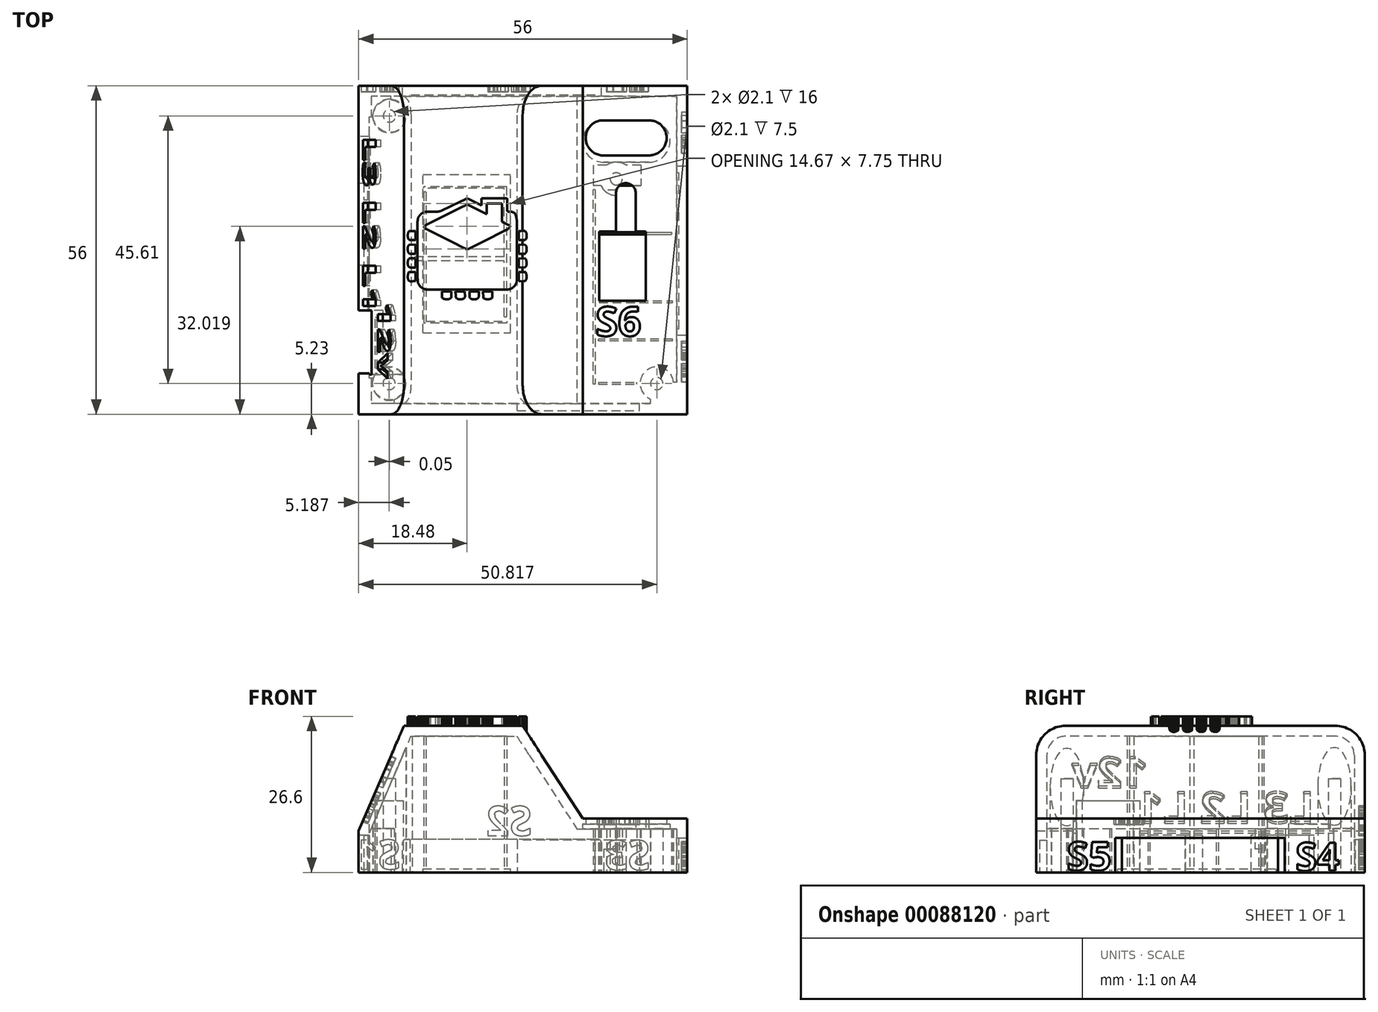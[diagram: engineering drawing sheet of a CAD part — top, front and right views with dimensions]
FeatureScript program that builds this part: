
annotation { "Feature Type Name" : "Feature", "Feature Type Description" : "" }
export const myFeature = defineFeature(function(context is Context, id is Id, definition is map)
    precondition{}
    {
        {
            var Q0;
            Q0=qCreatedBy(makeId("Top.planeOp"),FACE);
            var sketch = newSketch(context, id + "F0", { "sketchPlane" : qUnion([Q0])});
            skLineSegment(sketch, "E0.rect.bottom", {"start": v(22.84, -21.13) * mm, "end": v(-26.83, -21.13) * mm});
            skLineSegment(sketch, "E0.rect.top", {"start": v(22.84, 28.7) * mm, "end": v(-26.83, 28.7) * mm});
            skLineSegment(sketch, "E0.rect.left", {"start": v(22.84, -21.13) * mm, "end": v(22.84, 28.7) * mm});
            skPoint(sketch, "E0.rect.middle", {"position": v(-2, 3.78) * mm});
            skCircle(sketch, "E1", {"center": v(-24.81, -18.99) * mm, "radius": 1.05 * mm});
            skCircle(sketch, "E2", {"center": v(-24.76, 26.62) * mm, "radius": 1.05 * mm});
            skCircle(sketch, "E3", {"center": v(13.92, 15.91) * mm, "radius": 1.05 * mm});
            skLineSegment(sketch, "E4", {"start": v(-2, -21.13) * mm, "end": v(-2, -18.21) * mm});
            skCircle(sketch, "E5.MirrorC", {"center": v(20.82, -18.99) * mm, "radius": 1.05 * mm});
            skLineSegment(sketch, "E6.rect.bottom", {"start": v(24.75, -22.97) * mm, "end": v(-28.75, -22.97) * mm});
            skLineSegment(sketch, "E6.rect.top", {"start": v(24.75, 30.53) * mm, "end": v(-28.75, 30.53) * mm});
            skLineSegment(sketch, "E6.rect.left", {"start": v(24.75, -22.97) * mm, "end": v(24.75, 30.53) * mm});
            skLineSegment(sketch, "E6.rect.right", {"start": v(-28.75, -22.97) * mm, "end": v(-28.75, 30.53) * mm});
            skLineSegment(sketch, "E7.rect.bottom", {"start": v(26, -24.22) * mm, "end": v(-30, -24.22) * mm});
            skLineSegment(sketch, "E7.rect.top", {"start": v(26, 31.78) * mm, "end": v(-30, 31.78) * mm});
            skLineSegment(sketch, "E7.rect.left", {"start": v(26, -24.22) * mm, "end": v(26, 31.78) * mm});
            skLineSegment(sketch, "E7.rect.right", {"start": v(-30, -24.22) * mm, "end": v(-30, 31.78) * mm});
            skPoint(sketch, "E8", {"position": v(8.65, 14) * mm});
            skSolve(sketch);
        }
        {
            var Q0;
            Q0=qSketchRegion(id+"F0",true);
            var Q1;
            Q1=makeQuery(id+"F0.imprint","IMPRINT",FACE,{"disambiguationData":[TD([[makeQuery(id+"F0.imprint","IMPRINT",EDGE,{"derivedFrom":sQuery(id+"F0.wireOp",EDGE,"E1")}),-1.0]])]});
            extrude(context, id + "F1", {"entities" : qUnion([Q0, Q1]), "depth" : 25 * mm});
        }
        {
            var Q0;
            Q0=qCreatedBy(makeId("Front.planeOp"),FACE);
            var sketch = newSketch(context, id + "F2", { "sketchPlane" : qUnion([Q0])});
            skLineSegment(sketch, "E9", {"start": v(0, 0) * mm, "end": v(0, 7) * mm});
            skLineSegment(sketch, "E10", {"start": v(0, 7) * mm, "end": v(26.03, 7) * mm});
            skLineSegment(sketch, "E11", {"start": v(26.03, 9.19) * mm, "end": v(26.03, 25.51) * mm});
            skLineSegment(sketch, "E12", {"start": v(15.3, 7) * mm, "end": v(26.03, 7) * mm});
            skLineSegment(sketch, "E13", {"start": v(0, 7) * mm, "end": v(-30.02, 7) * mm});
            skLineSegment(sketch, "E14", {"start": v(-30.02, 7) * mm, "end": v(-22.06, 25.51) * mm});
            skLineSegment(sketch, "E15", {"start": v(-22.06, 25.51) * mm, "end": v(-2.39, 25.51) * mm});
            skLineSegment(sketch, "E16", {"start": v(26.03, 25.51) * mm, "end": v(-2.39, 25.51) * mm});
            skLineSegment(sketch, "E17", {"start": v(-22.06, 25.51) * mm, "end": v(-30.02, 25.51) * mm});
            skLineSegment(sketch, "E18", {"start": v(-30.02, 25.51) * mm, "end": v(-30.02, 7) * mm});
            skLineSegment(sketch, "E19", {"start": v(18.06, 10.7) * mm, "end": v(18.04, 10.7) * mm});
            skLineSegment(sketch, "E20", {"start": v(19.86, 9.19) * mm, "end": v(8.2, 9.19) * mm});
            skLineSegment(sketch, "E21", {"start": v(8.2, 9.19) * mm, "end": v(-2.39, 25.51) * mm});
            skLineSegment(sketch, "E22", {"start": v(19.86, 9.19) * mm, "end": v(26.03, 9.19) * mm});
            skSolve(sketch);
        }
        {
            var Q0;
            Q0=makeQuery(id+"F2.imprint","IMPRINT",FACE,{"disambiguationData":[TD([[makeQuery(id+"F2.imprint","IMPRINT",EDGE,{"derivedFrom":sQuery(id+"F2.wireOp",EDGE,"E14")}),1.0]])]});
            var Q1;
            {var subQ0=sQuery(id+"F2.wireOp",EDGE,"E11");Q1=makeQuery(id+"F2.imprint","IMPRINT",FACE,{"disambiguationData":[TD([[makeQuery(id+"F2.imprint","IMPRINT",EDGE,{"derivedFrom":subQ0}),1.0]])]});}
            extrude(context, id + "F3", {"entities" : qUnion([Q0, Q1]), "operationType" : NewBodyOperationType.REMOVE, "endBound" : BoundingType.UP_TO_NEXT, "oppositeDirection" : true, "depth" : 25 * mm, "hasSecondDirection" : true, "secondDirectionOppositeDirection" : false, "secondDirectionDepth" : 25 * mm});
        }
        {
            var Q0;
            Q0=makeQuery(id+"F1.opExtrude","CAP_EDGE",EDGE,{"disambiguationData":[OSD([sQuery(id+"F0.wireOp",EDGE,"E7.rect.right")])],"isStart":false});
            var Q1;
            Q1=makeQuery(id+"F3.boolean.opBoolean","COPY",EDGE,{"derivedFrom":makeQuery(id+"F3.opExtrude","TWEAK_EDGE",EDGE,{"derivedFrom":[makeQuery(id+"F1.opExtrude","CAP_FACE",FACE,{"disambiguationData":[OSD([sQuery(id+"F0.wireOp",EDGE,"E1"),sQuery(id+"F0.wireOp",EDGE,"E2"),sQuery(id+"F0.wireOp",EDGE,"E3"),sQuery(id+"F0.wireOp",EDGE,"E5.MirrorC"),sQuery(id+"F0.wireOp",EDGE,"E7.rect.bottom"),sQuery(id+"F0.wireOp",EDGE,"E7.rect.top"),sQuery(id+"F0.wireOp",EDGE,"E7.rect.left"),sQuery(id+"F0.wireOp",EDGE,"E7.rect.right")])],"isStart":false}),makeQuery(id+"F2.imprint","IMPRINT",EDGE,{"derivedFrom":sQuery(id+"F2.wireOp",EDGE,"ff17f17f-c23f-4b7b-92e3-773d52701edb")})]})});
            var Q2;
            Q2=makeQuery(id+"F3.boolean.opBoolean","COPY",EDGE,{"derivedFrom":makeQuery(id+"F3.opExtrude","TWEAK_EDGE",EDGE,{"derivedFrom":[makeQuery(id+"F1.opExtrude","CAP_FACE",FACE,{"disambiguationData":[OSD([sQuery(id+"F0.wireOp",EDGE,"E1"),sQuery(id+"F0.wireOp",EDGE,"E2"),sQuery(id+"F0.wireOp",EDGE,"E3"),sQuery(id+"F0.wireOp",EDGE,"E5.MirrorC"),sQuery(id+"F0.wireOp",EDGE,"E7.rect.bottom"),sQuery(id+"F0.wireOp",EDGE,"E7.rect.top"),sQuery(id+"F0.wireOp",EDGE,"E7.rect.left"),sQuery(id+"F0.wireOp",EDGE,"E7.rect.right")])],"isStart":false}),makeQuery(id+"F2.imprint","IMPRINT",EDGE,{"derivedFrom":sQuery(id+"F2.wireOp",EDGE,"7c30f75c-de24-4105-9ec6-0528e7197d9e")})]})});
            var Q3;
            {var subQ0=sQuery(id+"F2.wireOp",EDGE,"cpQ2IQLn-lepx-jHqE-Occg-QwCyzWVKbBFz");var subQ1=sQuery(id+"F2.wireOp",EDGE,"9136473a-ce9f-4df1-8e41-d79c079f6f02");var subQ2=makeQuery(id+"F2.imprint","INTERSECT",VERTEX,{"disambiguationData":[OD(0.0)],"derivedFrom":[subQ1,subQ0]});var subQ4=makeQuery(id+"F2.imprint","INTERSECT",VERTEX,{"disambiguationData":[OD(1.0)],"derivedFrom":[subQ1,subQ0]});Q3=makeQuery(id+"F3.boolean.opBoolean","COPY",EDGE,{"derivedFrom":makeQuery(id+"F3.opExtrude","TWEAK_EDGE",EDGE,{"derivedFrom":[makeQuery(id+"F1.opExtrude","CAP_FACE",FACE,{"disambiguationData":[OSD([sQuery(id+"F0.wireOp",EDGE,"E1"),sQuery(id+"F0.wireOp",EDGE,"E2"),sQuery(id+"F0.wireOp",EDGE,"E3"),sQuery(id+"F0.wireOp",EDGE,"E5.MirrorC"),sQuery(id+"F0.wireOp",EDGE,"E7.rect.bottom"),sQuery(id+"F0.wireOp",EDGE,"E7.rect.top"),sQuery(id+"F0.wireOp",EDGE,"E7.rect.left"),sQuery(id+"F0.wireOp",EDGE,"E7.rect.right")])],"isStart":false}),makeQuery(id+"F2.imprint","IMPRINT",EDGE,{"disambiguationData":[TD([[subQ4,1.0]])],"derivedFrom":subQ0}),makeQuery(id+"F2.imprint","IMPRINT",EDGE,{"disambiguationData":[TD([[subQ2,1.0]])],"derivedFrom":subQ0}),makeQuery(id+"F2.imprint","IMPRINT",EDGE,{"disambiguationData":[TD([[subQ2,-1.0]])],"derivedFrom":subQ0})]})});}
            var Q4;
            {var subQ0=sQuery(id+"F2.wireOp",EDGE,"cpQ2IQLn-lepx-jHqE-Occg-QwCyzWVKbBFz");var subQ1=sQuery(id+"F2.wireOp",EDGE,"9136473a-ce9f-4df1-8e41-d79c079f6f02");var subQ2=makeQuery(id+"F2.imprint","INTERSECT",VERTEX,{"disambiguationData":[OD(0.0)],"derivedFrom":[subQ1,subQ0]});var subQ3=sQuery(id+"F2.wireOp",EDGE,"7c30f75c-de24-4105-9ec6-0528e7197d9e");var subQ4=makeQuery(id+"F2.imprint","INTERSECT",VERTEX,{"derivedFrom":[subQ3,subQ0]});var subQ5=makeQuery(id+"F2.imprint","INTERSECT",VERTEX,{"disambiguationData":[OD(1.0)],"derivedFrom":[subQ1,subQ0]});Q4=makeQuery(id+"F3.boolean.opBoolean","COPY",EDGE,{"derivedFrom":makeQuery(id+"F3.opExtrude","TWEAK_EDGE",EDGE,{"disambiguationData":[OD(0.0)],"derivedFrom":[makeQuery(id+"F2.imprint","IMPRINT",EDGE,{"disambiguationData":[TD([[subQ4,1.0]])],"derivedFrom":subQ3}),makeQuery(id+"F2.imprint","IMPRINT",EDGE,{"disambiguationData":[TD([[subQ5,1.0]])],"derivedFrom":subQ0}),makeQuery(id+"F2.imprint","IMPRINT",EDGE,{"disambiguationData":[TD([[subQ2,1.0]])],"derivedFrom":subQ0}),makeQuery(id+"F2.imprint","IMPRINT",EDGE,{"disambiguationData":[TD([[subQ2,-1.0]])],"derivedFrom":subQ0})]})});}
            var Q5;
            {var subQ0=sQuery(id+"F2.wireOp",EDGE,"cpQ2IQLn-lepx-jHqE-Occg-QwCyzWVKbBFz");var subQ1=sQuery(id+"F2.wireOp",EDGE,"9136473a-ce9f-4df1-8e41-d79c079f6f02");var subQ2=makeQuery(id+"F2.imprint","INTERSECT",VERTEX,{"disambiguationData":[OD(0.0)],"derivedFrom":[subQ1,subQ0]});var subQ3=sQuery(id+"F2.wireOp",EDGE,"7c30f75c-de24-4105-9ec6-0528e7197d9e");var subQ4=makeQuery(id+"F2.imprint","INTERSECT",VERTEX,{"derivedFrom":[subQ3,subQ0]});var subQ5=makeQuery(id+"F2.imprint","INTERSECT",VERTEX,{"disambiguationData":[OD(1.0)],"derivedFrom":[subQ1,subQ0]});Q5=makeQuery(id+"F3.boolean.opBoolean","COPY",EDGE,{"derivedFrom":makeQuery(id+"F3.opExtrude","TWEAK_EDGE",EDGE,{"disambiguationData":[OD(1.0)],"derivedFrom":[makeQuery(id+"F2.imprint","IMPRINT",EDGE,{"disambiguationData":[TD([[subQ4,1.0]])],"derivedFrom":subQ3}),makeQuery(id+"F2.imprint","IMPRINT",EDGE,{"disambiguationData":[TD([[subQ5,1.0]])],"derivedFrom":subQ0}),makeQuery(id+"F2.imprint","IMPRINT",EDGE,{"disambiguationData":[TD([[subQ2,1.0]])],"derivedFrom":subQ0}),makeQuery(id+"F2.imprint","IMPRINT",EDGE,{"disambiguationData":[TD([[subQ2,-1.0]])],"derivedFrom":subQ0})]})});}
            var Q6;
            Q6=makeQuery(id+"F1.opExtrude","CAP_EDGE",EDGE,{"disambiguationData":[OSD([sQuery(id+"F0.wireOp",EDGE,"E7.rect.bottom")])],"isStart":false});
            var Q7;
            {var subQ0=sQuery(id+"F2.wireOp",EDGE,"cpQ2IQLn-lepx-jHqE-Occg-QwCyzWVKbBFz");var subQ1=sQuery(id+"F2.wireOp",EDGE,"9136473a-ce9f-4df1-8e41-d79c079f6f02");var subQ2=makeQuery(id+"F2.imprint","INTERSECT",VERTEX,{"disambiguationData":[OD(0.0)],"derivedFrom":[subQ1,subQ0]});var subQ4=makeQuery(id+"F2.imprint","INTERSECT",VERTEX,{"disambiguationData":[OD(1.0)],"derivedFrom":[subQ1,subQ0]});Q7=makeQuery(id+"F3.boolean.opBoolean","COPY",EDGE,{"derivedFrom":makeQuery(id+"F3.opExtrude","TWEAK_EDGE",EDGE,{"derivedFrom":[makeQuery(id+"F1.opExtrude","SWEPT_FACE",FACE,{"disambiguationData":[OSD([sQuery(id+"F0.wireOp",EDGE,"E7.rect.bottom")])]}),makeQuery(id+"F2.imprint","IMPRINT",EDGE,{"disambiguationData":[TD([[subQ4,1.0]])],"derivedFrom":subQ0}),makeQuery(id+"F2.imprint","IMPRINT",EDGE,{"disambiguationData":[TD([[subQ2,1.0]])],"derivedFrom":subQ0}),makeQuery(id+"F2.imprint","IMPRINT",EDGE,{"disambiguationData":[TD([[subQ2,-1.0]])],"derivedFrom":subQ0})]})});}
            var Q8;
            Q8=makeQuery(id+"F1.opExtrude","CAP_EDGE",EDGE,{"disambiguationData":[OSD([sQuery(id+"F0.wireOp",EDGE,"E7.rect.top")])],"isStart":false});
            var Q9;
            {var subQ0=sQuery(id+"F2.wireOp",EDGE,"cpQ2IQLn-lepx-jHqE-Occg-QwCyzWVKbBFz");var subQ1=sQuery(id+"F2.wireOp",EDGE,"9136473a-ce9f-4df1-8e41-d79c079f6f02");var subQ2=makeQuery(id+"F2.imprint","INTERSECT",VERTEX,{"disambiguationData":[OD(0.0)],"derivedFrom":[subQ1,subQ0]});var subQ4=makeQuery(id+"F2.imprint","INTERSECT",VERTEX,{"disambiguationData":[OD(1.0)],"derivedFrom":[subQ1,subQ0]});Q9=makeQuery(id+"F3.boolean.opBoolean","COPY",EDGE,{"derivedFrom":makeQuery(id+"F3.opExtrude","TWEAK_EDGE",EDGE,{"derivedFrom":[makeQuery(id+"F1.opExtrude","SWEPT_FACE",FACE,{"disambiguationData":[OSD([sQuery(id+"F0.wireOp",EDGE,"E7.rect.top")])]}),makeQuery(id+"F2.imprint","IMPRINT",EDGE,{"disambiguationData":[TD([[subQ4,1.0]])],"derivedFrom":subQ0}),makeQuery(id+"F2.imprint","IMPRINT",EDGE,{"disambiguationData":[TD([[subQ2,1.0]])],"derivedFrom":subQ0}),makeQuery(id+"F2.imprint","IMPRINT",EDGE,{"disambiguationData":[TD([[subQ2,-1.0]])],"derivedFrom":subQ0})]})});}
            var Q10;
            Q10=makeQuery(id+"F3.boolean.opBoolean","COPY",EDGE,{"derivedFrom":makeQuery(id+"F3.opExtrude","TWEAK_EDGE",EDGE,{"derivedFrom":[makeQuery(id+"F1.opExtrude","CAP_FACE",FACE,{"disambiguationData":[OSD([sQuery(id+"F0.wireOp",EDGE,"E1"),sQuery(id+"F0.wireOp",EDGE,"E2"),sQuery(id+"F0.wireOp",EDGE,"E3"),sQuery(id+"F0.wireOp",EDGE,"E5.MirrorC"),sQuery(id+"F0.wireOp",EDGE,"E7.rect.bottom"),sQuery(id+"F0.wireOp",EDGE,"E7.rect.top"),sQuery(id+"F0.wireOp",EDGE,"E7.rect.left"),sQuery(id+"F0.wireOp",EDGE,"E7.rect.right")])],"isStart":false}),makeQuery(id+"F2.imprint","IMPRINT",EDGE,{"derivedFrom":sQuery(id+"F2.wireOp",EDGE,"99fa5713-44e2-4710-8a3e-a5a5802f03ed")})]})});
            var Q11;
            Q11=makeQuery(id+"F3.boolean.opBoolean","COPY",EDGE,{"derivedFrom":makeQuery(id+"F3.opExtrude","TWEAK_EDGE",EDGE,{"derivedFrom":[makeQuery(id+"F1.opExtrude","CAP_FACE",FACE,{"disambiguationData":[OSD([sQuery(id+"F0.wireOp",EDGE,"E1"),sQuery(id+"F0.wireOp",EDGE,"E2"),sQuery(id+"F0.wireOp",EDGE,"E3"),sQuery(id+"F0.wireOp",EDGE,"E5.MirrorC"),sQuery(id+"F0.wireOp",EDGE,"E7.rect.bottom"),sQuery(id+"F0.wireOp",EDGE,"E7.rect.top"),sQuery(id+"F0.wireOp",EDGE,"E7.rect.left"),sQuery(id+"F0.wireOp",EDGE,"E7.rect.right")])],"isStart":false}),makeQuery(id+"F2.imprint","IMPRINT",EDGE,{"derivedFrom":sQuery(id+"F2.wireOp",EDGE,"E14")})]})});
            var Q12;
            Q12=makeQuery(id+"F3.boolean.opBoolean","COPY",EDGE,{"derivedFrom":makeQuery(id+"F3.opExtrude","TWEAK_EDGE",EDGE,{"derivedFrom":[makeQuery(id+"F1.opExtrude","CAP_FACE",FACE,{"disambiguationData":[OSD([sQuery(id+"F0.wireOp",EDGE,"E1"),sQuery(id+"F0.wireOp",EDGE,"E2"),sQuery(id+"F0.wireOp",EDGE,"E3"),sQuery(id+"F0.wireOp",EDGE,"E5.MirrorC"),sQuery(id+"F0.wireOp",EDGE,"E7.rect.bottom"),sQuery(id+"F0.wireOp",EDGE,"E7.rect.top"),sQuery(id+"F0.wireOp",EDGE,"E7.rect.left"),sQuery(id+"F0.wireOp",EDGE,"E7.rect.right")])],"isStart":false}),makeQuery(id+"F2.imprint","IMPRINT",EDGE,{"derivedFrom":sQuery(id+"F2.wireOp",EDGE,"E21")})]})});
            var Q13;
            Q13=makeQuery(id+"F3.boolean.opBoolean","COPY",EDGE,{"derivedFrom":makeQuery(id+"F3.opExtrude","TWEAK_EDGE",EDGE,{"derivedFrom":[makeQuery(id+"F2.imprint","IMPRINT",EDGE,{"derivedFrom":sQuery(id+"F2.wireOp",EDGE,"E20")}),makeQuery(id+"F2.imprint","IMPRINT",EDGE,{"derivedFrom":sQuery(id+"F2.wireOp",EDGE,"E21")})]})});
            var Q14;
            Q14=makeQuery(id+"F3.boolean.opBoolean","COPY",EDGE,{"derivedFrom":makeQuery(id+"F3.opExtrude","TWEAK_EDGE",EDGE,{"derivedFrom":[makeQuery(id+"F1.opExtrude","SWEPT_FACE",FACE,{"disambiguationData":[OSD([sQuery(id+"F0.wireOp",EDGE,"E7.rect.bottom")])]}),makeQuery(id+"F2.imprint","IMPRINT",EDGE,{"derivedFrom":sQuery(id+"F2.wireOp",EDGE,"E21")})]})});
            var Q15;
            Q15=makeQuery(id+"F3.boolean.opBoolean","COPY",EDGE,{"derivedFrom":makeQuery(id+"F3.opExtrude","TWEAK_EDGE",EDGE,{"derivedFrom":[makeQuery(id+"F1.opExtrude","SWEPT_FACE",FACE,{"disambiguationData":[OSD([sQuery(id+"F0.wireOp",EDGE,"E7.rect.top")])]}),makeQuery(id+"F2.imprint","IMPRINT",EDGE,{"derivedFrom":sQuery(id+"F2.wireOp",EDGE,"E21")})]})});
            var Q16;
            Q16=makeQuery(id+"F3.boolean.opBoolean","COPY",EDGE,{"derivedFrom":makeQuery(id+"F3.opExtrude","TWEAK_EDGE",EDGE,{"derivedFrom":[makeQuery(id+"F1.opExtrude","SWEPT_FACE",FACE,{"disambiguationData":[OSD([sQuery(id+"F0.wireOp",EDGE,"E7.rect.left")])]}),makeQuery(id+"F2.imprint","IMPRINT",EDGE,{"derivedFrom":sQuery(id+"F2.wireOp",EDGE,"E20")}),makeQuery(id+"F2.imprint","IMPRINT",EDGE,{"derivedFrom":sQuery(id+"F2.wireOp",EDGE,"E22")})]})});
            var Q17;
            Q17=makeQuery(id+"F3.boolean.opBoolean","COPY",EDGE,{"derivedFrom":makeQuery(id+"F3.opExtrude","TWEAK_EDGE",EDGE,{"derivedFrom":[makeQuery(id+"F2.imprint","IMPRINT",EDGE,{"derivedFrom":sQuery(id+"F2.wireOp",EDGE,"E20")}),makeQuery(id+"F2.imprint","IMPRINT",EDGE,{"derivedFrom":sQuery(id+"F2.wireOp",EDGE,"E21")}),makeQuery(id+"F2.imprint","IMPRINT",EDGE,{"derivedFrom":sQuery(id+"F2.wireOp",EDGE,"E22")})]})});
            fillet(context, id + "F4", {"entities" : qUnion([Q0, Q1, Q2, Q3, Q4, Q5, Q6, Q7, Q8, Q9, Q10, Q11, Q12, Q13, Q14, Q15, Q16, Q17]), "radius" : 5 * mm, "tangentPropagation" : true, "allowEdgeOverflow" : false});
        }
        {
            var Q0;
            Q0=makeQuery(id+"F1.opExtrude","SWEPT_BODY",BODY,{"disambiguationData":[OSD([sQuery(id+"F0.wireOp",EDGE,"E1"),sQuery(id+"F0.wireOp",EDGE,"E2"),sQuery(id+"F0.wireOp",EDGE,"E3"),sQuery(id+"F0.wireOp",EDGE,"E5.MirrorC"),sQuery(id+"F0.wireOp",EDGE,"E7.rect.bottom"),sQuery(id+"F0.wireOp",EDGE,"E7.rect.top"),sQuery(id+"F0.wireOp",EDGE,"E7.rect.left"),sQuery(id+"F0.wireOp",EDGE,"E7.rect.right")])]});
            transform(context, id + "F5", {"entities" : qUnion([Q0]), "transformType" : TransformType.TRANSLATION_3D, "dx" : -5 * mm, "dy" : -12 * mm, "dz" : 0 * mm, "makeCopy" : false});
        }
        {
            var Q0;
            Q0=makeQuery(id+"F1.opExtrude","CAP_FACE",FACE,{"disambiguationData":[OSD([sQuery(id+"F0.wireOp",EDGE,"E1"),sQuery(id+"F0.wireOp",EDGE,"E2"),sQuery(id+"F0.wireOp",EDGE,"E3"),sQuery(id+"F0.wireOp",EDGE,"E5.MirrorC"),sQuery(id+"F0.wireOp",EDGE,"E7.rect.bottom"),sQuery(id+"F0.wireOp",EDGE,"E7.rect.top"),sQuery(id+"F0.wireOp",EDGE,"E7.rect.left"),sQuery(id+"F0.wireOp",EDGE,"E7.rect.right")])],"isStart":true});
            shell(context, id + "F6", {"entities" : qUnion([Q0]), "thickness" : 1.8 * mm});
        }
        {
            var Q0;
            Q0=makeQuery(id+"F1.opExtrude","SWEPT_FACE",FACE,{"disambiguationData":[OSD([sQuery(id+"F0.wireOp",EDGE,"E7.rect.left")])]});
            cPlane(context, id + "F7", {"entities" : qUnion([Q0]), "cplaneType" : CPlaneType.OFFSET, "offset" : 0 * mm, "width" : 150 * mm, "height" : 150 * mm});
        }
        {
            var Q0;
            Q0=qCreatedBy(id+"F7.planeOp",FACE);
            var sketch = newSketch(context, id + "F8", { "sketchPlane" : qUnion([Q0])});
            skLineSegment(sketch, "E23.bottom", {"start": v(6.92, 0) * mm, "end": v(-20.2, 0) * mm});
            skLineSegment(sketch, "E23.top", {"start": v(6.12, 5.87) * mm, "end": v(-20.2, 5.87) * mm});
            skLineSegment(sketch, "E24", {"start": v(-20.2, 5.87) * mm, "end": v(-21.64, 5.87) * mm});
            skLineSegment(sketch, "E25", {"start": v(-21.64, 5.87) * mm, "end": v(-21.64, 0) * mm});
            skLineSegment(sketch, "E26", {"start": v(-21.64, 0) * mm, "end": v(-20.2, 0) * mm});
            skLineSegment(sketch, "E27", {"start": v(6.12, 5.87) * mm, "end": v(6.12, 0) * mm});
            skPoint(sketch, "E28.orphan", {"position": v(7.84, 0) * mm});
            skLineSegment(sketch, "E29", {"start": v(4.97, 0) * mm, "end": v(4.97, 5.87) * mm});
            skLineSegment(sketch, "E30", {"start": v(-21.64, 5.87) * mm, "end": v(-22.73, 5.87) * mm});
            skLineSegment(sketch, "E31", {"start": v(-22.73, 5.87) * mm, "end": v(-22.73, 0) * mm});
            skLineSegment(sketch, "E32", {"start": v(-22.73, 0) * mm, "end": v(-21.64, 0) * mm});
            skSolve(sketch);
        }
        {
            var Q0;
            {var subQ1=sQuery(id+"F8.wireOp",EDGE,"E24");Q0=makeQuery(id+"F8.imprint","IMPRINT",FACE,{"disambiguationData":[TD([[makeQuery(id+"F8.imprint","IMPRINT",EDGE,{"derivedFrom":subQ1}),1.0]])]});}
            extrude(context, id + "F9", {"entities" : qUnion([Q0]), "operationType" : NewBodyOperationType.REMOVE, "oppositeDirection" : true, "depth" : (1.7 - 0.3) * mm});
        }
        {
            var Q0;
            Q0=makeQuery(id+"F8.imprint","IMPRINT",FACE,{"disambiguationData":[TD([[makeQuery(id+"F8.imprint","IMPRINT",EDGE,{"derivedFrom":sQuery(id+"F8.wireOp",EDGE,"E25")}),-1.0]])]});
            var Q1;
            {var subQ0=sQuery(id+"F8.wireOp",EDGE,"E27");Q1=makeQuery(id+"F8.imprint","IMPRINT",FACE,{"disambiguationData":[TD([[makeQuery(id+"F8.imprint","IMPRINT",EDGE,{"derivedFrom":subQ0}),-1.0]])]});}
            extrude(context, id + "F10", {"entities" : qUnion([Q0, Q1]), "operationType" : NewBodyOperationType.REMOVE, "oppositeDirection" : true, "depth" : 2 * mm});
        }
        {
            var Q0;
            Q0=makeQuery(id+"F1.opExtrude","SWEPT_FACE",FACE,{"disambiguationData":[OSD([sQuery(id+"F0.wireOp",EDGE,"E7.rect.right")])]});
            cPlane(context, id + "F11", {"entities" : qUnion([Q0]), "cplaneType" : CPlaneType.OFFSET, "offset" : 0 * mm, "width" : 150 * mm, "height" : 150 * mm});
        }
        {
            var Q0;
            Q0=qCreatedBy(id+"F11.planeOp",FACE);
            var sketch = newSketch(context, id + "F12", { "sketchPlane" : qUnion([Q0])});
            skLineSegment(sketch, "E33.top", {"start": v(-11.15, 6.31) * mm, "end": v(-3.45, 6.31) * mm});
            skLineSegment(sketch, "E34", {"start": v(27.25, 11.15) * mm, "end": v(27.25, 11.15) * mm});
            skLineSegment(sketch, "E35", {"start": v(-11.15, 0) * mm, "end": v(-11.15, 6.31) * mm});
            skPoint(sketch, "E36.start.orphan", {"position": v(-15.15, 0) * mm});
            skLineSegment(sketch, "E37", {"start": v(29.28, 0) * mm, "end": v(-11.15, 0) * mm});
            skLineSegment(sketch, "E38", {"start": v(-10.29, 6.31) * mm, "end": v(-10.29, 0) * mm});
            skLineSegment(sketch, "E39", {"start": v(19.35, 12.2) * mm, "end": v(29.28, 12.2) * mm});
            skLineSegment(sketch, "E40", {"start": v(-11.15, 3.16) * mm, "end": v(-3.45, 3.16) * mm, "construction": true});
            skLineSegment(sketch, "E41", {"start": v(-3.45, 3.16) * mm, "end": v(-0.05, 3.16) * mm, "construction": true});
            skLineSegment(sketch, "E42", {"start": v(-0.05, 3.16) * mm, "end": v(7.65, 3.16) * mm, "construction": true});
            skLineSegment(sketch, "E43", {"start": v(7.65, 3.16) * mm, "end": v(11.05, 3.16) * mm, "construction": true});
            skLineSegment(sketch, "E44.trimOffspring", {"start": v(11.05, 6.31) * mm, "end": v(18.53, 6.31) * mm});
            skLineSegment(sketch, "E45", {"start": v(11.9, 6.31) * mm, "end": v(11.9, 0) * mm});
            skLineSegment(sketch, "E46", {"start": v(0, 6.31) * mm, "end": v(7.65, 6.31) * mm});
            skLineSegment(sketch, "E47", {"start": v(7.65, 0) * mm, "end": v(0, 0) * mm});
            skLineSegment(sketch, "E48", {"start": v(-3.45, 0) * mm, "end": v(-11.15, 0) * mm});
            skLineSegment(sketch, "E49", {"start": v(30.08, 0) * mm, "end": v(11.05, 0) * mm});
            skLineSegment(sketch, "E50.bottom", {"start": v(-0.32, 0) * mm, "end": v(-3.15, 0) * mm});
            skLineSegment(sketch, "E50.top", {"start": v(-0.32, 6.31) * mm, "end": v(-3.15, 6.31) * mm});
            skLineSegment(sketch, "E50.left", {"start": v(-0.32, 0) * mm, "end": v(-0.32, 6.31) * mm});
            skLineSegment(sketch, "E50.right", {"start": v(-3.15, 0) * mm, "end": v(-3.15, 6.31) * mm});
            skLineSegment(sketch, "E51.bottom", {"start": v(10.8, 0) * mm, "end": v(7.92, 0) * mm});
            skLineSegment(sketch, "E51.top", {"start": v(10.8, 6.31) * mm, "end": v(7.92, 6.31) * mm});
            skLineSegment(sketch, "E51.left", {"start": v(10.8, 0) * mm, "end": v(10.8, 6.31) * mm});
            skLineSegment(sketch, "E51.right", {"start": v(7.92, 0) * mm, "end": v(7.92, 6.31) * mm});
            skLineSegment(sketch, "E52", {"start": v(-3.45, 6.31) * mm, "end": v(11.05, 6.31) * mm});
            skLineSegment(sketch, "E53", {"start": v(29.28, 12.2) * mm, "end": v(29.28, 0) * mm});
            skPoint(sketch, "E54.end.orphan", {"position": v(30.08, 11.15) * mm});
            skPoint(sketch, "E54.start.orphan", {"position": v(30.08, 12.2) * mm});
            skLineSegment(sketch, "E55", {"start": v(18.53, 6.31) * mm, "end": v(18.53, 12.2) * mm});
            skLineSegment(sketch, "E56", {"start": v(18.53, 12.2) * mm, "end": v(19.35, 12.2) * mm});
            skPoint(sketch, "E57.start.orphan", {"position": v(19.35, 11.15) * mm});
            skPoint(sketch, "E58.end.orphan", {"position": v(19.35, 0) * mm});
            skPoint(sketch, "E58.start.orphan", {"position": v(19.35, 6.31) * mm});
            skLineSegment(sketch, "E59", {"start": v(28.38, 0) * mm, "end": v(28.38, 12.2) * mm});
            skLineSegment(sketch, "E60", {"start": v(19.35, 12.2) * mm, "end": v(19.35, 0) * mm});
            skLineSegment(sketch, "E61", {"start": v(18.53, 6.31) * mm, "end": v(18.53, 0) * mm});
            skSolve(sketch);
        }
        {
            var Q0;
            {var subQ0=sQuery(id+"F12.wireOp",EDGE,"E35");Q0=makeQuery(id+"F12.imprint","IMPRINT",FACE,{"disambiguationData":[TD([[makeQuery(id+"F12.imprint","IMPRINT",EDGE,{"derivedFrom":subQ0}),-1.0]])]});}
            var Q1;
            {var subQ1=sQuery(id+"F12.wireOp",EDGE,"E38");Q1=makeQuery(id+"F12.imprint","IMPRINT",FACE,{"disambiguationData":[TD([[makeQuery(id+"F12.imprint","IMPRINT",EDGE,{"derivedFrom":subQ1}),1.0]])]});}
            var Q2;
            {var subQ0=sQuery(id+"F12.wireOp",EDGE,"LVVauTd6-uSLQ-SWm0-nvuu-HrEgJgk2loCY");Q2=makeQuery(id+"F12.imprint","IMPRINT",FACE,{"disambiguationData":[TD([[makeQuery(id+"F12.imprint","IMPRINT",EDGE,{"derivedFrom":subQ0}),-1.0]])]});}
            var Q3;
            Q3=makeQuery(id+"F12.imprint","IMPRINT",FACE,{"disambiguationData":[TD([[makeQuery(id+"F12.imprint","IMPRINT",EDGE,{"derivedFrom":sQuery(id+"F12.wireOp",EDGE,"Bzj0w9RH-aYdH-ZF7y-Z4mK-Pif1xP8myCSu")}),1.0]])]});
            var Q4;
            Q4=makeQuery(id+"F12.imprint","IMPRINT",FACE,{"disambiguationData":[TD([[makeQuery(id+"F12.imprint","IMPRINT",EDGE,{"derivedFrom":sQuery(id+"F12.wireOp",EDGE,"E50.bottom")}),-1.0]])]});
            var Q5;
            {var subQ1=sQuery(id+"F12.wireOp",EDGE,"E47");Q5=makeQuery(id+"F12.imprint","IMPRINT",FACE,{"disambiguationData":[TD([[makeQuery(id+"F12.imprint","IMPRINT",EDGE,{"derivedFrom":subQ1}),-1.0]])]});}
            var Q6;
            Q6=makeQuery(id+"F12.imprint","IMPRINT",FACE,{"disambiguationData":[TD([[makeQuery(id+"F12.imprint","IMPRINT",EDGE,{"derivedFrom":sQuery(id+"F12.wireOp",EDGE,"E51.bottom")}),-1.0]])]});
            var Q7;
            {var subQ3=sQuery(id+"F12.wireOp",EDGE,"E45");Q7=makeQuery(id+"F12.imprint","IMPRINT",FACE,{"disambiguationData":[TD([[makeQuery(id+"F12.imprint","IMPRINT",EDGE,{"derivedFrom":subQ3}),-1.0]])]});}
            var Q8;
            {var subQ2=sQuery(id+"F12.wireOp",EDGE,"E59");Q8=makeQuery(id+"F12.imprint","IMPRINT",FACE,{"disambiguationData":[TD([[makeQuery(id+"F12.imprint","IMPRINT",EDGE,{"derivedFrom":subQ2}),1.0]])]});}
            var Q9;
            {var subQ2=sQuery(id+"F12.wireOp",EDGE,"E45");Q9=makeQuery(id+"F12.imprint","IMPRINT",FACE,{"disambiguationData":[TD([[makeQuery(id+"F12.imprint","IMPRINT",EDGE,{"derivedFrom":subQ2}),1.0]])]});}
            extrude(context, id + "F13", {"entities" : qUnion([Q0, Q1, Q2, Q3, Q4, Q5, Q6, Q7, Q8, Q9]), "operationType" : NewBodyOperationType.REMOVE, "oppositeDirection" : true, "depth" : 1.6 * mm});
        }
        {
            var Q0;
            {var subQ0=sQuery(id+"F12.wireOp",EDGE,"E35");Q0=makeQuery(id+"F12.imprint","IMPRINT",FACE,{"disambiguationData":[TD([[makeQuery(id+"F12.imprint","IMPRINT",EDGE,{"derivedFrom":subQ0}),-1.0]])]});}
            var Q1;
            Q1=makeQuery(id+"F12.imprint","IMPRINT",FACE,{"disambiguationData":[TD([[makeQuery(id+"F12.imprint","IMPRINT",EDGE,{"derivedFrom":sQuery(id+"F12.wireOp",EDGE,"E55")}),-1.0]])]});
            var Q2;
            {var subQ0=sQuery(id+"F12.wireOp",EDGE,"E53");Q2=makeQuery(id+"F12.imprint","IMPRINT",FACE,{"disambiguationData":[TD([[makeQuery(id+"F12.imprint","IMPRINT",EDGE,{"derivedFrom":subQ0}),-1.0]])]});}
            var Q3;
            {var subQ2=sQuery(id+"F12.wireOp",EDGE,"E59");Q3=makeQuery(id+"F12.imprint","IMPRINT",FACE,{"disambiguationData":[TD([[makeQuery(id+"F12.imprint","IMPRINT",EDGE,{"derivedFrom":subQ2}),1.0]])]});}
            extrude(context, id + "F14", {"entities" : qUnion([Q0, Q1, Q2, Q3]), "operationType" : NewBodyOperationType.REMOVE, "oppositeDirection" : true, "depth" : 8 * mm});
        }
        {
            var Q0;
            Q0=qCreatedBy(makeId("Top.planeOp"),FACE);
            var sketch = newSketch(context, id + "F15", { "sketchPlane" : qUnion([Q0])});
            skLineSegment(sketch, "E62.bottom", {"start": v(-27.19, -29.45) * mm, "end": v(-33.17, -29.45) * mm});
            skLineSegment(sketch, "E62.top", {"start": v(-27.19, -20) * mm, "end": v(-33.17, -20) * mm});
            skLineSegment(sketch, "E62.left", {"start": v(-27.19, -29.45) * mm, "end": v(-27.19, -21.32) * mm});
            skLineSegment(sketch, "E62.right", {"start": v(-33.17, -29.45) * mm, "end": v(-33.17, -21.32) * mm});
            skLineSegment(sketch, "E63", {"start": v(-33.17, -20.99) * mm, "end": v(-27.19, -20.99) * mm});
            skLineSegment(sketch, "E64", {"start": v(-33.17, -21.32) * mm, "end": v(-27.19, -21.32) * mm});
            skLineSegment(sketch, "E65.trimOffspring", {"start": v(-27.19, -20.99) * mm, "end": v(-27.19, -20) * mm});
            skLineSegment(sketch, "E66.trimOffspring", {"start": v(-33.17, -20.99) * mm, "end": v(-33.17, -20) * mm});
            skSolve(sketch);
        }
        {
            var Q0;
            Q0=qSketchRegion(id+"F15",true);
            var Q1;
            {var subQ0=sQuery(id+"F12.wireOp",EDGE,"E39");Q1=makeQuery(id+"F14.boolean.opBoolean","COPY",FACE,{"derivedFrom":makeQuery(id+"F14.opExtrude","SWEPT_FACE",FACE,{"disambiguationData":[OSD([subQ0]),TDD([makeQuery(id+"F12.imprint","IMPRINT",EDGE,{"disambiguationData":[TD([[makeQuery(id+"F12.imprint","INTERSECT",VERTEX,{"derivedFrom":[subQ0,sQuery(id+"F12.wireOp",EDGE,"E54")]}),1.0]])],"derivedFrom":subQ0})])]})});}
            extrude(context, id + "F16", {"entities" : qUnion([Q0]), "operationType" : NewBodyOperationType.REMOVE, "endBound" : BoundingType.UP_TO_SURFACE, "endBoundEntityFace" : qUnion([Q1]), "depth" : 11.3 * mm});
        }
        {
            var Q0;
            Q0=makeQuery(id+"F1.opExtrude","SWEPT_FACE",FACE,{"disambiguationData":[OSD([sQuery(id+"F0.wireOp",EDGE,"E7.rect.top")])]});
            cPlane(context, id + "F17", {"entities" : qUnion([Q0]), "cplaneType" : CPlaneType.OFFSET, "offset" : 0 * mm, "width" : 150 * mm, "height" : 150 * mm});
        }
        {
            var Q0;
            Q0=qCreatedBy(id+"F17.planeOp",FACE);
            var sketch = newSketch(context, id + "F18", { "sketchPlane" : qUnion([Q0])});
            skLineSegment(sketch, "E67.bottom", {"start": v(-6.36, 0) * mm, "end": v(27.5, 0) * mm});
            skLineSegment(sketch, "E67.left", {"start": v(-6.36, 0) * mm, "end": v(-6.36, 2.05) * mm});
            skLineSegment(sketch, "E68", {"start": v(-5.32, 3.26) * mm, "end": v(-5.32, 0) * mm});
            skLineSegment(sketch, "E69", {"start": v(27.5, 2.61) * mm, "end": v(27.5, 0) * mm});
            skLineSegment(sketch, "E70", {"start": v(26.27, 5.04) * mm, "end": v(26.27, 0) * mm});
            skPoint(sketch, "E71.visualSharp", {"position": v(-6.36, 7.05) * mm});
            skLineSegment(sketch, "E72", {"start": v(24.5, 5.61) * mm, "end": v(-1.9, 5.61) * mm});
            skPoint(sketch, "E73.visualSharp", {"position": v(-3.28, 5.61) * mm});
            skPoint(sketch, "E74.visualSharp", {"position": v(27.5, 5.61) * mm});
            skLineSegment(sketch, "E75", {"start": v(-6.36, 2.05) * mm, "end": v(-6.36, 5.08) * mm});
            skLineSegment(sketch, "E76", {"start": v(-5.83, 5.61) * mm, "end": v(-1.9, 5.61) * mm});
            skPoint(sketch, "E77.visualSharp", {"position": v(-6.36, 5.61) * mm});
            skArc(sketch, "E77.filletArc", {"start": v(-5.83, 5.61) * mm, "mid": v(-6.2, 5.45) * mm, "end": v(-6.36, 5.08) * mm});
            skLineSegment(sketch, "E78", {"start": v(-5.32, 3.26) * mm, "end": v(-5.32, 5.61) * mm});
            skLineSegment(sketch, "E79", {"start": v(24.5, 5.61) * mm, "end": v(26.98, 5.61) * mm});
            skLineSegment(sketch, "E80", {"start": v(27.5, 2.61) * mm, "end": v(27.5, 5.08) * mm});
            skLineSegment(sketch, "E81", {"start": v(26.27, 5.04) * mm, "end": v(26.27, 5.61) * mm});
            skArc(sketch, "E82.filletArc", {"start": v(27.5, 5.08) * mm, "mid": v(27.35, 5.45) * mm, "end": v(26.98, 5.61) * mm});
            skSolve(sketch);
        }
        {
            var Q0;
            Q0=qSketchRegion(id+"F18",true);
            extrude(context, id + "F19", {"entities" : qUnion([Q0]), "operationType" : NewBodyOperationType.REMOVE, "oppositeDirection" : true, "depth" : 1.6 * mm});
        }
        {
            var Q0;
            Q0=qCreatedBy(makeId("Top.planeOp"),FACE);
            var sketch = newSketch(context, id + "F20", { "sketchPlane" : qUnion([Q0])});
            skArc(sketch, "E83", {"start": v(6.16, 2.02) * mm, "mid": v(8.9, 0.56) * mm, "end": v(11.63, 2.02) * mm});
            skLineSegment(sketch, "E84", {"start": v(11.63, 2.02) * mm, "end": v(6.16, 2.02) * mm});
            skSolve(sketch);
        }
        {
            var Q0;
            Q0=qSketchRegion(id+"F20",true);
            extrude(context, id + "F21", {"entities" : qUnion([Q0]), "operationType" : NewBodyOperationType.REMOVE, "depth" : 4 * mm});
        }
        {
            var Q0;
            {var subQ0=sQuery(id+"F18.wireOp",EDGE,"E67.left");Q0=makeQuery(id+"F18.imprint","IMPRINT",FACE,{"disambiguationData":[TD([[makeQuery(id+"F18.imprint","IMPRINT",EDGE,{"derivedFrom":subQ0}),-1.0]])]});}
            var Q1;
            {var subQ0=sQuery(id+"F18.wireOp",EDGE,"E67.right");Q1=makeQuery(id+"F18.imprint","IMPRINT",FACE,{"disambiguationData":[TD([[makeQuery(id+"F18.imprint","IMPRINT",EDGE,{"derivedFrom":subQ0}),1.0]])]});}
            extrude(context, id + "F22", {"entities" : qUnion([Q0, Q1]), "operationType" : NewBodyOperationType.REMOVE, "oppositeDirection" : true, "depth" : 2 * mm});
        }
        {
            var Q0;
            Q0=qCreatedBy(makeId("Top.planeOp"),FACE);
            var sketch = newSketch(context, id + "F23", { "sketchPlane" : qUnion([Q0])});
            skLineSegment(sketch, "E85", {"start": v(21, 19.9) * mm, "end": v(21, 10.4) * mm, "construction": true});
            skLineSegment(sketch, "E86", {"start": v(12.22, 0) * mm, "end": v(12.22, -5.06) * mm});
            skLineSegment(sketch, "E87", {"start": v(12.22, 0) * mm, "end": v(12.22, 1.5) * mm});
            skArc(sketch, "E88", {"start": v(14.47, 7.9) * mm, "mid": v(17.49, 10.88) * mm, "end": v(14.5, 13.88) * mm});
            skArc(sketch, "E89", {"start": v(6.7, 13.9) * mm, "mid": v(3.7, 10.9) * mm, "end": v(6.7, 7.9) * mm});
            skLineSegment(sketch, "E90", {"start": v(14.5, 13.88) * mm, "end": v(6.7, 13.9) * mm});
            skLineSegment(sketch, "E91", {"start": v(6.7, 7.9) * mm, "end": v(14.54, 7.9) * mm});
            skLineSegment(sketch, "E92", {"start": v(6, -5.57) * mm, "end": v(6, -16.85) * mm});
            skLineSegment(sketch, "E93", {"start": v(12.6, -16.85) * mm, "end": v(6, -16.85) * mm});
            skPoint(sketch, "E94.center.orphan", {"position": v(10.72, -16.85) * mm});
            skLineSegment(sketch, "E95", {"start": v(8.87, -5.06) * mm, "end": v(8.87, 1.5) * mm});
            skArc(sketch, "E96", {"start": v(12.22, 1.5) * mm, "mid": v(10.54, 3.17) * mm, "end": v(8.87, 1.5) * mm});
            skPoint(sketch, "E97.orphan", {"position": v(12.22, -16.85) * mm});
            skLineSegment(sketch, "E98", {"start": v(0, 0) * mm, "end": v(0, 19.9) * mm, "construction": true});
            skLineSegment(sketch, "E99", {"start": v(0, 19.9) * mm, "end": v(21, 19.9) * mm, "construction": true});
            skLineSegment(sketch, "E100", {"start": v(14.5, 10.9) * mm, "end": v(21, 10.9) * mm, "construction": true});
            skLineSegment(sketch, "E101", {"start": v(8.87, -5.06) * mm, "end": v(6, -5.06) * mm});
            skLineSegment(sketch, "E102", {"start": v(6, -5.06) * mm, "end": v(6, -5.57) * mm});
            skLineSegment(sketch, "E103", {"start": v(12.22, -5.06) * mm, "end": v(12.6, -5.06) * mm});
            skLineSegment(sketch, "E104", {"start": v(12.6, -16.85) * mm, "end": v(13.95, -16.85) * mm});
            skLineSegment(sketch, "E105", {"start": v(13.95, -16.85) * mm, "end": v(13.95, -5.06) * mm});
            skLineSegment(sketch, "E106", {"start": v(13.95, -5.06) * mm, "end": v(12.6, -5.06) * mm});
            skPoint(sketch, "E107.end.orphan", {"position": v(12.6, -5.57) * mm});
            skSolve(sketch);
        }
        {
            var Q0;
            Q0=qSketchRegion(id+"F23",true);
            extrude(context, id + "F24", {"entities" : qUnion([Q0]), "operationType" : NewBodyOperationType.REMOVE, "depth" : 25 * mm});
        }
        {
            var Q0;
            Q0=qCreatedBy(makeId("Top.planeOp"),FACE);
            var sketch = newSketch(context, id + "F25", { "sketchPlane" : qUnion([Q0])});
            skLineSegment(sketch, "E108", {"start": v(18.49, -17.16) * mm, "end": v(5.97, -17.16) * mm});
            skLineSegment(sketch, "E109", {"start": v(18.49, -16.86) * mm, "end": v(5.97, -16.86) * mm});
            skLineSegment(sketch, "E110", {"start": v(12.44, -31.08) * mm, "end": v(5.87, -31.08) * mm});
            skLineSegment(sketch, "E111", {"start": v(12.44, -30.78) * mm, "end": v(5.87, -30.78) * mm});
            skLineSegment(sketch, "E112.bottom", {"start": v(-33.84, 14.47) * mm, "end": v(-32.16, 14.47) * mm});
            skLineSegment(sketch, "E112.top", {"start": v(-33.84, 18.7) * mm, "end": v(-29.5, 18.7) * mm});
            skLineSegment(sketch, "E112.left", {"start": v(-33.84, 14.47) * mm, "end": v(-33.84, 18.7) * mm});
            skLineSegment(sketch, "E112.right", {"start": v(-29.5, 16.74) * mm, "end": v(-29.5, 18.7) * mm});
            skArc(sketch, "E113", {"start": v(-29.5, 16.74) * mm, "mid": v(-31.35, 16.22) * mm, "end": v(-32.16, 14.47) * mm});
            skLineSegment(sketch, "E114.bottom", {"start": v(-33.6, -31.08) * mm, "end": v(-33.6, -31.08) * mm});
            skLineSegment(sketch, "E114.top", {"start": v(-33.6, -34.81) * mm, "end": v(-31.03, -34.81) * mm});
            skLineSegment(sketch, "E114.left", {"start": v(-33.6, -31.08) * mm, "end": v(-33.6, -34.81) * mm});
            skLineSegment(sketch, "E114.right", {"start": v(-31.03, -31.08) * mm, "end": v(-31.03, -33.21) * mm});
            skLineSegment(sketch, "E115.bottom", {"start": v(-31.03, -34.81) * mm, "end": v(-28.95, -34.81) * mm});
            skLineSegment(sketch, "E115.top", {"start": v(-31.03, -33.21) * mm, "end": v(-28.95, -33.21) * mm});
            skLineSegment(sketch, "E115.right", {"start": v(-28.95, -34.81) * mm, "end": v(-28.95, -33.21) * mm});
            skPoint(sketch, "E116.end.orphan", {"position": v(-34.98, -31.08) * mm});
            skPoint(sketch, "E116.start.orphan", {"position": v(-34.98, -30.78) * mm});
            skLineSegment(sketch, "E117.bottom", {"start": v(16.87, -34.88) * mm, "end": v(19.69, -34.88) * mm});
            skLineSegment(sketch, "E117.top", {"start": v(16.87, -30.79) * mm, "end": v(19.69, -30.79) * mm});
            skLineSegment(sketch, "E117.left", {"start": v(16.87, -33.4) * mm, "end": v(16.87, -30.79) * mm});
            skLineSegment(sketch, "E117.right", {"start": v(19.69, -34.88) * mm, "end": v(19.69, -30.79) * mm});
            skLineSegment(sketch, "E118.bottom", {"start": v(16.87, -34.88) * mm, "end": v(14.73, -34.88) * mm});
            skLineSegment(sketch, "E118.top", {"start": v(16.87, -33.4) * mm, "end": v(14.73, -33.4) * mm});
            skLineSegment(sketch, "E118.right", {"start": v(14.73, -34.88) * mm, "end": v(14.73, -33.4) * mm});
            skLineSegment(sketch, "E119.top", {"start": v(-31.03, -30.09) * mm, "end": v(-33.6, -30.09) * mm});
            skLineSegment(sketch, "E119.left", {"start": v(-31.03, -31.08) * mm, "end": v(-31.03, -30.09) * mm});
            skLineSegment(sketch, "E119.right", {"start": v(-33.6, -31.08) * mm, "end": v(-33.6, -30.09) * mm});
            skLineSegment(sketch, "E120", {"start": v(5.87, -31.08) * mm, "end": v(5.87, -30.78) * mm});
            skPoint(sketch, "E121.end.orphan", {"position": v(-34.98, -17.16) * mm});
            skPoint(sketch, "E121.start.orphan", {"position": v(-34.98, -16.86) * mm});
            skLineSegment(sketch, "E122.trimOffspring", {"start": v(5.97, -17.16) * mm, "end": v(5.97, -16.86) * mm});
            skLineSegment(sketch, "E123.bottom", {"start": v(5.85, -23.4) * mm, "end": v(18.49, -23.4) * mm});
            skLineSegment(sketch, "E123.top", {"start": v(5.85, -23.7) * mm, "end": v(18.49, -23.7) * mm});
            skLineSegment(sketch, "E123.left", {"start": v(5.85, -23.4) * mm, "end": v(5.85, -23.7) * mm});
            skLineSegment(sketch, "E124", {"start": v(5.29, -31.08) * mm, "end": v(5.29, 2.03) * mm});
            skLineSegment(sketch, "E125", {"start": v(4.99, -31.08) * mm, "end": v(5.29, -31.08) * mm});
            skLineSegment(sketch, "E126", {"start": v(12.44, -30.78) * mm, "end": v(12.44, -31.08) * mm});
            skLineSegment(sketch, "E127", {"start": v(18.49, -16.86) * mm, "end": v(18.49, -17.16) * mm});
            skPoint(sketch, "E128.orphan", {"position": v(19.24, -17.16) * mm});
            skLineSegment(sketch, "E129.trimOffspring", {"start": v(18.49, -23.4) * mm, "end": v(18.49, -23.7) * mm});
            skPoint(sketch, "E130.orphan", {"position": v(19.24, -23.7) * mm});
            skLineSegment(sketch, "E131.trimOffspring", {"start": v(4.99, 2.03) * mm, "end": v(4.99, -31.08) * mm});
            skLineSegment(sketch, "E132", {"start": v(4.99, 2.03) * mm, "end": v(5.29, 2.03) * mm});
            skLineSegment(sketch, "E133.bottom", {"start": v(4.99, 2.73) * mm, "end": v(13.12, 2.73) * mm});
            skLineSegment(sketch, "E133.top", {"start": v(4.99, 6.24) * mm, "end": v(13.12, 6.24) * mm});
            skLineSegment(sketch, "E133.left", {"start": v(4.99, 2.73) * mm, "end": v(4.99, 6.24) * mm});
            skLineSegment(sketch, "E133.right", {"start": v(13.12, 2.73) * mm, "end": v(13.12, 6.24) * mm});
            skCircle(sketch, "E134", {"center": v(8.91, 3.9) * mm, "radius": 1.04 * mm});
            skPoint(sketch, "E134.first.point", {"position": v(8.9, 2.86) * mm});
            skPoint(sketch, "E134.second.point", {"position": v(8.95, 4.94) * mm});
            skPoint(sketch, "E134.third.point", {"position": v(9.95, 3.84) * mm});
            skSolve(sketch);
        }
        {
            var Q0;
            Q0=qSketchRegion(id+"F25",true);
            var Q1;
            Q1=makeQuery(id+"F6.opShell","OFFSET_FACE",FACE,{"disambiguationData":[OSD([sQuery(id+"F2.wireOp",EDGE,"E20"),sQuery(id+"F2.wireOp",EDGE,"E22")])]});
            extrude(context, id + "F26", {"entities" : qUnion([Q0]), "operationType" : NewBodyOperationType.ADD, "endBoundEntityFace" : qUnion([Q1]), "depth" : 7.5 * mm});
        }
        {
            var Q0;
            {var subQ0=sQuery(id+"F0.wireOp",EDGE,"E7.rect.bottom");var subQ3=sQuery(id+"F0.wireOp",EDGE,"E7.rect.right");var subQ4=sQuery(id+"F0.wireOp",EDGE,"E7.rect.left");var subQ5=sQuery(id+"F0.wireOp",EDGE,"E7.rect.top");var subQ6=sQuery(id+"F0.wireOp",EDGE,"E5.MirrorC");var subQ7=sQuery(id+"F0.wireOp",EDGE,"E3");var subQ8=sQuery(id+"F0.wireOp",EDGE,"E2");var subQ9=sQuery(id+"F0.wireOp",EDGE,"E1");var subQ10=makeQuery(id+"F1.opExtrude","CAP_FACE",FACE,{"disambiguationData":[OSD([subQ9,subQ8,subQ7,subQ6,subQ0,subQ5,subQ4,subQ3])],"isStart":false});Q0=makeQuery(id+"F29.boolean.opBoolean","SPLIT",FACE,{"disambiguationData":[TD([makeQuery(id+"F4.opFillet","BLEND_FACE",FACE,{"disambiguationData":[OSD([subQ0])]})])],"derivedFrom":subQ10});}
            cPlane(context, id + "F27", {"entities" : qUnion([Q0]), "cplaneType" : CPlaneType.OFFSET, "offset" : 1.6 * mm, "width" : 150 * mm, "height" : 150 * mm});
        }
        {
            var Q0;
            Q0=qCreatedBy(id+"F27.planeOp",FACE);
            var sketch = newSketch(context, id + "F28", { "sketchPlane" : qUnion([Q0])});
            skLineSegment(sketch, "E135", {"start": v(-14.06, 0.58) * mm, "end": v(-9.7, 0.57) * mm});
            skLineSegment(sketch, "E136", {"start": v(-8.04, -3.57) * mm, "end": v(-8.03, -3.84) * mm});
            skLineSegment(sketch, "E137", {"start": v(-8.03, -3.84) * mm, "end": v(-8.04, -13.15) * mm});
            skLineSegment(sketch, "E138", {"start": v(-8.04, -13.15) * mm, "end": v(-8.03, -13.22) * mm});
            skLineSegment(sketch, "E139", {"start": v(-8.03, -13.22) * mm, "end": v(-8.03, -13.28) * mm});
            skLineSegment(sketch, "E140", {"start": v(-8.03, -13.28) * mm, "end": v(-8.04, -13.35) * mm});
            skLineSegment(sketch, "E141", {"start": v(-8.04, -13.35) * mm, "end": v(-8.04, -13.42) * mm});
            skLineSegment(sketch, "E142", {"start": v(-8.04, -13.42) * mm, "end": v(-8.05, -13.48) * mm});
            skLineSegment(sketch, "E143", {"start": v(-8.05, -13.48) * mm, "end": v(-8.06, -13.55) * mm});
            skLineSegment(sketch, "E144", {"start": v(-8.06, -13.55) * mm, "end": v(-8.07, -13.61) * mm});
            skLineSegment(sketch, "E145", {"start": v(-8.07, -13.61) * mm, "end": v(-8.1, -13.68) * mm});
            skLineSegment(sketch, "E146", {"start": v(-8.1, -13.68) * mm, "end": v(-8.1, -13.74) * mm});
            skLineSegment(sketch, "E147", {"start": v(-8.1, -13.74) * mm, "end": v(-8.13, -13.8) * mm});
            skLineSegment(sketch, "E148", {"start": v(-8.13, -13.8) * mm, "end": v(-8.15, -13.86) * mm});
            skLineSegment(sketch, "E149", {"start": v(-8.15, -13.86) * mm, "end": v(-8.18, -13.93) * mm});
            skLineSegment(sketch, "E150", {"start": v(-8.18, -13.93) * mm, "end": v(-8.2, -13.99) * mm});
            skLineSegment(sketch, "E151", {"start": v(-8.2, -13.99) * mm, "end": v(-8.23, -14.05) * mm});
            skLineSegment(sketch, "E152", {"start": v(-8.23, -14.05) * mm, "end": v(-8.26, -14.1) * mm});
            skLineSegment(sketch, "E153", {"start": v(-8.26, -14.1) * mm, "end": v(-8.3, -14.16) * mm});
            skLineSegment(sketch, "E154", {"start": v(-8.3, -14.16) * mm, "end": v(-8.33, -14.22) * mm});
            skLineSegment(sketch, "E155", {"start": v(-8.33, -14.22) * mm, "end": v(-8.37, -14.27) * mm});
            skLineSegment(sketch, "E156", {"start": v(-8.37, -14.27) * mm, "end": v(-8.4, -14.32) * mm});
            skLineSegment(sketch, "E157", {"start": v(-8.4, -14.32) * mm, "end": v(-8.45, -14.37) * mm});
            skLineSegment(sketch, "E158", {"start": v(-8.45, -14.37) * mm, "end": v(-8.5, -14.42) * mm});
            skLineSegment(sketch, "E159", {"start": v(-8.5, -14.42) * mm, "end": v(-8.54, -14.47) * mm});
            skLineSegment(sketch, "E160", {"start": v(-8.54, -14.47) * mm, "end": v(-8.59, -14.52) * mm});
            skLineSegment(sketch, "E161", {"start": v(-8.59, -14.52) * mm, "end": v(-8.63, -14.56) * mm});
            skLineSegment(sketch, "E162", {"start": v(-8.63, -14.56) * mm, "end": v(-8.69, -14.6) * mm});
            skLineSegment(sketch, "E163", {"start": v(-8.69, -14.6) * mm, "end": v(-8.74, -14.64) * mm});
            skLineSegment(sketch, "E164", {"start": v(-8.74, -14.64) * mm, "end": v(-8.8, -14.68) * mm});
            skLineSegment(sketch, "E165", {"start": v(-8.8, -14.68) * mm, "end": v(-8.85, -14.72) * mm});
            skLineSegment(sketch, "E166", {"start": v(-8.85, -14.72) * mm, "end": v(-8.9, -14.75) * mm});
            skLineSegment(sketch, "E167", {"start": v(-8.9, -14.75) * mm, "end": v(-8.95, -14.77) * mm});
            skLineSegment(sketch, "E168", {"start": v(-8.95, -14.77) * mm, "end": v(-8.99, -14.8) * mm});
            skLineSegment(sketch, "E169", {"start": v(-8.99, -14.8) * mm, "end": v(-9.03, -14.81) * mm});
            skLineSegment(sketch, "E170", {"start": v(-9.03, -14.81) * mm, "end": v(-9.07, -14.83) * mm});
            skLineSegment(sketch, "E171", {"start": v(-9.07, -14.83) * mm, "end": v(-9.11, -14.85) * mm});
            skLineSegment(sketch, "E172", {"start": v(-9.11, -14.85) * mm, "end": v(-9.16, -14.86) * mm});
            skLineSegment(sketch, "E173", {"start": v(-9.16, -14.86) * mm, "end": v(-9.2, -14.88) * mm});
            skLineSegment(sketch, "E174", {"start": v(-9.2, -14.88) * mm, "end": v(-9.24, -14.9) * mm});
            skLineSegment(sketch, "E175", {"start": v(-9.24, -14.9) * mm, "end": v(-9.29, -14.9) * mm});
            skLineSegment(sketch, "E176", {"start": v(-9.29, -14.9) * mm, "end": v(-9.33, -14.91) * mm});
            skLineSegment(sketch, "E177", {"start": v(-9.33, -14.91) * mm, "end": v(-9.38, -14.92) * mm});
            skLineSegment(sketch, "E178", {"start": v(-9.38, -14.92) * mm, "end": v(-9.42, -14.93) * mm});
            skLineSegment(sketch, "E179", {"start": v(-9.42, -14.93) * mm, "end": v(-9.51, -14.94) * mm});
            skLineSegment(sketch, "E180", {"start": v(-9.51, -14.94) * mm, "end": v(-9.6, -14.96) * mm});
            skLineSegment(sketch, "E181", {"start": v(-9.6, -14.96) * mm, "end": v(-9.74, -14.97) * mm});
            skLineSegment(sketch, "E182", {"start": v(-9.74, -14.97) * mm, "end": v(-10.2, -14.98) * mm});
            skLineSegment(sketch, "E183", {"start": v(-10.2, -14.98) * mm, "end": v(-23.2, -14.97) * mm});
            skLineSegment(sketch, "E184", {"start": v(-23.2, -14.97) * mm, "end": v(-23.28, -14.97) * mm});
            skLineSegment(sketch, "E185", {"start": v(-23.28, -14.97) * mm, "end": v(-23.35, -14.97) * mm});
            skLineSegment(sketch, "E186", {"start": v(-23.35, -14.97) * mm, "end": v(-23.43, -14.97) * mm});
            skLineSegment(sketch, "E187", {"start": v(-23.43, -14.97) * mm, "end": v(-23.5, -14.96) * mm});
            skLineSegment(sketch, "E188", {"start": v(-23.5, -14.96) * mm, "end": v(-23.58, -14.94) * mm});
            skLineSegment(sketch, "E189", {"start": v(-23.58, -14.94) * mm, "end": v(-23.65, -14.93) * mm});
            skLineSegment(sketch, "E190", {"start": v(-23.65, -14.93) * mm, "end": v(-23.72, -14.9) * mm});
            skLineSegment(sketch, "E191", {"start": v(-23.72, -14.9) * mm, "end": v(-23.8, -14.89) * mm});
            skLineSegment(sketch, "E192", {"start": v(-23.8, -14.89) * mm, "end": v(-23.86, -14.86) * mm});
            skLineSegment(sketch, "E193", {"start": v(-23.86, -14.86) * mm, "end": v(-23.93, -14.83) * mm});
            skLineSegment(sketch, "E194", {"start": v(-23.93, -14.83) * mm, "end": v(-24, -14.8) * mm});
            skLineSegment(sketch, "E195", {"start": v(-24, -14.8) * mm, "end": v(-24.07, -14.77) * mm});
            skLineSegment(sketch, "E196", {"start": v(-24.07, -14.77) * mm, "end": v(-24.13, -14.73) * mm});
            skLineSegment(sketch, "E197", {"start": v(-24.13, -14.73) * mm, "end": v(-24.2, -14.7) * mm});
            skLineSegment(sketch, "E198", {"start": v(-24.2, -14.7) * mm, "end": v(-24.26, -14.65) * mm});
            skLineSegment(sketch, "E199", {"start": v(-24.26, -14.65) * mm, "end": v(-24.32, -14.6) * mm});
            skLineSegment(sketch, "E200", {"start": v(-24.32, -14.6) * mm, "end": v(-24.38, -14.56) * mm});
            skLineSegment(sketch, "E201", {"start": v(-24.38, -14.56) * mm, "end": v(-24.43, -14.51) * mm});
            skLineSegment(sketch, "E202", {"start": v(-24.43, -14.51) * mm, "end": v(-24.48, -14.46) * mm});
            skLineSegment(sketch, "E203", {"start": v(-24.48, -14.46) * mm, "end": v(-24.54, -14.4) * mm});
            skLineSegment(sketch, "E204", {"start": v(-24.54, -14.4) * mm, "end": v(-24.59, -14.35) * mm});
            skLineSegment(sketch, "E205", {"start": v(-24.59, -14.35) * mm, "end": v(-24.63, -14.3) * mm});
            skLineSegment(sketch, "E206", {"start": v(-24.63, -14.3) * mm, "end": v(-24.68, -14.23) * mm});
            skLineSegment(sketch, "E207", {"start": v(-24.68, -14.23) * mm, "end": v(-24.72, -14.17) * mm});
            skLineSegment(sketch, "E208", {"start": v(-24.72, -14.17) * mm, "end": v(-24.76, -14.1) * mm});
            skLineSegment(sketch, "E209", {"start": v(-24.76, -14.1) * mm, "end": v(-24.8, -14.04) * mm});
            skLineSegment(sketch, "E210", {"start": v(-24.8, -14.04) * mm, "end": v(-24.82, -13.97) * mm});
            skLineSegment(sketch, "E211", {"start": v(-24.82, -13.97) * mm, "end": v(-24.85, -13.9) * mm});
            skLineSegment(sketch, "E212", {"start": v(-24.85, -13.9) * mm, "end": v(-24.88, -13.83) * mm});
            skLineSegment(sketch, "E213", {"start": v(-24.88, -13.83) * mm, "end": v(-24.9, -13.76) * mm});
            skLineSegment(sketch, "E214", {"start": v(-24.9, -13.76) * mm, "end": v(-24.92, -13.66) * mm});
            skLineSegment(sketch, "E215", {"start": v(-24.92, -13.66) * mm, "end": v(-24.94, -13.55) * mm});
            skLineSegment(sketch, "E216", {"start": v(-24.94, -13.55) * mm, "end": v(-24.96, -13.38) * mm});
            skLineSegment(sketch, "E217", {"start": v(-24.96, -13.38) * mm, "end": v(-24.98, -12.8) * mm});
            skLineSegment(sketch, "E218", {"start": v(-24.98, -12.8) * mm, "end": v(-24.98, -3.92) * mm});
            skLineSegment(sketch, "E219", {"start": v(-24.98, -3.92) * mm, "end": v(-24.97, -3.38) * mm});
            skLineSegment(sketch, "E220", {"start": v(-24.97, -3.38) * mm, "end": v(-24.96, -3.24) * mm});
            skLineSegment(sketch, "E221", {"start": v(-24.96, -3.24) * mm, "end": v(-24.95, -3.15) * mm});
            skLineSegment(sketch, "E222", {"start": v(-24.95, -3.15) * mm, "end": v(-24.94, -3.1) * mm});
            skLineSegment(sketch, "E223", {"start": v(-24.94, -3.1) * mm, "end": v(-24.93, -3.06) * mm});
            skLineSegment(sketch, "E224", {"start": v(-24.93, -3.06) * mm, "end": v(-24.93, -3.02) * mm});
            skLineSegment(sketch, "E225", {"start": v(-24.93, -3.02) * mm, "end": v(-24.92, -2.97) * mm});
            skLineSegment(sketch, "E226", {"start": v(-24.92, -2.97) * mm, "end": v(-24.9, -2.93) * mm});
            skLineSegment(sketch, "E227", {"start": v(-24.9, -2.93) * mm, "end": v(-24.9, -2.88) * mm});
            skLineSegment(sketch, "E228", {"start": v(-24.9, -2.88) * mm, "end": v(-24.88, -2.84) * mm});
            skLineSegment(sketch, "E229", {"start": v(-24.88, -2.84) * mm, "end": v(-24.87, -2.8) * mm});
            skLineSegment(sketch, "E230", {"start": v(-24.87, -2.8) * mm, "end": v(-24.85, -2.76) * mm});
            skLineSegment(sketch, "E231", {"start": v(-24.85, -2.76) * mm, "end": v(-24.83, -2.71) * mm});
            skLineSegment(sketch, "E232", {"start": v(-24.83, -2.71) * mm, "end": v(-24.81, -2.67) * mm});
            skLineSegment(sketch, "E233", {"start": v(-24.81, -2.67) * mm, "end": v(-24.8, -2.63) * mm});
            skLineSegment(sketch, "E234", {"start": v(-24.8, -2.63) * mm, "end": v(-24.77, -2.58) * mm});
            skLineSegment(sketch, "E235", {"start": v(-24.77, -2.58) * mm, "end": v(-24.74, -2.53) * mm});
            skLineSegment(sketch, "E236", {"start": v(-24.74, -2.53) * mm, "end": v(-24.7, -2.48) * mm});
            skLineSegment(sketch, "E237", {"start": v(-24.7, -2.48) * mm, "end": v(-24.68, -2.43) * mm});
            skLineSegment(sketch, "E238", {"start": v(-24.68, -2.43) * mm, "end": v(-24.64, -2.38) * mm});
            skLineSegment(sketch, "E239", {"start": v(-24.64, -2.38) * mm, "end": v(-24.6, -2.34) * mm});
            skLineSegment(sketch, "E240", {"start": v(-24.6, -2.34) * mm, "end": v(-24.57, -2.3) * mm});
            skLineSegment(sketch, "E241", {"start": v(-24.57, -2.3) * mm, "end": v(-24.53, -2.25) * mm});
            skLineSegment(sketch, "E242", {"start": v(-24.53, -2.25) * mm, "end": v(-24.5, -2.2) * mm});
            skLineSegment(sketch, "E243", {"start": v(-24.5, -2.2) * mm, "end": v(-24.45, -2.16) * mm});
            skLineSegment(sketch, "E244", {"start": v(-24.45, -2.16) * mm, "end": v(-24.41, -2.12) * mm});
            skLineSegment(sketch, "E245", {"start": v(-24.41, -2.12) * mm, "end": v(-24.37, -2.08) * mm});
            skLineSegment(sketch, "E246", {"start": v(-24.37, -2.08) * mm, "end": v(-24.32, -2.05) * mm});
            skLineSegment(sketch, "E247", {"start": v(-24.32, -2.05) * mm, "end": v(-24.28, -2.01) * mm});
            skLineSegment(sketch, "E248", {"start": v(-24.28, -2.01) * mm, "end": v(-24.23, -1.98) * mm});
            skLineSegment(sketch, "E249", {"start": v(-24.23, -1.98) * mm, "end": v(-24.18, -1.94) * mm});
            skLineSegment(sketch, "E250", {"start": v(-24.18, -1.94) * mm, "end": v(-24.13, -1.91) * mm});
            skLineSegment(sketch, "E251", {"start": v(-24.13, -1.91) * mm, "end": v(-24.08, -1.88) * mm});
            skLineSegment(sketch, "E252", {"start": v(-24.08, -1.88) * mm, "end": v(-24.03, -1.86) * mm});
            skLineSegment(sketch, "E253", {"start": v(-24.03, -1.86) * mm, "end": v(-23.98, -1.83) * mm});
            skLineSegment(sketch, "E254", {"start": v(-23.98, -1.83) * mm, "end": v(-23.93, -1.8) * mm});
            skLineSegment(sketch, "E255", {"start": v(-23.93, -1.8) * mm, "end": v(-23.87, -1.79) * mm});
            skLineSegment(sketch, "E256", {"start": v(-23.87, -1.79) * mm, "end": v(-23.82, -1.77) * mm});
            skLineSegment(sketch, "E257", {"start": v(-23.82, -1.77) * mm, "end": v(-23.76, -1.75) * mm});
            skLineSegment(sketch, "E258", {"start": v(-23.76, -1.75) * mm, "end": v(-23.7, -1.73) * mm});
            skLineSegment(sketch, "E259", {"start": v(-23.7, -1.73) * mm, "end": v(-23.65, -1.72) * mm});
            skLineSegment(sketch, "E260", {"start": v(-23.65, -1.72) * mm, "end": v(-23.6, -1.71) * mm});
            skLineSegment(sketch, "E261", {"start": v(-23.6, -1.71) * mm, "end": v(-23.53, -1.7) * mm});
            skLineSegment(sketch, "E262", {"start": v(-23.53, -1.7) * mm, "end": v(-23.48, -1.7) * mm});
            skLineSegment(sketch, "E263", {"start": v(-23.48, -1.7) * mm, "end": v(-23.32, -1.69) * mm});
            skLineSegment(sketch, "E264", {"start": v(-23.32, -1.69) * mm, "end": v(-23.17, -1.68) * mm});
            skLineSegment(sketch, "E265", {"start": v(-23.17, -1.68) * mm, "end": v(-22.95, -1.67) * mm});
            skLineSegment(sketch, "E266", {"start": v(-22.95, -1.67) * mm, "end": v(-21.9, -1.67) * mm});
            skLineSegment(sketch, "E267", {"start": v(-21.9, -1.67) * mm, "end": v(-21.52, -1.67) * mm});
            skLineSegment(sketch, "E268", {"start": v(-21.52, -1.67) * mm, "end": v(-21.3, -1.66) * mm});
            skLineSegment(sketch, "E269", {"start": v(-21.3, -1.66) * mm, "end": v(-21.2, -1.64) * mm});
            skLineSegment(sketch, "E270", {"start": v(-21.2, -1.64) * mm, "end": v(-20.86, -1.5) * mm});
            skLineSegment(sketch, "E271", {"start": v(-20.86, -1.5) * mm, "end": v(-17.7, 0.02) * mm});
            skLineSegment(sketch, "E272", {"start": v(-17.7, 0.02) * mm, "end": v(-17.01, 0.36) * mm});
            skLineSegment(sketch, "E273", {"start": v(-15.75, 0.24) * mm, "end": v(-14.06, -0.59) * mm});
            skLineSegment(sketch, "E274", {"start": v(-14.06, -0.59) * mm, "end": v(-14.06, 0.58) * mm});
            skLineSegment(sketch, "E275", {"start": v(-13.15, -0.33) * mm, "end": v(-13.15, -2.1) * mm});
            skLineSegment(sketch, "E276", {"start": v(-13.15, -2.1) * mm, "end": v(-13.26, -2.06) * mm});
            skLineSegment(sketch, "E277", {"start": v(-13.26, -2.06) * mm, "end": v(-13.9, -1.75) * mm});
            skLineSegment(sketch, "E278", {"start": v(-16.83, -0.6) * mm, "end": v(-17.05, -0.71) * mm});
            skLineSegment(sketch, "E279", {"start": v(-17.05, -0.71) * mm, "end": v(-17.27, -0.83) * mm});
            skLineSegment(sketch, "E280", {"start": v(-17.27, -0.83) * mm, "end": v(-18.4, -1.4) * mm});
            skLineSegment(sketch, "E281", {"start": v(-18.4, -1.4) * mm, "end": v(-22.7, -3.51) * mm});
            skLineSegment(sketch, "E282", {"start": v(-22.7, -3.51) * mm, "end": v(-23.6, -3.97) * mm});
            skLineSegment(sketch, "E283", {"start": v(-23.6, -3.97) * mm, "end": v(-23.64, -4) * mm});
            skLineSegment(sketch, "E284", {"start": v(-23.64, -4) * mm, "end": v(-23.69, -4.02) * mm});
            skLineSegment(sketch, "E285", {"start": v(-23.69, -4.02) * mm, "end": v(-23.73, -4.05) * mm});
            skLineSegment(sketch, "E286", {"start": v(-23.73, -4.05) * mm, "end": v(-23.76, -4.08) * mm});
            skLineSegment(sketch, "E287", {"start": v(-23.76, -4.08) * mm, "end": v(-23.79, -4.1) * mm});
            skLineSegment(sketch, "E288", {"start": v(-23.79, -4.1) * mm, "end": v(-23.8, -4.13) * mm});
            skLineSegment(sketch, "E289", {"start": v(-23.8, -4.13) * mm, "end": v(-23.82, -4.15) * mm});
            skLineSegment(sketch, "E290", {"start": v(-23.82, -4.15) * mm, "end": v(-23.83, -4.16) * mm});
            skLineSegment(sketch, "E291", {"start": v(-23.83, -4.16) * mm, "end": v(-23.83, -4.18) * mm});
            skLineSegment(sketch, "E292", {"start": v(-23.83, -4.18) * mm, "end": v(-23.84, -4.2) * mm});
            skLineSegment(sketch, "E293", {"start": v(-23.84, -4.2) * mm, "end": v(-23.85, -4.21) * mm});
            skLineSegment(sketch, "E294", {"start": v(-23.85, -4.21) * mm, "end": v(-23.85, -4.23) * mm});
            skLineSegment(sketch, "E295", {"start": v(-23.85, -4.23) * mm, "end": v(-23.85, -4.25) * mm});
            skLineSegment(sketch, "E296", {"start": v(-23.85, -4.25) * mm, "end": v(-23.86, -4.27) * mm});
            skLineSegment(sketch, "E297", {"start": v(-23.86, -4.27) * mm, "end": v(-23.86, -4.29) * mm});
            skLineSegment(sketch, "E298", {"start": v(-23.86, -4.29) * mm, "end": v(-23.86, -4.3) * mm});
            skLineSegment(sketch, "E299", {"start": v(-23.86, -4.3) * mm, "end": v(-23.85, -4.32) * mm});
            skLineSegment(sketch, "E300", {"start": v(-23.85, -4.32) * mm, "end": v(-23.85, -4.34) * mm});
            skLineSegment(sketch, "E301", {"start": v(-23.85, -4.34) * mm, "end": v(-23.84, -4.36) * mm});
            skLineSegment(sketch, "E302", {"start": v(-23.84, -4.36) * mm, "end": v(-23.84, -4.38) * mm});
            skLineSegment(sketch, "E303", {"start": v(-23.84, -4.38) * mm, "end": v(-23.83, -4.4) * mm});
            skLineSegment(sketch, "E304", {"start": v(-23.83, -4.4) * mm, "end": v(-23.82, -4.42) * mm});
            skLineSegment(sketch, "E305", {"start": v(-23.82, -4.42) * mm, "end": v(-23.81, -4.44) * mm});
            skLineSegment(sketch, "E306", {"start": v(-23.81, -4.44) * mm, "end": v(-23.8, -4.45) * mm});
            skLineSegment(sketch, "E307", {"start": v(-23.8, -4.45) * mm, "end": v(-23.8, -4.47) * mm});
            skLineSegment(sketch, "E308", {"start": v(-23.8, -4.47) * mm, "end": v(-23.78, -4.48) * mm});
            skLineSegment(sketch, "E309", {"start": v(-23.78, -4.48) * mm, "end": v(-23.76, -4.5) * mm});
            skLineSegment(sketch, "E310", {"start": v(-23.76, -4.5) * mm, "end": v(-23.73, -4.53) * mm});
            skLineSegment(sketch, "E311", {"start": v(-23.73, -4.53) * mm, "end": v(-23.7, -4.55) * mm});
            skLineSegment(sketch, "E312", {"start": v(-23.7, -4.55) * mm, "end": v(-23.58, -4.62) * mm});
            skLineSegment(sketch, "E313", {"start": v(-23.58, -4.62) * mm, "end": v(-23.42, -4.7) * mm});
            skLineSegment(sketch, "E314", {"start": v(-23.42, -4.7) * mm, "end": v(-19.6, -6.6) * mm});
            skLineSegment(sketch, "E315", {"start": v(-19.6, -6.6) * mm, "end": v(-18.6, -7.09) * mm});
            skLineSegment(sketch, "E316", {"start": v(-18.6, -7.09) * mm, "end": v(-17.5, -7.65) * mm});
            skLineSegment(sketch, "E317", {"start": v(-17.5, -7.65) * mm, "end": v(-16.7, -8.03) * mm});
            skLineSegment(sketch, "E318", {"start": v(-16.7, -8.03) * mm, "end": v(-16.68, -8.04) * mm});
            skLineSegment(sketch, "E319", {"start": v(-16.68, -8.04) * mm, "end": v(-16.66, -8.05) * mm});
            skLineSegment(sketch, "E320", {"start": v(-16.66, -8.05) * mm, "end": v(-16.64, -8.06) * mm});
            skLineSegment(sketch, "E321", {"start": v(-16.64, -8.06) * mm, "end": v(-16.62, -8.06) * mm});
            skLineSegment(sketch, "E322", {"start": v(-16.62, -8.06) * mm, "end": v(-16.6, -8.07) * mm});
            skLineSegment(sketch, "E323", {"start": v(-16.6, -8.07) * mm, "end": v(-16.58, -8.07) * mm});
            skLineSegment(sketch, "E324", {"start": v(-16.58, -8.07) * mm, "end": v(-16.56, -8.07) * mm});
            skLineSegment(sketch, "E325", {"start": v(-16.56, -8.07) * mm, "end": v(-16.54, -8.07) * mm});
            skLineSegment(sketch, "E326", {"start": v(-16.54, -8.07) * mm, "end": v(-16.52, -8.08) * mm});
            skLineSegment(sketch, "E327", {"start": v(-16.52, -8.08) * mm, "end": v(-16.48, -8.07) * mm});
            skLineSegment(sketch, "E328", {"start": v(-16.48, -8.07) * mm, "end": v(-16.44, -8.07) * mm});
            skLineSegment(sketch, "E329", {"start": v(-16.44, -8.07) * mm, "end": v(-16.4, -8.06) * mm});
            skLineSegment(sketch, "E330", {"start": v(-16.4, -8.06) * mm, "end": v(-16.32, -8.04) * mm});
            skLineSegment(sketch, "E331", {"start": v(-16.32, -8.04) * mm, "end": v(-16.14, -7.96) * mm});
            skLineSegment(sketch, "E332", {"start": v(-16.14, -7.96) * mm, "end": v(-13.76, -6.78) * mm});
            skLineSegment(sketch, "E333", {"start": v(-13.76, -6.78) * mm, "end": v(-9.85, -4.84) * mm});
            skLineSegment(sketch, "E334", {"start": v(-9.4, -3.99) * mm, "end": v(-9.57, -3.89) * mm});
            skLineSegment(sketch, "E335", {"start": v(-9.57, -3.89) * mm, "end": v(-10.59, -3.4) * mm});
            skLineSegment(sketch, "E336", {"start": v(-10.59, -3.4) * mm, "end": v(-10.6, -0.33) * mm});
            skLineSegment(sketch, "E337", {"start": v(-10.6, -0.33) * mm, "end": v(-13.15, -0.33) * mm});
            skLineSegment(sketch, "E338", {"start": v(-26.34, -4.98) * mm, "end": v(-25.3, -4.97) * mm});
            skLineSegment(sketch, "E339", {"start": v(-25.3, -4.97) * mm, "end": v(-25.28, -6.53) * mm});
            skLineSegment(sketch, "E340", {"start": v(-25.28, -6.53) * mm, "end": v(-26.11, -6.52) * mm});
            skLineSegment(sketch, "E341", {"start": v(-26.11, -6.52) * mm, "end": v(-26.27, -6.5) * mm});
            skLineSegment(sketch, "E342", {"start": v(-26.27, -6.5) * mm, "end": v(-26.38, -6.49) * mm});
            skLineSegment(sketch, "E343", {"start": v(-26.38, -6.49) * mm, "end": v(-26.4, -6.47) * mm});
            skLineSegment(sketch, "E344", {"start": v(-26.4, -6.47) * mm, "end": v(-26.43, -6.45) * mm});
            skLineSegment(sketch, "E345", {"start": v(-26.43, -6.45) * mm, "end": v(-26.45, -6.43) * mm});
            skLineSegment(sketch, "E346", {"start": v(-26.45, -6.43) * mm, "end": v(-26.47, -6.41) * mm});
            skLineSegment(sketch, "E347", {"start": v(-26.47, -6.41) * mm, "end": v(-26.49, -6.39) * mm});
            skLineSegment(sketch, "E348", {"start": v(-26.49, -6.39) * mm, "end": v(-26.5, -6.37) * mm});
            skLineSegment(sketch, "E349", {"start": v(-26.5, -6.37) * mm, "end": v(-26.52, -6.34) * mm});
            skLineSegment(sketch, "E350", {"start": v(-26.52, -6.34) * mm, "end": v(-26.54, -6.32) * mm});
            skLineSegment(sketch, "E351", {"start": v(-26.54, -6.32) * mm, "end": v(-26.55, -6.29) * mm});
            skLineSegment(sketch, "E352", {"start": v(-26.55, -6.29) * mm, "end": v(-26.56, -6.26) * mm});
            skLineSegment(sketch, "E353", {"start": v(-26.56, -6.26) * mm, "end": v(-26.57, -6.23) * mm});
            skLineSegment(sketch, "E354", {"start": v(-26.57, -6.23) * mm, "end": v(-26.58, -6.2) * mm});
            skLineSegment(sketch, "E355", {"start": v(-26.58, -6.2) * mm, "end": v(-26.59, -6.18) * mm});
            skLineSegment(sketch, "E356", {"start": v(-26.59, -6.18) * mm, "end": v(-26.6, -6.15) * mm});
            skLineSegment(sketch, "E357", {"start": v(-26.6, -6.15) * mm, "end": v(-26.6, -6.09) * mm});
            skLineSegment(sketch, "E358", {"start": v(-26.6, -6.09) * mm, "end": v(-26.62, -6.03) * mm});
            skLineSegment(sketch, "E359", {"start": v(-26.62, -6.03) * mm, "end": v(-26.62, -5.9) * mm});
            skLineSegment(sketch, "E360", {"start": v(-26.62, -5.9) * mm, "end": v(-26.63, -5.75) * mm});
            skLineSegment(sketch, "E361", {"start": v(-26.63, -5.75) * mm, "end": v(-26.63, -5.7) * mm});
            skLineSegment(sketch, "E362", {"start": v(-26.63, -5.7) * mm, "end": v(-26.63, -5.62) * mm});
            skLineSegment(sketch, "E363", {"start": v(-26.63, -5.62) * mm, "end": v(-26.62, -5.5) * mm});
            skLineSegment(sketch, "E364", {"start": v(-26.62, -5.5) * mm, "end": v(-26.6, -5.42) * mm});
            skLineSegment(sketch, "E365", {"start": v(-26.6, -5.42) * mm, "end": v(-26.6, -5.36) * mm});
            skLineSegment(sketch, "E366", {"start": v(-26.6, -5.36) * mm, "end": v(-26.58, -5.3) * mm});
            skLineSegment(sketch, "E367", {"start": v(-26.58, -5.3) * mm, "end": v(-26.58, -5.28) * mm});
            skLineSegment(sketch, "E368", {"start": v(-26.58, -5.28) * mm, "end": v(-26.57, -5.25) * mm});
            skLineSegment(sketch, "E369", {"start": v(-26.57, -5.25) * mm, "end": v(-26.56, -5.23) * mm});
            skLineSegment(sketch, "E370", {"start": v(-26.56, -5.23) * mm, "end": v(-26.55, -5.2) * mm});
            skLineSegment(sketch, "E371", {"start": v(-26.55, -5.2) * mm, "end": v(-26.53, -5.18) * mm});
            skLineSegment(sketch, "E372", {"start": v(-26.53, -5.18) * mm, "end": v(-26.52, -5.15) * mm});
            skLineSegment(sketch, "E373", {"start": v(-26.52, -5.15) * mm, "end": v(-26.5, -5.13) * mm});
            skLineSegment(sketch, "E374", {"start": v(-26.5, -5.13) * mm, "end": v(-26.5, -5.1) * mm});
            skLineSegment(sketch, "E375", {"start": v(-26.5, -5.1) * mm, "end": v(-26.47, -5.09) * mm});
            skLineSegment(sketch, "E376", {"start": v(-26.47, -5.09) * mm, "end": v(-26.46, -5.07) * mm});
            skLineSegment(sketch, "E377", {"start": v(-26.46, -5.07) * mm, "end": v(-26.44, -5.05) * mm});
            skLineSegment(sketch, "E378", {"start": v(-26.44, -5.05) * mm, "end": v(-26.42, -5.03) * mm});
            skLineSegment(sketch, "E379", {"start": v(-26.42, -5.03) * mm, "end": v(-26.4, -5.01) * mm});
            skLineSegment(sketch, "E380", {"start": v(-26.4, -5.01) * mm, "end": v(-26.37, -5) * mm});
            skLineSegment(sketch, "E381", {"start": v(-26.37, -5) * mm, "end": v(-26.34, -4.98) * mm});
            skLineSegment(sketch, "E382", {"start": v(-7.72, -4.97) * mm, "end": v(-7.68, -4.98) * mm});
            skLineSegment(sketch, "E383", {"start": v(-7.68, -4.98) * mm, "end": v(-7.64, -4.98) * mm});
            skLineSegment(sketch, "E384", {"start": v(-7.64, -4.98) * mm, "end": v(-7.6, -4.98) * mm});
            skLineSegment(sketch, "E385", {"start": v(-7.6, -4.98) * mm, "end": v(-7.55, -4.98) * mm});
            skLineSegment(sketch, "E386", {"start": v(-7.55, -4.98) * mm, "end": v(-7.5, -4.98) * mm});
            skLineSegment(sketch, "E387", {"start": v(-7.5, -4.98) * mm, "end": v(-7.41, -4.97) * mm});
            skLineSegment(sketch, "E388", {"start": v(-7.41, -4.97) * mm, "end": v(-7.13, -4.95) * mm});
            skLineSegment(sketch, "E389", {"start": v(-7.13, -4.95) * mm, "end": v(-7.09, -4.94) * mm});
            skLineSegment(sketch, "E390", {"start": v(-7.09, -4.94) * mm, "end": v(-7.04, -4.94) * mm});
            skLineSegment(sketch, "E391", {"start": v(-7.04, -4.94) * mm, "end": v(-7, -4.94) * mm});
            skLineSegment(sketch, "E392", {"start": v(-7, -4.94) * mm, "end": v(-6.95, -4.94) * mm});
            skLineSegment(sketch, "E393", {"start": v(-6.95, -4.94) * mm, "end": v(-6.9, -4.94) * mm});
            skLineSegment(sketch, "E394", {"start": v(-6.9, -4.94) * mm, "end": v(-6.86, -4.95) * mm});
            skLineSegment(sketch, "E395", {"start": v(-6.86, -4.95) * mm, "end": v(-6.82, -4.95) * mm});
            skLineSegment(sketch, "E396", {"start": v(-6.82, -4.95) * mm, "end": v(-6.78, -4.96) * mm});
            skLineSegment(sketch, "E397", {"start": v(-6.78, -4.96) * mm, "end": v(-6.74, -4.97) * mm});
            skLineSegment(sketch, "E398", {"start": v(-6.74, -4.97) * mm, "end": v(-6.7, -4.99) * mm});
            skLineSegment(sketch, "E399", {"start": v(-6.7, -4.99) * mm, "end": v(-6.66, -5) * mm});
            skLineSegment(sketch, "E400", {"start": v(-6.66, -5) * mm, "end": v(-6.62, -5.03) * mm});
            skLineSegment(sketch, "E401", {"start": v(-6.62, -5.03) * mm, "end": v(-6.58, -5.05) * mm});
            skLineSegment(sketch, "E402", {"start": v(-6.58, -5.05) * mm, "end": v(-6.55, -5.08) * mm});
            skLineSegment(sketch, "E403", {"start": v(-6.55, -5.08) * mm, "end": v(-6.52, -5.1) * mm});
            skLineSegment(sketch, "E404", {"start": v(-6.52, -5.1) * mm, "end": v(-6.48, -5.14) * mm});
            skLineSegment(sketch, "E405", {"start": v(-6.48, -5.14) * mm, "end": v(-6.47, -5.18) * mm});
            skLineSegment(sketch, "E406", {"start": v(-6.47, -5.18) * mm, "end": v(-6.46, -5.21) * mm});
            skLineSegment(sketch, "E407", {"start": v(-6.46, -5.21) * mm, "end": v(-6.45, -5.24) * mm});
            skLineSegment(sketch, "E408", {"start": v(-6.45, -5.24) * mm, "end": v(-6.43, -5.31) * mm});
            skLineSegment(sketch, "E409", {"start": v(-6.43, -5.31) * mm, "end": v(-6.41, -5.38) * mm});
            skLineSegment(sketch, "E410", {"start": v(-6.41, -5.38) * mm, "end": v(-6.4, -5.45) * mm});
            skLineSegment(sketch, "E411", {"start": v(-6.4, -5.45) * mm, "end": v(-6.4, -5.52) * mm});
            skLineSegment(sketch, "E412", {"start": v(-6.4, -5.52) * mm, "end": v(-6.39, -5.59) * mm});
            skLineSegment(sketch, "E413", {"start": v(-6.39, -5.59) * mm, "end": v(-6.38, -5.7) * mm});
            skLineSegment(sketch, "E414", {"start": v(-6.38, -5.7) * mm, "end": v(-6.39, -5.83) * mm});
            skLineSegment(sketch, "E415", {"start": v(-6.39, -5.83) * mm, "end": v(-6.4, -6.08) * mm});
            skLineSegment(sketch, "E416", {"start": v(-6.4, -6.08) * mm, "end": v(-6.42, -6.15) * mm});
            skLineSegment(sketch, "E417", {"start": v(-6.42, -6.15) * mm, "end": v(-6.47, -6.3) * mm});
            skLineSegment(sketch, "E418", {"start": v(-6.47, -6.3) * mm, "end": v(-6.5, -6.36) * mm});
            skLineSegment(sketch, "E419", {"start": v(-6.5, -6.36) * mm, "end": v(-6.53, -6.4) * mm});
            skLineSegment(sketch, "E420", {"start": v(-6.53, -6.4) * mm, "end": v(-6.56, -6.43) * mm});
            skLineSegment(sketch, "E421", {"start": v(-6.56, -6.43) * mm, "end": v(-6.59, -6.46) * mm});
            skLineSegment(sketch, "E422", {"start": v(-6.59, -6.46) * mm, "end": v(-6.61, -6.47) * mm});
            skLineSegment(sketch, "E423", {"start": v(-6.61, -6.47) * mm, "end": v(-6.64, -6.49) * mm});
            skLineSegment(sketch, "E424", {"start": v(-6.64, -6.49) * mm, "end": v(-6.67, -6.5) * mm});
            skLineSegment(sketch, "E425", {"start": v(-6.67, -6.5) * mm, "end": v(-7.74, -6.53) * mm});
            skLineSegment(sketch, "E426", {"start": v(-7.74, -6.53) * mm, "end": v(-7.72, -4.97) * mm});
            skLineSegment(sketch, "E427", {"start": v(-26.35, -7.32) * mm, "end": v(-25.28, -7.3) * mm});
            skLineSegment(sketch, "E428", {"start": v(-25.28, -7.3) * mm, "end": v(-25.28, -8.87) * mm});
            skLineSegment(sketch, "E429", {"start": v(-25.28, -8.87) * mm, "end": v(-26.35, -8.85) * mm});
            skLineSegment(sketch, "E430", {"start": v(-26.35, -8.85) * mm, "end": v(-26.5, -8.7) * mm});
            skLineSegment(sketch, "E431", {"start": v(-26.5, -8.7) * mm, "end": v(-26.55, -8.62) * mm});
            skLineSegment(sketch, "E432", {"start": v(-26.55, -8.62) * mm, "end": v(-26.57, -8.57) * mm});
            skLineSegment(sketch, "E433", {"start": v(-26.57, -8.57) * mm, "end": v(-26.6, -8.52) * mm});
            skLineSegment(sketch, "E434", {"start": v(-26.6, -8.52) * mm, "end": v(-26.6, -8.47) * mm});
            skLineSegment(sketch, "E435", {"start": v(-26.6, -8.47) * mm, "end": v(-26.6, -8.45) * mm});
            skLineSegment(sketch, "E436", {"start": v(-26.6, -8.45) * mm, "end": v(-26.61, -8.37) * mm});
            skLineSegment(sketch, "E437", {"start": v(-26.61, -8.37) * mm, "end": v(-26.63, -8.2) * mm});
            skLineSegment(sketch, "E438", {"start": v(-26.63, -8.2) * mm, "end": v(-26.63, -8.08) * mm});
            skLineSegment(sketch, "E439", {"start": v(-26.63, -8.08) * mm, "end": v(-26.64, -8) * mm});
            skLineSegment(sketch, "E440", {"start": v(-26.64, -8) * mm, "end": v(-26.64, -7.95) * mm});
            skLineSegment(sketch, "E441", {"start": v(-26.64, -7.95) * mm, "end": v(-26.63, -7.9) * mm});
            skLineSegment(sketch, "E442", {"start": v(-26.63, -7.9) * mm, "end": v(-26.63, -7.86) * mm});
            skLineSegment(sketch, "E443", {"start": v(-26.63, -7.86) * mm, "end": v(-26.63, -7.82) * mm});
            skLineSegment(sketch, "E444", {"start": v(-26.63, -7.82) * mm, "end": v(-26.62, -7.78) * mm});
            skLineSegment(sketch, "E445", {"start": v(-26.62, -7.78) * mm, "end": v(-26.61, -7.74) * mm});
            skLineSegment(sketch, "E446", {"start": v(-26.61, -7.74) * mm, "end": v(-26.6, -7.7) * mm});
            skLineSegment(sketch, "E447", {"start": v(-26.6, -7.7) * mm, "end": v(-26.6, -7.66) * mm});
            skLineSegment(sketch, "E448", {"start": v(-26.6, -7.66) * mm, "end": v(-26.58, -7.62) * mm});
            skLineSegment(sketch, "E449", {"start": v(-26.58, -7.62) * mm, "end": v(-26.56, -7.58) * mm});
            skLineSegment(sketch, "E450", {"start": v(-26.56, -7.58) * mm, "end": v(-26.55, -7.54) * mm});
            skLineSegment(sketch, "E451", {"start": v(-26.55, -7.54) * mm, "end": v(-26.53, -7.5) * mm});
            skLineSegment(sketch, "E452", {"start": v(-26.53, -7.5) * mm, "end": v(-26.5, -7.47) * mm});
            skLineSegment(sketch, "E453", {"start": v(-26.5, -7.47) * mm, "end": v(-26.48, -7.44) * mm});
            skLineSegment(sketch, "E454", {"start": v(-26.48, -7.44) * mm, "end": v(-26.45, -7.4) * mm});
            skLineSegment(sketch, "E455", {"start": v(-26.45, -7.4) * mm, "end": v(-26.42, -7.38) * mm});
            skLineSegment(sketch, "E456", {"start": v(-26.42, -7.38) * mm, "end": v(-26.39, -7.35) * mm});
            skLineSegment(sketch, "E457", {"start": v(-26.39, -7.35) * mm, "end": v(-26.35, -7.32) * mm});
            skLineSegment(sketch, "E458", {"start": v(-7.73, -7.3) * mm, "end": v(-6.66, -7.32) * mm});
            skLineSegment(sketch, "E459", {"start": v(-6.66, -7.32) * mm, "end": v(-6.53, -7.44) * mm});
            skLineSegment(sketch, "E460", {"start": v(-6.53, -7.44) * mm, "end": v(-6.47, -7.53) * mm});
            skLineSegment(sketch, "E461", {"start": v(-6.47, -7.53) * mm, "end": v(-6.44, -7.58) * mm});
            skLineSegment(sketch, "E462", {"start": v(-6.44, -7.58) * mm, "end": v(-6.43, -7.63) * mm});
            skLineSegment(sketch, "E463", {"start": v(-6.43, -7.63) * mm, "end": v(-6.41, -7.68) * mm});
            skLineSegment(sketch, "E464", {"start": v(-6.41, -7.68) * mm, "end": v(-6.4, -7.7) * mm});
            skLineSegment(sketch, "E465", {"start": v(-6.4, -7.7) * mm, "end": v(-6.4, -7.79) * mm});
            skLineSegment(sketch, "E466", {"start": v(-6.4, -7.79) * mm, "end": v(-6.39, -7.96) * mm});
            skLineSegment(sketch, "E467", {"start": v(-6.39, -7.96) * mm, "end": v(-6.38, -8.09) * mm});
            skLineSegment(sketch, "E468", {"start": v(-6.38, -8.09) * mm, "end": v(-6.38, -8.17) * mm});
            skLineSegment(sketch, "E469", {"start": v(-6.38, -8.17) * mm, "end": v(-6.38, -8.22) * mm});
            skLineSegment(sketch, "E470", {"start": v(-6.38, -8.22) * mm, "end": v(-6.38, -8.26) * mm});
            skLineSegment(sketch, "E471", {"start": v(-6.38, -8.26) * mm, "end": v(-6.38, -8.3) * mm});
            skLineSegment(sketch, "E472", {"start": v(-6.38, -8.3) * mm, "end": v(-6.39, -8.34) * mm});
            skLineSegment(sketch, "E473", {"start": v(-6.39, -8.34) * mm, "end": v(-6.4, -8.39) * mm});
            skLineSegment(sketch, "E474", {"start": v(-6.4, -8.39) * mm, "end": v(-6.4, -8.43) * mm});
            skLineSegment(sketch, "E475", {"start": v(-6.4, -8.43) * mm, "end": v(-6.4, -8.47) * mm});
            skLineSegment(sketch, "E476", {"start": v(-6.4, -8.47) * mm, "end": v(-6.42, -8.5) * mm});
            skLineSegment(sketch, "E477", {"start": v(-6.42, -8.5) * mm, "end": v(-6.43, -8.55) * mm});
            skLineSegment(sketch, "E478", {"start": v(-6.43, -8.55) * mm, "end": v(-6.45, -8.58) * mm});
            skLineSegment(sketch, "E479", {"start": v(-6.45, -8.58) * mm, "end": v(-6.47, -8.62) * mm});
            skLineSegment(sketch, "E480", {"start": v(-6.47, -8.62) * mm, "end": v(-6.49, -8.66) * mm});
            skLineSegment(sketch, "E481", {"start": v(-6.49, -8.66) * mm, "end": v(-6.5, -8.7) * mm});
            skLineSegment(sketch, "E482", {"start": v(-6.5, -8.7) * mm, "end": v(-6.53, -8.73) * mm});
            skLineSegment(sketch, "E483", {"start": v(-6.53, -8.73) * mm, "end": v(-6.56, -8.76) * mm});
            skLineSegment(sketch, "E484", {"start": v(-6.56, -8.76) * mm, "end": v(-6.6, -8.79) * mm});
            skLineSegment(sketch, "E485", {"start": v(-6.6, -8.79) * mm, "end": v(-6.62, -8.82) * mm});
            skLineSegment(sketch, "E486", {"start": v(-6.62, -8.82) * mm, "end": v(-6.66, -8.85) * mm});
            skLineSegment(sketch, "E487", {"start": v(-6.66, -8.85) * mm, "end": v(-7.73, -8.87) * mm});
            skLineSegment(sketch, "E488", {"start": v(-7.73, -8.87) * mm, "end": v(-7.73, -7.3) * mm});
            skLineSegment(sketch, "E489", {"start": v(-26.38, -9.67) * mm, "end": v(-26.27, -9.66) * mm});
            skLineSegment(sketch, "E490", {"start": v(-26.27, -9.66) * mm, "end": v(-26.08, -9.64) * mm});
            skLineSegment(sketch, "E491", {"start": v(-26.08, -9.64) * mm, "end": v(-25.28, -9.63) * mm});
            skLineSegment(sketch, "E492", {"start": v(-25.28, -9.63) * mm, "end": v(-25.3, -11.2) * mm});
            skLineSegment(sketch, "E493", {"start": v(-25.3, -11.2) * mm, "end": v(-26.03, -11.2) * mm});
            skLineSegment(sketch, "E494", {"start": v(-26.03, -11.2) * mm, "end": v(-26.17, -11.2) * mm});
            skLineSegment(sketch, "E495", {"start": v(-26.17, -11.2) * mm, "end": v(-26.27, -11.19) * mm});
            skLineSegment(sketch, "E496", {"start": v(-26.27, -11.19) * mm, "end": v(-26.3, -11.18) * mm});
            skLineSegment(sketch, "E497", {"start": v(-26.3, -11.18) * mm, "end": v(-26.34, -11.17) * mm});
            skLineSegment(sketch, "E498", {"start": v(-26.34, -11.17) * mm, "end": v(-26.36, -11.16) * mm});
            skLineSegment(sketch, "E499", {"start": v(-26.36, -11.16) * mm, "end": v(-26.39, -11.15) * mm});
            skLineSegment(sketch, "E500", {"start": v(-26.39, -11.15) * mm, "end": v(-26.41, -11.13) * mm});
            skLineSegment(sketch, "E501", {"start": v(-26.41, -11.13) * mm, "end": v(-26.43, -11.11) * mm});
            skLineSegment(sketch, "E502", {"start": v(-26.43, -11.11) * mm, "end": v(-26.46, -11.1) * mm});
            skLineSegment(sketch, "E503", {"start": v(-26.46, -11.1) * mm, "end": v(-26.47, -11.08) * mm});
            skLineSegment(sketch, "E504", {"start": v(-26.47, -11.08) * mm, "end": v(-26.5, -11.05) * mm});
            skLineSegment(sketch, "E505", {"start": v(-26.5, -11.05) * mm, "end": v(-26.5, -11.03) * mm});
            skLineSegment(sketch, "E506", {"start": v(-26.5, -11.03) * mm, "end": v(-26.52, -11) * mm});
            skLineSegment(sketch, "E507", {"start": v(-26.52, -11) * mm, "end": v(-26.54, -10.98) * mm});
            skLineSegment(sketch, "E508", {"start": v(-26.54, -10.98) * mm, "end": v(-26.55, -10.95) * mm});
            skLineSegment(sketch, "E509", {"start": v(-26.55, -10.95) * mm, "end": v(-26.56, -10.93) * mm});
            skLineSegment(sketch, "E510", {"start": v(-26.56, -10.93) * mm, "end": v(-26.57, -10.9) * mm});
            skLineSegment(sketch, "E511", {"start": v(-26.57, -10.9) * mm, "end": v(-26.58, -10.87) * mm});
            skLineSegment(sketch, "E512", {"start": v(-26.58, -10.87) * mm, "end": v(-26.59, -10.84) * mm});
            skLineSegment(sketch, "E513", {"start": v(-26.59, -10.84) * mm, "end": v(-26.6, -10.78) * mm});
            skLineSegment(sketch, "E514", {"start": v(-26.6, -10.78) * mm, "end": v(-26.61, -10.72) * mm});
            skLineSegment(sketch, "E515", {"start": v(-26.61, -10.72) * mm, "end": v(-26.62, -10.63) * mm});
            skLineSegment(sketch, "E516", {"start": v(-26.62, -10.63) * mm, "end": v(-26.63, -10.55) * mm});
            skLineSegment(sketch, "E517", {"start": v(-26.63, -10.55) * mm, "end": v(-26.63, -10.5) * mm});
            skLineSegment(sketch, "E518", {"start": v(-26.63, -10.5) * mm, "end": v(-26.63, -10.47) * mm});
            skLineSegment(sketch, "E519", {"start": v(-26.63, -10.47) * mm, "end": v(-26.63, -10.38) * mm});
            skLineSegment(sketch, "E520", {"start": v(-26.63, -10.38) * mm, "end": v(-26.62, -10.23) * mm});
            skLineSegment(sketch, "E521", {"start": v(-26.62, -10.23) * mm, "end": v(-26.62, -10.14) * mm});
            skLineSegment(sketch, "E522", {"start": v(-26.62, -10.14) * mm, "end": v(-26.6, -10.08) * mm});
            skLineSegment(sketch, "E523", {"start": v(-26.6, -10.08) * mm, "end": v(-26.6, -10.02) * mm});
            skLineSegment(sketch, "E524", {"start": v(-26.6, -10.02) * mm, "end": v(-26.59, -9.99) * mm});
            skLineSegment(sketch, "E525", {"start": v(-26.59, -9.99) * mm, "end": v(-26.58, -9.96) * mm});
            skLineSegment(sketch, "E526", {"start": v(-26.58, -9.96) * mm, "end": v(-26.57, -9.93) * mm});
            skLineSegment(sketch, "E527", {"start": v(-26.57, -9.93) * mm, "end": v(-26.56, -9.9) * mm});
            skLineSegment(sketch, "E528", {"start": v(-26.56, -9.9) * mm, "end": v(-26.55, -9.87) * mm});
            skLineSegment(sketch, "E529", {"start": v(-26.55, -9.87) * mm, "end": v(-26.54, -9.85) * mm});
            skLineSegment(sketch, "E530", {"start": v(-26.54, -9.85) * mm, "end": v(-26.52, -9.82) * mm});
            skLineSegment(sketch, "E531", {"start": v(-26.52, -9.82) * mm, "end": v(-26.5, -9.8) * mm});
            skLineSegment(sketch, "E532", {"start": v(-26.5, -9.8) * mm, "end": v(-26.49, -9.77) * mm});
            skLineSegment(sketch, "E533", {"start": v(-26.49, -9.77) * mm, "end": v(-26.47, -9.75) * mm});
            skLineSegment(sketch, "E534", {"start": v(-26.47, -9.75) * mm, "end": v(-26.45, -9.73) * mm});
            skLineSegment(sketch, "E535", {"start": v(-26.45, -9.73) * mm, "end": v(-26.43, -9.71) * mm});
            skLineSegment(sketch, "E536", {"start": v(-26.43, -9.71) * mm, "end": v(-26.4, -9.7) * mm});
            skLineSegment(sketch, "E537", {"start": v(-26.4, -9.7) * mm, "end": v(-26.38, -9.67) * mm});
            skLineSegment(sketch, "E538", {"start": v(-7.73, -9.64) * mm, "end": v(-6.54, -9.67) * mm});
            skLineSegment(sketch, "E539", {"start": v(-6.54, -9.67) * mm, "end": v(-6.51, -9.75) * mm});
            skLineSegment(sketch, "E540", {"start": v(-6.51, -9.75) * mm, "end": v(-6.48, -9.83) * mm});
            skLineSegment(sketch, "E541", {"start": v(-6.48, -9.83) * mm, "end": v(-6.46, -9.9) * mm});
            skLineSegment(sketch, "E542", {"start": v(-6.46, -9.9) * mm, "end": v(-6.44, -9.99) * mm});
            skLineSegment(sketch, "E543", {"start": v(-6.44, -9.99) * mm, "end": v(-6.42, -10.07) * mm});
            skLineSegment(sketch, "E544", {"start": v(-6.42, -10.07) * mm, "end": v(-6.4, -10.15) * mm});
            skLineSegment(sketch, "E545", {"start": v(-6.4, -10.15) * mm, "end": v(-6.4, -10.23) * mm});
            skLineSegment(sketch, "E546", {"start": v(-6.4, -10.23) * mm, "end": v(-6.39, -10.32) * mm});
            skLineSegment(sketch, "E547", {"start": v(-6.39, -10.32) * mm, "end": v(-6.38, -10.4) * mm});
            skLineSegment(sketch, "E548", {"start": v(-6.38, -10.4) * mm, "end": v(-6.38, -10.44) * mm});
            skLineSegment(sketch, "E549", {"start": v(-6.38, -10.44) * mm, "end": v(-6.38, -10.48) * mm});
            skLineSegment(sketch, "E550", {"start": v(-6.38, -10.48) * mm, "end": v(-6.38, -10.53) * mm});
            skLineSegment(sketch, "E551", {"start": v(-6.38, -10.53) * mm, "end": v(-6.39, -10.57) * mm});
            skLineSegment(sketch, "E552", {"start": v(-6.39, -10.57) * mm, "end": v(-6.39, -10.6) * mm});
            skLineSegment(sketch, "E553", {"start": v(-6.39, -10.6) * mm, "end": v(-6.4, -10.65) * mm});
            skLineSegment(sketch, "E554", {"start": v(-6.4, -10.65) * mm, "end": v(-6.4, -10.7) * mm});
            skLineSegment(sketch, "E555", {"start": v(-6.4, -10.7) * mm, "end": v(-6.4, -10.73) * mm});
            skLineSegment(sketch, "E556", {"start": v(-6.4, -10.73) * mm, "end": v(-6.41, -10.77) * mm});
            skLineSegment(sketch, "E557", {"start": v(-6.41, -10.77) * mm, "end": v(-6.42, -10.82) * mm});
            skLineSegment(sketch, "E558", {"start": v(-6.42, -10.82) * mm, "end": v(-6.43, -10.86) * mm});
            skLineSegment(sketch, "E559", {"start": v(-6.43, -10.86) * mm, "end": v(-6.45, -10.92) * mm});
            skLineSegment(sketch, "E560", {"start": v(-6.45, -10.92) * mm, "end": v(-6.47, -10.97) * mm});
            skLineSegment(sketch, "E561", {"start": v(-6.47, -10.97) * mm, "end": v(-6.5, -11.03) * mm});
            skLineSegment(sketch, "E562", {"start": v(-6.5, -11.03) * mm, "end": v(-6.53, -11.07) * mm});
            skLineSegment(sketch, "E563", {"start": v(-6.53, -11.07) * mm, "end": v(-6.56, -11.1) * mm});
            skLineSegment(sketch, "E564", {"start": v(-6.56, -11.1) * mm, "end": v(-6.58, -11.12) * mm});
            skLineSegment(sketch, "E565", {"start": v(-6.58, -11.12) * mm, "end": v(-6.6, -11.14) * mm});
            skLineSegment(sketch, "E566", {"start": v(-6.6, -11.14) * mm, "end": v(-6.64, -11.15) * mm});
            skLineSegment(sketch, "E567", {"start": v(-6.64, -11.15) * mm, "end": v(-6.66, -11.17) * mm});
            skLineSegment(sketch, "E568", {"start": v(-6.66, -11.17) * mm, "end": v(-6.7, -11.18) * mm});
            skLineSegment(sketch, "E569", {"start": v(-6.7, -11.18) * mm, "end": v(-6.7, -11.18) * mm});
            skLineSegment(sketch, "E570", {"start": v(-6.7, -11.18) * mm, "end": v(-7.72, -11.2) * mm});
            skLineSegment(sketch, "E571", {"start": v(-7.72, -11.2) * mm, "end": v(-7.73, -9.64) * mm});
            skLineSegment(sketch, "E572", {"start": v(-26.47, -12.01) * mm, "end": v(-25.28, -11.98) * mm});
            skLineSegment(sketch, "E573", {"start": v(-25.28, -11.98) * mm, "end": v(-25.3, -13.53) * mm});
            skLineSegment(sketch, "E574", {"start": v(-25.3, -13.53) * mm, "end": v(-25.33, -13.53) * mm});
            skLineSegment(sketch, "E575", {"start": v(-25.33, -13.53) * mm, "end": v(-25.38, -13.52) * mm});
            skLineSegment(sketch, "E576", {"start": v(-25.38, -13.52) * mm, "end": v(-25.42, -13.52) * mm});
            skLineSegment(sketch, "E577", {"start": v(-25.42, -13.52) * mm, "end": v(-25.47, -13.52) * mm});
            skLineSegment(sketch, "E578", {"start": v(-25.47, -13.52) * mm, "end": v(-25.5, -13.52) * mm});
            skLineSegment(sketch, "E579", {"start": v(-25.5, -13.52) * mm, "end": v(-25.6, -13.53) * mm});
            skLineSegment(sketch, "E580", {"start": v(-25.6, -13.53) * mm, "end": v(-25.88, -13.56) * mm});
            skLineSegment(sketch, "E581", {"start": v(-25.88, -13.56) * mm, "end": v(-25.93, -13.56) * mm});
            skLineSegment(sketch, "E582", {"start": v(-25.93, -13.56) * mm, "end": v(-25.97, -13.56) * mm});
            skLineSegment(sketch, "E583", {"start": v(-25.97, -13.56) * mm, "end": v(-26.02, -13.56) * mm});
            skLineSegment(sketch, "E584", {"start": v(-26.02, -13.56) * mm, "end": v(-26.06, -13.56) * mm});
            skLineSegment(sketch, "E585", {"start": v(-26.06, -13.56) * mm, "end": v(-26.1, -13.56) * mm});
            skLineSegment(sketch, "E586", {"start": v(-26.1, -13.56) * mm, "end": v(-26.15, -13.56) * mm});
            skLineSegment(sketch, "E587", {"start": v(-26.15, -13.56) * mm, "end": v(-26.2, -13.55) * mm});
            skLineSegment(sketch, "E588", {"start": v(-26.2, -13.55) * mm, "end": v(-26.24, -13.54) * mm});
            skLineSegment(sketch, "E589", {"start": v(-26.24, -13.54) * mm, "end": v(-26.28, -13.53) * mm});
            skLineSegment(sketch, "E590", {"start": v(-26.28, -13.53) * mm, "end": v(-26.32, -13.52) * mm});
            skLineSegment(sketch, "E591", {"start": v(-26.32, -13.52) * mm, "end": v(-26.36, -13.5) * mm});
            skLineSegment(sketch, "E592", {"start": v(-26.36, -13.5) * mm, "end": v(-26.4, -13.48) * mm});
            skLineSegment(sketch, "E593", {"start": v(-26.4, -13.48) * mm, "end": v(-26.43, -13.45) * mm});
            skLineSegment(sketch, "E594", {"start": v(-26.43, -13.45) * mm, "end": v(-26.46, -13.43) * mm});
            skLineSegment(sketch, "E595", {"start": v(-26.46, -13.43) * mm, "end": v(-26.5, -13.4) * mm});
            skLineSegment(sketch, "E596", {"start": v(-26.5, -13.4) * mm, "end": v(-26.53, -13.36) * mm});
            skLineSegment(sketch, "E597", {"start": v(-26.53, -13.36) * mm, "end": v(-26.55, -13.31) * mm});
            skLineSegment(sketch, "E598", {"start": v(-26.55, -13.31) * mm, "end": v(-26.56, -13.27) * mm});
            skLineSegment(sketch, "E599", {"start": v(-26.56, -13.27) * mm, "end": v(-26.57, -13.22) * mm});
            skLineSegment(sketch, "E600", {"start": v(-26.57, -13.22) * mm, "end": v(-26.59, -13.18) * mm});
            skLineSegment(sketch, "E601", {"start": v(-26.59, -13.18) * mm, "end": v(-26.6, -13.13) * mm});
            skLineSegment(sketch, "E602", {"start": v(-26.6, -13.13) * mm, "end": v(-26.6, -13.08) * mm});
            skLineSegment(sketch, "E603", {"start": v(-26.6, -13.08) * mm, "end": v(-26.61, -13.04) * mm});
            skLineSegment(sketch, "E604", {"start": v(-26.61, -13.04) * mm, "end": v(-26.62, -12.99) * mm});
            skLineSegment(sketch, "E605", {"start": v(-26.62, -12.99) * mm, "end": v(-26.63, -12.94) * mm});
            skLineSegment(sketch, "E606", {"start": v(-26.63, -12.94) * mm, "end": v(-26.63, -12.9) * mm});
            skLineSegment(sketch, "E607", {"start": v(-26.63, -12.9) * mm, "end": v(-26.63, -12.85) * mm});
            skLineSegment(sketch, "E608", {"start": v(-26.63, -12.85) * mm, "end": v(-26.63, -12.8) * mm});
            skLineSegment(sketch, "E609", {"start": v(-26.63, -12.8) * mm, "end": v(-26.63, -12.75) * mm});
            skLineSegment(sketch, "E610", {"start": v(-26.63, -12.75) * mm, "end": v(-26.63, -12.7) * mm});
            skLineSegment(sketch, "E611", {"start": v(-26.63, -12.7) * mm, "end": v(-26.63, -12.66) * mm});
            skLineSegment(sketch, "E612", {"start": v(-26.63, -12.66) * mm, "end": v(-26.62, -12.6) * mm});
            skLineSegment(sketch, "E613", {"start": v(-26.62, -12.6) * mm, "end": v(-26.62, -12.56) * mm});
            skLineSegment(sketch, "E614", {"start": v(-26.62, -12.56) * mm, "end": v(-26.61, -12.51) * mm});
            skLineSegment(sketch, "E615", {"start": v(-26.61, -12.51) * mm, "end": v(-26.6, -12.47) * mm});
            skLineSegment(sketch, "E616", {"start": v(-26.6, -12.47) * mm, "end": v(-26.6, -12.42) * mm});
            skLineSegment(sketch, "E617", {"start": v(-26.6, -12.42) * mm, "end": v(-26.59, -12.37) * mm});
            skLineSegment(sketch, "E618", {"start": v(-26.59, -12.37) * mm, "end": v(-26.58, -12.33) * mm});
            skLineSegment(sketch, "E619", {"start": v(-26.58, -12.33) * mm, "end": v(-26.56, -12.28) * mm});
            skLineSegment(sketch, "E620", {"start": v(-26.56, -12.28) * mm, "end": v(-26.55, -12.23) * mm});
            skLineSegment(sketch, "E621", {"start": v(-26.55, -12.23) * mm, "end": v(-26.54, -12.19) * mm});
            skLineSegment(sketch, "E622", {"start": v(-26.54, -12.19) * mm, "end": v(-26.52, -12.14) * mm});
            skLineSegment(sketch, "E623", {"start": v(-26.52, -12.14) * mm, "end": v(-26.5, -12.1) * mm});
            skLineSegment(sketch, "E624", {"start": v(-26.5, -12.1) * mm, "end": v(-26.49, -12.05) * mm});
            skLineSegment(sketch, "E625", {"start": v(-26.49, -12.05) * mm, "end": v(-26.47, -12.01) * mm});
            skLineSegment(sketch, "E626", {"start": v(-7.73, -11.98) * mm, "end": v(-6.54, -12.01) * mm});
            skLineSegment(sketch, "E627", {"start": v(-6.54, -12.01) * mm, "end": v(-6.52, -12.06) * mm});
            skLineSegment(sketch, "E628", {"start": v(-6.52, -12.06) * mm, "end": v(-6.5, -12.1) * mm});
            skLineSegment(sketch, "E629", {"start": v(-6.5, -12.1) * mm, "end": v(-6.49, -12.16) * mm});
            skLineSegment(sketch, "E630", {"start": v(-6.49, -12.16) * mm, "end": v(-6.47, -12.2) * mm});
            skLineSegment(sketch, "E631", {"start": v(-6.47, -12.2) * mm, "end": v(-6.46, -12.26) * mm});
            skLineSegment(sketch, "E632", {"start": v(-6.46, -12.26) * mm, "end": v(-6.44, -12.31) * mm});
            skLineSegment(sketch, "E633", {"start": v(-6.44, -12.31) * mm, "end": v(-6.43, -12.37) * mm});
            skLineSegment(sketch, "E634", {"start": v(-6.43, -12.37) * mm, "end": v(-6.42, -12.42) * mm});
            skLineSegment(sketch, "E635", {"start": v(-6.42, -12.42) * mm, "end": v(-6.4, -12.48) * mm});
            skLineSegment(sketch, "E636", {"start": v(-6.4, -12.48) * mm, "end": v(-6.4, -12.53) * mm});
            skLineSegment(sketch, "E637", {"start": v(-6.4, -12.53) * mm, "end": v(-6.39, -12.59) * mm});
            skLineSegment(sketch, "E638", {"start": v(-6.39, -12.59) * mm, "end": v(-6.38, -12.64) * mm});
            skLineSegment(sketch, "E639", {"start": v(-6.38, -12.64) * mm, "end": v(-6.38, -12.7) * mm});
            skLineSegment(sketch, "E640", {"start": v(-6.38, -12.7) * mm, "end": v(-6.37, -12.75) * mm});
            skLineSegment(sketch, "E641", {"start": v(-6.37, -12.75) * mm, "end": v(-6.37, -12.8) * mm});
            skLineSegment(sketch, "E642", {"start": v(-6.37, -12.8) * mm, "end": v(-6.37, -12.86) * mm});
            skLineSegment(sketch, "E643", {"start": v(-6.37, -12.86) * mm, "end": v(-6.38, -12.91) * mm});
            skLineSegment(sketch, "E644", {"start": v(-6.38, -12.91) * mm, "end": v(-6.38, -12.97) * mm});
            skLineSegment(sketch, "E645", {"start": v(-6.38, -12.97) * mm, "end": v(-6.39, -13.02) * mm});
            skLineSegment(sketch, "E646", {"start": v(-6.39, -13.02) * mm, "end": v(-6.4, -13.07) * mm});
            skLineSegment(sketch, "E647", {"start": v(-6.4, -13.07) * mm, "end": v(-6.4, -13.12) * mm});
            skLineSegment(sketch, "E648", {"start": v(-6.4, -13.12) * mm, "end": v(-6.42, -13.17) * mm});
            skLineSegment(sketch, "E649", {"start": v(-6.42, -13.17) * mm, "end": v(-6.44, -13.22) * mm});
            skLineSegment(sketch, "E650", {"start": v(-6.44, -13.22) * mm, "end": v(-6.46, -13.27) * mm});
            skLineSegment(sketch, "E651", {"start": v(-6.46, -13.27) * mm, "end": v(-6.49, -13.32) * mm});
            skLineSegment(sketch, "E652", {"start": v(-6.49, -13.32) * mm, "end": v(-6.51, -13.36) * mm});
            skLineSegment(sketch, "E653", {"start": v(-6.51, -13.36) * mm, "end": v(-6.54, -13.4) * mm});
            skLineSegment(sketch, "E654", {"start": v(-6.54, -13.4) * mm, "end": v(-6.58, -13.45) * mm});
            skLineSegment(sketch, "E655", {"start": v(-6.58, -13.45) * mm, "end": v(-6.61, -13.49) * mm});
            skLineSegment(sketch, "E656", {"start": v(-6.61, -13.49) * mm, "end": v(-6.65, -13.5) * mm});
            skLineSegment(sketch, "E657", {"start": v(-6.65, -13.5) * mm, "end": v(-6.69, -13.5) * mm});
            skLineSegment(sketch, "E658", {"start": v(-6.69, -13.5) * mm, "end": v(-6.72, -13.52) * mm});
            skLineSegment(sketch, "E659", {"start": v(-6.72, -13.52) * mm, "end": v(-6.76, -13.52) * mm});
            skLineSegment(sketch, "E660", {"start": v(-6.76, -13.52) * mm, "end": v(-6.8, -13.53) * mm});
            skLineSegment(sketch, "E661", {"start": v(-6.8, -13.53) * mm, "end": v(-6.87, -13.54) * mm});
            skLineSegment(sketch, "E662", {"start": v(-6.87, -13.54) * mm, "end": v(-6.95, -13.55) * mm});
            skLineSegment(sketch, "E663", {"start": v(-6.95, -13.55) * mm, "end": v(-7.06, -13.55) * mm});
            skLineSegment(sketch, "E664", {"start": v(-7.06, -13.55) * mm, "end": v(-7.6, -13.53) * mm});
            skLineSegment(sketch, "E665", {"start": v(-7.6, -13.53) * mm, "end": v(-7.72, -13.53) * mm});
            skLineSegment(sketch, "E666", {"start": v(-7.72, -13.53) * mm, "end": v(-7.73, -11.98) * mm});
            skLineSegment(sketch, "E667", {"start": v(-20.77, -15.27) * mm, "end": v(-19.21, -15.27) * mm});
            skLineSegment(sketch, "E668", {"start": v(-19.21, -15.27) * mm, "end": v(-19.21, -16.13) * mm});
            skLineSegment(sketch, "E669", {"start": v(-19.21, -16.13) * mm, "end": v(-19.22, -16.27) * mm});
            skLineSegment(sketch, "E670", {"start": v(-19.22, -16.27) * mm, "end": v(-19.23, -16.29) * mm});
            skLineSegment(sketch, "E671", {"start": v(-19.23, -16.29) * mm, "end": v(-19.23, -16.3) * mm});
            skLineSegment(sketch, "E672", {"start": v(-19.23, -16.3) * mm, "end": v(-19.24, -16.32) * mm});
            skLineSegment(sketch, "E673", {"start": v(-19.24, -16.32) * mm, "end": v(-19.24, -16.34) * mm});
            skLineSegment(sketch, "E674", {"start": v(-19.24, -16.34) * mm, "end": v(-19.25, -16.35) * mm});
            skLineSegment(sketch, "E675", {"start": v(-19.25, -16.35) * mm, "end": v(-19.26, -16.37) * mm});
            skLineSegment(sketch, "E676", {"start": v(-19.26, -16.37) * mm, "end": v(-19.27, -16.38) * mm});
            skLineSegment(sketch, "E677", {"start": v(-19.27, -16.38) * mm, "end": v(-19.28, -16.4) * mm});
            skLineSegment(sketch, "E678", {"start": v(-19.28, -16.4) * mm, "end": v(-19.3, -16.41) * mm});
            skLineSegment(sketch, "E679", {"start": v(-19.3, -16.41) * mm, "end": v(-19.32, -16.43) * mm});
            skLineSegment(sketch, "E680", {"start": v(-19.32, -16.43) * mm, "end": v(-19.34, -16.46) * mm});
            skLineSegment(sketch, "E681", {"start": v(-19.34, -16.46) * mm, "end": v(-19.39, -16.49) * mm});
            skLineSegment(sketch, "E682", {"start": v(-19.39, -16.49) * mm, "end": v(-19.47, -16.53) * mm});
            skLineSegment(sketch, "E683", {"start": v(-19.47, -16.53) * mm, "end": v(-19.6, -16.58) * mm});
            skLineSegment(sketch, "E684", {"start": v(-19.6, -16.58) * mm, "end": v(-19.69, -16.6) * mm});
            skLineSegment(sketch, "E685", {"start": v(-19.69, -16.6) * mm, "end": v(-19.73, -16.6) * mm});
            skLineSegment(sketch, "E686", {"start": v(-19.73, -16.6) * mm, "end": v(-19.77, -16.6) * mm});
            skLineSegment(sketch, "E687", {"start": v(-19.77, -16.6) * mm, "end": v(-19.81, -16.61) * mm});
            skLineSegment(sketch, "E688", {"start": v(-19.81, -16.61) * mm, "end": v(-19.86, -16.62) * mm});
            skLineSegment(sketch, "E689", {"start": v(-19.86, -16.62) * mm, "end": v(-19.9, -16.62) * mm});
            skLineSegment(sketch, "E690", {"start": v(-19.9, -16.62) * mm, "end": v(-19.94, -16.62) * mm});
            skLineSegment(sketch, "E691", {"start": v(-19.94, -16.62) * mm, "end": v(-19.98, -16.62) * mm});
            skLineSegment(sketch, "E692", {"start": v(-19.98, -16.62) * mm, "end": v(-20.03, -16.62) * mm});
            skLineSegment(sketch, "E693", {"start": v(-20.03, -16.62) * mm, "end": v(-20.07, -16.62) * mm});
            skLineSegment(sketch, "E694", {"start": v(-20.07, -16.62) * mm, "end": v(-20.11, -16.62) * mm});
            skLineSegment(sketch, "E695", {"start": v(-20.11, -16.62) * mm, "end": v(-20.15, -16.62) * mm});
            skLineSegment(sketch, "E696", {"start": v(-20.15, -16.62) * mm, "end": v(-20.2, -16.61) * mm});
            skLineSegment(sketch, "E697", {"start": v(-20.2, -16.61) * mm, "end": v(-20.24, -16.6) * mm});
            skLineSegment(sketch, "E698", {"start": v(-20.24, -16.6) * mm, "end": v(-20.28, -16.6) * mm});
            skLineSegment(sketch, "E699", {"start": v(-20.28, -16.6) * mm, "end": v(-20.32, -16.6) * mm});
            skLineSegment(sketch, "E700", {"start": v(-20.32, -16.6) * mm, "end": v(-20.36, -16.58) * mm});
            skLineSegment(sketch, "E701", {"start": v(-20.36, -16.58) * mm, "end": v(-20.4, -16.57) * mm});
            skLineSegment(sketch, "E702", {"start": v(-20.4, -16.57) * mm, "end": v(-20.44, -16.56) * mm});
            skLineSegment(sketch, "E703", {"start": v(-20.44, -16.56) * mm, "end": v(-20.48, -16.54) * mm});
            skLineSegment(sketch, "E704", {"start": v(-20.48, -16.54) * mm, "end": v(-20.52, -16.53) * mm});
            skLineSegment(sketch, "E705", {"start": v(-20.52, -16.53) * mm, "end": v(-20.56, -16.51) * mm});
            skLineSegment(sketch, "E706", {"start": v(-20.56, -16.51) * mm, "end": v(-20.6, -16.5) * mm});
            skLineSegment(sketch, "E707", {"start": v(-20.6, -16.5) * mm, "end": v(-20.64, -16.47) * mm});
            skLineSegment(sketch, "E708", {"start": v(-20.64, -16.47) * mm, "end": v(-20.68, -16.45) * mm});
            skLineSegment(sketch, "E709", {"start": v(-20.68, -16.45) * mm, "end": v(-20.71, -16.43) * mm});
            skLineSegment(sketch, "E710", {"start": v(-20.71, -16.43) * mm, "end": v(-20.75, -16.4) * mm});
            skLineSegment(sketch, "E711", {"start": v(-20.75, -16.4) * mm, "end": v(-20.78, -16.38) * mm});
            skLineSegment(sketch, "E712", {"start": v(-20.78, -16.38) * mm, "end": v(-20.77, -15.27) * mm});
            skLineSegment(sketch, "E713", {"start": v(-18.48, -15.27) * mm, "end": v(-16.91, -15.27) * mm});
            skLineSegment(sketch, "E714", {"start": v(-16.91, -15.27) * mm, "end": v(-16.89, -16.15) * mm});
            skLineSegment(sketch, "E715", {"start": v(-16.89, -16.15) * mm, "end": v(-16.9, -16.21) * mm});
            skLineSegment(sketch, "E716", {"start": v(-16.9, -16.21) * mm, "end": v(-16.9, -16.27) * mm});
            skLineSegment(sketch, "E717", {"start": v(-16.9, -16.27) * mm, "end": v(-16.93, -16.32) * mm});
            skLineSegment(sketch, "E718", {"start": v(-16.93, -16.32) * mm, "end": v(-16.96, -16.37) * mm});
            skLineSegment(sketch, "E719", {"start": v(-16.96, -16.37) * mm, "end": v(-17, -16.42) * mm});
            skLineSegment(sketch, "E720", {"start": v(-17, -16.42) * mm, "end": v(-17.02, -16.45) * mm});
            skLineSegment(sketch, "E721", {"start": v(-17.02, -16.45) * mm, "end": v(-17.04, -16.47) * mm});
            skLineSegment(sketch, "E722", {"start": v(-17.04, -16.47) * mm, "end": v(-17.07, -16.5) * mm});
            skLineSegment(sketch, "E723", {"start": v(-17.07, -16.5) * mm, "end": v(-17.1, -16.52) * mm});
            skLineSegment(sketch, "E724", {"start": v(-17.1, -16.52) * mm, "end": v(-17.13, -16.54) * mm});
            skLineSegment(sketch, "E725", {"start": v(-17.13, -16.54) * mm, "end": v(-17.15, -16.55) * mm});
            skLineSegment(sketch, "E726", {"start": v(-17.15, -16.55) * mm, "end": v(-17.17, -16.56) * mm});
            skLineSegment(sketch, "E727", {"start": v(-17.17, -16.56) * mm, "end": v(-17.19, -16.56) * mm});
            skLineSegment(sketch, "E728", {"start": v(-17.19, -16.56) * mm, "end": v(-17.2, -16.57) * mm});
            skLineSegment(sketch, "E729", {"start": v(-17.2, -16.57) * mm, "end": v(-17.22, -16.57) * mm});
            skLineSegment(sketch, "E730", {"start": v(-17.22, -16.57) * mm, "end": v(-17.24, -16.57) * mm});
            skLineSegment(sketch, "E731", {"start": v(-17.24, -16.57) * mm, "end": v(-17.26, -16.58) * mm});
            skLineSegment(sketch, "E732", {"start": v(-17.26, -16.58) * mm, "end": v(-17.3, -16.58) * mm});
            skLineSegment(sketch, "E733", {"start": v(-17.3, -16.58) * mm, "end": v(-17.39, -16.6) * mm});
            skLineSegment(sketch, "E734", {"start": v(-17.39, -16.6) * mm, "end": v(-17.47, -16.61) * mm});
            skLineSegment(sketch, "E735", {"start": v(-17.47, -16.61) * mm, "end": v(-17.56, -16.62) * mm});
            skLineSegment(sketch, "E736", {"start": v(-17.56, -16.62) * mm, "end": v(-17.6, -16.62) * mm});
            skLineSegment(sketch, "E737", {"start": v(-17.6, -16.62) * mm, "end": v(-17.65, -16.63) * mm});
            skLineSegment(sketch, "E738", {"start": v(-17.65, -16.63) * mm, "end": v(-17.7, -16.63) * mm});
            skLineSegment(sketch, "E739", {"start": v(-17.7, -16.63) * mm, "end": v(-17.74, -16.63) * mm});
            skLineSegment(sketch, "E740", {"start": v(-17.74, -16.63) * mm, "end": v(-17.79, -16.63) * mm});
            skLineSegment(sketch, "E741", {"start": v(-17.79, -16.63) * mm, "end": v(-17.83, -16.62) * mm});
            skLineSegment(sketch, "E742", {"start": v(-17.83, -16.62) * mm, "end": v(-17.88, -16.62) * mm});
            skLineSegment(sketch, "E743", {"start": v(-17.88, -16.62) * mm, "end": v(-17.92, -16.61) * mm});
            skLineSegment(sketch, "E744", {"start": v(-17.92, -16.61) * mm, "end": v(-17.96, -16.6) * mm});
            skLineSegment(sketch, "E745", {"start": v(-17.96, -16.6) * mm, "end": v(-18, -16.6) * mm});
            skLineSegment(sketch, "E746", {"start": v(-18, -16.6) * mm, "end": v(-18.05, -16.59) * mm});
            skLineSegment(sketch, "E747", {"start": v(-18.05, -16.59) * mm, "end": v(-18.1, -16.57) * mm});
            skLineSegment(sketch, "E748", {"start": v(-18.1, -16.57) * mm, "end": v(-18.13, -16.56) * mm});
            skLineSegment(sketch, "E749", {"start": v(-18.13, -16.56) * mm, "end": v(-18.17, -16.54) * mm});
            skLineSegment(sketch, "E750", {"start": v(-18.17, -16.54) * mm, "end": v(-18.2, -16.52) * mm});
            skLineSegment(sketch, "E751", {"start": v(-18.2, -16.52) * mm, "end": v(-18.25, -16.5) * mm});
            skLineSegment(sketch, "E752", {"start": v(-18.25, -16.5) * mm, "end": v(-18.28, -16.48) * mm});
            skLineSegment(sketch, "E753", {"start": v(-18.28, -16.48) * mm, "end": v(-18.32, -16.45) * mm});
            skLineSegment(sketch, "E754", {"start": v(-18.32, -16.45) * mm, "end": v(-18.35, -16.42) * mm});
            skLineSegment(sketch, "E755", {"start": v(-18.35, -16.42) * mm, "end": v(-18.38, -16.39) * mm});
            skLineSegment(sketch, "E756", {"start": v(-18.38, -16.39) * mm, "end": v(-18.4, -16.35) * mm});
            skLineSegment(sketch, "E757", {"start": v(-18.4, -16.35) * mm, "end": v(-18.44, -16.32) * mm});
            skLineSegment(sketch, "E758", {"start": v(-18.44, -16.32) * mm, "end": v(-18.45, -16.25) * mm});
            skLineSegment(sketch, "E759", {"start": v(-18.45, -16.25) * mm, "end": v(-18.46, -16.14) * mm});
            skLineSegment(sketch, "E760", {"start": v(-18.46, -16.14) * mm, "end": v(-18.48, -15.96) * mm});
            skLineSegment(sketch, "E761", {"start": v(-18.48, -15.96) * mm, "end": v(-18.48, -15.27) * mm});
            skLineSegment(sketch, "E762", {"start": v(-16.1, -15.27) * mm, "end": v(-14.53, -15.27) * mm});
            skLineSegment(sketch, "E763", {"start": v(-14.53, -15.27) * mm, "end": v(-14.53, -15.99) * mm});
            skLineSegment(sketch, "E764", {"start": v(-14.53, -15.99) * mm, "end": v(-14.54, -16.16) * mm});
            skLineSegment(sketch, "E765", {"start": v(-14.54, -16.16) * mm, "end": v(-14.55, -16.26) * mm});
            skLineSegment(sketch, "E766", {"start": v(-14.55, -16.26) * mm, "end": v(-14.57, -16.3) * mm});
            skLineSegment(sketch, "E767", {"start": v(-14.57, -16.3) * mm, "end": v(-14.59, -16.33) * mm});
            skLineSegment(sketch, "E768", {"start": v(-14.59, -16.33) * mm, "end": v(-14.6, -16.36) * mm});
            skLineSegment(sketch, "E769", {"start": v(-14.6, -16.36) * mm, "end": v(-14.63, -16.38) * mm});
            skLineSegment(sketch, "E770", {"start": v(-14.63, -16.38) * mm, "end": v(-14.65, -16.41) * mm});
            skLineSegment(sketch, "E771", {"start": v(-14.65, -16.41) * mm, "end": v(-14.67, -16.44) * mm});
            skLineSegment(sketch, "E772", {"start": v(-14.67, -16.44) * mm, "end": v(-14.7, -16.46) * mm});
            skLineSegment(sketch, "E773", {"start": v(-14.7, -16.46) * mm, "end": v(-14.73, -16.48) * mm});
            skLineSegment(sketch, "E774", {"start": v(-14.73, -16.48) * mm, "end": v(-14.76, -16.5) * mm});
            skLineSegment(sketch, "E775", {"start": v(-14.76, -16.5) * mm, "end": v(-14.78, -16.52) * mm});
            skLineSegment(sketch, "E776", {"start": v(-14.78, -16.52) * mm, "end": v(-14.82, -16.53) * mm});
            skLineSegment(sketch, "E777", {"start": v(-14.82, -16.53) * mm, "end": v(-14.85, -16.55) * mm});
            skLineSegment(sketch, "E778", {"start": v(-14.85, -16.55) * mm, "end": v(-14.88, -16.56) * mm});
            skLineSegment(sketch, "E779", {"start": v(-14.88, -16.56) * mm, "end": v(-14.91, -16.57) * mm});
            skLineSegment(sketch, "E780", {"start": v(-14.91, -16.57) * mm, "end": v(-14.95, -16.58) * mm});
            skLineSegment(sketch, "E781", {"start": v(-14.95, -16.58) * mm, "end": v(-14.98, -16.59) * mm});
            skLineSegment(sketch, "E782", {"start": v(-14.98, -16.59) * mm, "end": v(-15.02, -16.6) * mm});
            skLineSegment(sketch, "E783", {"start": v(-15.02, -16.6) * mm, "end": v(-15.05, -16.6) * mm});
            skLineSegment(sketch, "E784", {"start": v(-15.05, -16.6) * mm, "end": v(-15.1, -16.6) * mm});
            skLineSegment(sketch, "E785", {"start": v(-15.1, -16.6) * mm, "end": v(-15.16, -16.61) * mm});
            skLineSegment(sketch, "E786", {"start": v(-15.16, -16.61) * mm, "end": v(-15.24, -16.62) * mm});
            skLineSegment(sketch, "E787", {"start": v(-15.24, -16.62) * mm, "end": v(-15.3, -16.62) * mm});
            skLineSegment(sketch, "E788", {"start": v(-15.3, -16.62) * mm, "end": v(-15.38, -16.62) * mm});
            skLineSegment(sketch, "E789", {"start": v(-15.38, -16.62) * mm, "end": v(-15.44, -16.61) * mm});
            skLineSegment(sketch, "E790", {"start": v(-15.44, -16.61) * mm, "end": v(-15.5, -16.62) * mm});
            skLineSegment(sketch, "E791", {"start": v(-15.5, -16.62) * mm, "end": v(-15.55, -16.61) * mm});
            skLineSegment(sketch, "E792", {"start": v(-15.55, -16.61) * mm, "end": v(-15.6, -16.6) * mm});
            skLineSegment(sketch, "E793", {"start": v(-15.6, -16.6) * mm, "end": v(-15.66, -16.6) * mm});
            skLineSegment(sketch, "E794", {"start": v(-15.66, -16.6) * mm, "end": v(-15.71, -16.59) * mm});
            skLineSegment(sketch, "E795", {"start": v(-15.71, -16.59) * mm, "end": v(-15.74, -16.58) * mm});
            skLineSegment(sketch, "E796", {"start": v(-15.74, -16.58) * mm, "end": v(-15.77, -16.57) * mm});
            skLineSegment(sketch, "E797", {"start": v(-15.77, -16.57) * mm, "end": v(-15.8, -16.56) * mm});
            skLineSegment(sketch, "E798", {"start": v(-15.8, -16.56) * mm, "end": v(-15.82, -16.55) * mm});
            skLineSegment(sketch, "E799", {"start": v(-15.82, -16.55) * mm, "end": v(-15.84, -16.54) * mm});
            skLineSegment(sketch, "E800", {"start": v(-15.84, -16.54) * mm, "end": v(-15.87, -16.53) * mm});
            skLineSegment(sketch, "E801", {"start": v(-15.87, -16.53) * mm, "end": v(-15.9, -16.52) * mm});
            skLineSegment(sketch, "E802", {"start": v(-15.9, -16.52) * mm, "end": v(-15.92, -16.5) * mm});
            skLineSegment(sketch, "E803", {"start": v(-15.92, -16.5) * mm, "end": v(-15.94, -16.49) * mm});
            skLineSegment(sketch, "E804", {"start": v(-15.94, -16.49) * mm, "end": v(-15.96, -16.47) * mm});
            skLineSegment(sketch, "E805", {"start": v(-15.96, -16.47) * mm, "end": v(-15.98, -16.46) * mm});
            skLineSegment(sketch, "E806", {"start": v(-15.98, -16.46) * mm, "end": v(-16, -16.44) * mm});
            skLineSegment(sketch, "E807", {"start": v(-16, -16.44) * mm, "end": v(-16.02, -16.42) * mm});
            skLineSegment(sketch, "E808", {"start": v(-16.02, -16.42) * mm, "end": v(-16.04, -16.4) * mm});
            skLineSegment(sketch, "E809", {"start": v(-16.04, -16.4) * mm, "end": v(-16.05, -16.38) * mm});
            skLineSegment(sketch, "E810", {"start": v(-16.05, -16.38) * mm, "end": v(-16.07, -16.35) * mm});
            skLineSegment(sketch, "E811", {"start": v(-16.07, -16.35) * mm, "end": v(-16.08, -16.33) * mm});
            skLineSegment(sketch, "E812", {"start": v(-16.08, -16.33) * mm, "end": v(-16.1, -16.3) * mm});
            skLineSegment(sketch, "E813", {"start": v(-16.1, -16.3) * mm, "end": v(-16.1, -16.28) * mm});
            skLineSegment(sketch, "E814", {"start": v(-16.1, -16.28) * mm, "end": v(-16.12, -16.18) * mm});
            skLineSegment(sketch, "E815", {"start": v(-16.12, -16.18) * mm, "end": v(-16.13, -16.04) * mm});
            skLineSegment(sketch, "E816", {"start": v(-16.13, -16.04) * mm, "end": v(-16.13, -15.76) * mm});
            skLineSegment(sketch, "E817", {"start": v(-16.13, -15.76) * mm, "end": v(-16.1, -15.27) * mm});
            skLineSegment(sketch, "E818", {"start": v(-13.8, -15.27) * mm, "end": v(-12.24, -15.27) * mm});
            skLineSegment(sketch, "E819", {"start": v(-12.24, -15.27) * mm, "end": v(-12.23, -16.38) * mm});
            skLineSegment(sketch, "E820", {"start": v(-12.23, -16.38) * mm, "end": v(-12.27, -16.4) * mm});
            skLineSegment(sketch, "E821", {"start": v(-12.27, -16.4) * mm, "end": v(-12.3, -16.43) * mm});
            skLineSegment(sketch, "E822", {"start": v(-12.3, -16.43) * mm, "end": v(-12.34, -16.45) * mm});
            skLineSegment(sketch, "E823", {"start": v(-12.34, -16.45) * mm, "end": v(-12.38, -16.48) * mm});
            skLineSegment(sketch, "E824", {"start": v(-12.38, -16.48) * mm, "end": v(-12.42, -16.5) * mm});
            skLineSegment(sketch, "E825", {"start": v(-12.42, -16.5) * mm, "end": v(-12.46, -16.51) * mm});
            skLineSegment(sketch, "E826", {"start": v(-12.46, -16.51) * mm, "end": v(-12.5, -16.53) * mm});
            skLineSegment(sketch, "E827", {"start": v(-12.5, -16.53) * mm, "end": v(-12.54, -16.55) * mm});
            skLineSegment(sketch, "E828", {"start": v(-12.54, -16.55) * mm, "end": v(-12.58, -16.56) * mm});
            skLineSegment(sketch, "E829", {"start": v(-12.58, -16.56) * mm, "end": v(-12.62, -16.57) * mm});
            skLineSegment(sketch, "E830", {"start": v(-12.62, -16.57) * mm, "end": v(-12.66, -16.58) * mm});
            skLineSegment(sketch, "E831", {"start": v(-12.66, -16.58) * mm, "end": v(-12.7, -16.6) * mm});
            skLineSegment(sketch, "E832", {"start": v(-12.7, -16.6) * mm, "end": v(-12.75, -16.6) * mm});
            skLineSegment(sketch, "E833", {"start": v(-12.75, -16.6) * mm, "end": v(-12.8, -16.6) * mm});
            skLineSegment(sketch, "E834", {"start": v(-12.8, -16.6) * mm, "end": v(-12.84, -16.61) * mm});
            skLineSegment(sketch, "E835", {"start": v(-12.84, -16.61) * mm, "end": v(-12.88, -16.62) * mm});
            skLineSegment(sketch, "E836", {"start": v(-12.88, -16.62) * mm, "end": v(-12.92, -16.62) * mm});
            skLineSegment(sketch, "E837", {"start": v(-12.92, -16.62) * mm, "end": v(-12.97, -16.62) * mm});
            skLineSegment(sketch, "E838", {"start": v(-12.97, -16.62) * mm, "end": v(-13.01, -16.62) * mm});
            skLineSegment(sketch, "E839", {"start": v(-13.01, -16.62) * mm, "end": v(-13.05, -16.62) * mm});
            skLineSegment(sketch, "E840", {"start": v(-13.05, -16.62) * mm, "end": v(-13.1, -16.62) * mm});
            skLineSegment(sketch, "E841", {"start": v(-13.1, -16.62) * mm, "end": v(-13.14, -16.62) * mm});
            skLineSegment(sketch, "E842", {"start": v(-13.14, -16.62) * mm, "end": v(-13.19, -16.61) * mm});
            skLineSegment(sketch, "E843", {"start": v(-13.19, -16.61) * mm, "end": v(-13.23, -16.6) * mm});
            skLineSegment(sketch, "E844", {"start": v(-13.23, -16.6) * mm, "end": v(-13.27, -16.6) * mm});
            skLineSegment(sketch, "E845", {"start": v(-13.27, -16.6) * mm, "end": v(-13.32, -16.6) * mm});
            skLineSegment(sketch, "E846", {"start": v(-13.32, -16.6) * mm, "end": v(-13.36, -16.59) * mm});
            skLineSegment(sketch, "E847", {"start": v(-13.36, -16.59) * mm, "end": v(-13.4, -16.58) * mm});
            skLineSegment(sketch, "E848", {"start": v(-13.4, -16.58) * mm, "end": v(-13.44, -16.57) * mm});
            skLineSegment(sketch, "E849", {"start": v(-13.44, -16.57) * mm, "end": v(-13.63, -16.48) * mm});
            skLineSegment(sketch, "E850", {"start": v(-13.63, -16.48) * mm, "end": v(-13.67, -16.46) * mm});
            skLineSegment(sketch, "E851", {"start": v(-13.67, -16.46) * mm, "end": v(-13.7, -16.44) * mm});
            skLineSegment(sketch, "E852", {"start": v(-13.7, -16.44) * mm, "end": v(-13.72, -16.42) * mm});
            skLineSegment(sketch, "E853", {"start": v(-13.72, -16.42) * mm, "end": v(-13.74, -16.4) * mm});
            skLineSegment(sketch, "E854", {"start": v(-13.74, -16.4) * mm, "end": v(-13.74, -16.39) * mm});
            skLineSegment(sketch, "E855", {"start": v(-13.74, -16.39) * mm, "end": v(-13.75, -16.37) * mm});
            skLineSegment(sketch, "E856", {"start": v(-13.75, -16.37) * mm, "end": v(-13.76, -16.36) * mm});
            skLineSegment(sketch, "E857", {"start": v(-13.76, -16.36) * mm, "end": v(-13.76, -16.34) * mm});
            skLineSegment(sketch, "E858", {"start": v(-13.76, -16.34) * mm, "end": v(-13.77, -16.33) * mm});
            skLineSegment(sketch, "E859", {"start": v(-13.77, -16.33) * mm, "end": v(-13.77, -16.31) * mm});
            skLineSegment(sketch, "E860", {"start": v(-13.77, -16.31) * mm, "end": v(-13.78, -16.3) * mm});
            skLineSegment(sketch, "E861", {"start": v(-13.78, -16.3) * mm, "end": v(-13.8, -15.27) * mm});
            skFitSpline(sketch, "E862", {"points": [v(-16.09, 0.4) * mm, v(-16.48, 0.53) * mm, v(-16.87, 0.42) * mm], "startDerivative": vector(-0.77, 0.4) * mm, "endDerivative": vector(-0.8, -0.36) * mm});
            skFitSpline(sketch, "E863", {"points": [v(-9.68, -1.66) * mm, v(-8.41, -1.95) * mm, v(-8.04, -3.41) * mm], "startDerivative": vector(3.1, -0.07) * mm, "endDerivative": vector(0.22, -3.4) * mm});
            skLineSegment(sketch, "E864", {"start": v(-8.04, -3.41) * mm, "end": v(-8.04, -3.57) * mm});
            skLineSegment(sketch, "E865", {"start": v(-16.09, 0.4) * mm, "end": v(-15.75, 0.24) * mm});
            skLineSegment(sketch, "E866", {"start": v(-17.01, 0.36) * mm, "end": v(-16.87, 0.42) * mm});
            skLineSegment(sketch, "E867", {"start": v(-9.68, -1.66) * mm, "end": v(-9.7, 0.57) * mm});
            skLineSegment(sketch, "E868", {"start": v(-13.9, -1.75) * mm, "end": v(-16.26, -0.55) * mm});
            skFitSpline(sketch, "E869", {"points": [v(-16.26, -0.55) * mm, v(-16.5, -0.47) * mm, v(-16.83, -0.6) * mm], "startDerivative": vector(-0.52, 0.27) * mm, "endDerivative": vector(-0.63, -0.37) * mm});
            skFitSpline(sketch, "E870", {"points": [v(-9.4, -3.99) * mm, v(-9.18, -4.2) * mm, v(-9.85, -4.84) * mm], "startDerivative": vector(0.88, -0.52) * mm, "endDerivative": vector(-1.57, -1.12) * mm});
            skSolve(sketch);
        }
        {
            var Q0;
            Q0=qSketchRegion(id+"F28",true);
            extrude(context, id + "F29", {"entities" : qUnion([Q0]), "endBound" : BoundingType.UP_TO_NEXT, "oppositeDirection" : true, "depth" : 26.5 * mm});
        }
        {
            var Q0;
            {var subQ0=sQuery(id+"F18.wireOp",EDGE,"E69");Q0=makeQuery(id+"F18.imprint","IMPRINT",FACE,{"disambiguationData":[TD([[makeQuery(id+"F18.imprint","IMPRINT",EDGE,{"derivedFrom":subQ0}),-1.0]])]});}
            extrude(context, id + "F30", {"entities" : qUnion([Q0]), "operationType" : NewBodyOperationType.REMOVE, "oppositeDirection" : true, "depth" : 2 * mm});
        }
        {
            var Q0;
            Q0=qCreatedBy(makeId("Top.planeOp"),FACE);
            var sketch = newSketch(context, id + "F31", { "sketchPlane" : qUnion([Q0])});
            skLineSegment(sketch, "E871.bottom", {"start": v(7.48, -5.58) * mm, "end": v(13.97, -5.58) * mm});
            skLineSegment(sketch, "E871.top", {"start": v(7.48, -5.2) * mm, "end": v(13.97, -5.2) * mm});
            skLineSegment(sketch, "E872.bottom", {"start": v(6.04, -5.58) * mm, "end": v(16.8, -5.58) * mm});
            skLineSegment(sketch, "E872.top", {"start": v(6.04, -5.2) * mm, "end": v(16.8, -5.2) * mm});
            skLineSegment(sketch, "E872.left", {"start": v(6.04, -5.58) * mm, "end": v(6.04, -5.2) * mm});
            skLineSegment(sketch, "E873", {"start": v(16.8, -5.2) * mm, "end": v(18.32, -5.2) * mm});
            skLineSegment(sketch, "E874", {"start": v(18.32, -5.2) * mm, "end": v(18.32, -5.58) * mm});
            skLineSegment(sketch, "E875", {"start": v(18.32, -5.58) * mm, "end": v(16.8, -5.58) * mm});
            skSolve(sketch);
        }
        {
            var Q0;
            Q0=qSketchRegion(id+"F31",true);
            var Q1;
            {var subQ1=sQuery(id+"F2.wireOp",EDGE,"E22");var subQ3=sQuery(id+"F2.wireOp",EDGE,"E20");Q1=makeQuery(id+"F24.boolean.opBoolean","SPLIT",FACE,{"disambiguationData":[TD([makeQuery(id+"F6.opShell","OFFSET_FACE",FACE,{"disambiguationData":[OSD([sQuery(id+"F0.wireOp",EDGE,"E3")])]})])],"derivedFrom":makeQuery(id+"F6.opShell","OFFSET_FACE",FACE,{"disambiguationData":[OSD([subQ3,subQ1])]})});}
            extrude(context, id + "F32", {"entities" : qUnion([Q0]), "operationType" : NewBodyOperationType.ADD, "endBound" : BoundingType.UP_TO_SURFACE, "endBoundEntityFace" : qUnion([Q1]), "depth" : 25 * mm});
        }
        {
            var Q0;
            {var subQ0=sQuery(id+"F0.wireOp",EDGE,"E7.rect.top");var subQ1=sQuery(id+"F0.wireOp",EDGE,"E7.rect.right");var subQ2=sQuery(id+"F0.wireOp",EDGE,"E7.rect.left");var subQ3=sQuery(id+"F0.wireOp",EDGE,"E7.rect.bottom");var subQ4=sQuery(id+"F0.wireOp",EDGE,"E5.MirrorC");var subQ5=sQuery(id+"F0.wireOp",EDGE,"E3");var subQ6=sQuery(id+"F0.wireOp",EDGE,"E2");var subQ7=sQuery(id+"F0.wireOp",EDGE,"E1");Q0=makeQuery(id+"F29.boolean.opBoolean","SPLIT",FACE,{"disambiguationData":[TD([makeQuery(id+"F4.opFillet","BLEND_FACE",FACE,{"disambiguationData":[OSD([subQ0])]})])],"derivedFrom":makeQuery(id+"F1.opExtrude","CAP_FACE",FACE,{"disambiguationData":[OSD([subQ7,subQ6,subQ5,subQ4,subQ3,subQ0,subQ2,subQ1])],"isStart":false})});}
            cPlane(context, id + "F33", {"entities" : qUnion([Q0]), "cplaneType" : CPlaneType.OFFSET, "offset" : 9 * mm, "oppositeDirection" : true, "width" : 150 * mm, "height" : 150 * mm});
        }
        {
            var Q0;
            Q0=qCreatedBy(id+"F33.planeOp",FACE);
            var sketch = newSketch(context, id + "F34", { "sketchPlane" : qUnion([Q0])});
            skCircle(sketch, "E876", {"center": v(-29.86, -30.9) * mm, "radius": 1.22 * mm});
            skCircle(sketch, "E877", {"center": v(-29.84, 14.65) * mm, "radius": 1.25 * mm});
            skSolve(sketch);
        }
        {
            var Q0;
            Q0=qSketchRegion(id+"F34",true);
            var Q1;
            Q1=makeQuery(id+"F3.boolean.opBoolean","COPY",FACE,{"derivedFrom":makeQuery(id+"F3.opExtrude","SWEPT_FACE",FACE,{"disambiguationData":[OSD([sQuery(id+"F2.wireOp",EDGE,"E14")])]})});
            extrude(context, id + "F35", {"entities" : qUnion([Q0]), "operationType" : NewBodyOperationType.ADD, "endBound" : BoundingType.UP_TO_SURFACE, "endBoundEntityFace" : qUnion([Q1]), "depth" : 25 * mm});
        }
        {
            var Q0;
            {var subQ0=sQuery(id+"F0.wireOp",EDGE,"E7.rect.right");var subQ1=sQuery(id+"F0.wireOp",EDGE,"E7.rect.left");var subQ2=sQuery(id+"F0.wireOp",EDGE,"E7.rect.top");var subQ3=sQuery(id+"F0.wireOp",EDGE,"E7.rect.bottom");var subQ4=sQuery(id+"F0.wireOp",EDGE,"E5.MirrorC");var subQ5=sQuery(id+"F0.wireOp",EDGE,"E3");var subQ6=sQuery(id+"F0.wireOp",EDGE,"E2");var subQ7=sQuery(id+"F0.wireOp",EDGE,"E1");Q0=makeQuery(id+"F29.boolean.opBoolean","SPLIT",FACE,{"disambiguationData":[TD([makeQuery(id+"F4.opFillet","BLEND_FACE",FACE,{"disambiguationData":[OSD([subQ3])]})])],"derivedFrom":makeQuery(id+"F1.opExtrude","CAP_FACE",FACE,{"disambiguationData":[OSD([subQ7,subQ6,subQ5,subQ4,subQ3,subQ2,subQ1,subQ0])],"isStart":false})});}
            cPlane(context, id + "F36", {"entities" : qUnion([Q0]), "cplaneType" : CPlaneType.OFFSET, "offset" : 17.5 * mm, "oppositeDirection" : true, "width" : 150 * mm, "height" : 150 * mm});
        }
        {
            var Q0;
            Q0=qCreatedBy(id+"F36.planeOp",FACE);
            var sketch = newSketch(context, id + "F37", { "sketchPlane" : qUnion([Q0])});
            skCircle(sketch, "E878", {"center": v(8.9, 3.98) * mm, "radius": 1.26 * mm});
            skCircle(sketch, "E879", {"center": v(15.8, -30.92) * mm, "radius": 1.17 * mm});
            skSolve(sketch);
        }
        {
            var Q0;
            Q0=qSketchRegion(id+"F37",true);
            var Q1;
            {var subQ0=sQuery(id+"F2.wireOp",EDGE,"E22");var subQ1=sQuery(id+"F2.wireOp",EDGE,"E20");Q1=makeQuery(id+"F24.boolean.opBoolean","SPLIT",FACE,{"disambiguationData":[TD([makeQuery(id+"F1.opExtrude","SWEPT_FACE",FACE,{"disambiguationData":[OSD([sQuery(id+"F0.wireOp",EDGE,"E3")])]})])],"derivedFrom":makeQuery(id+"F3.boolean.opBoolean","COPY",FACE,{"derivedFrom":makeQuery(id+"F3.opExtrude","SWEPT_FACE",FACE,{"disambiguationData":[OSD([subQ1,subQ0])]})})});}
            extrude(context, id + "F38", {"entities" : qUnion([Q0]), "operationType" : NewBodyOperationType.ADD, "endBound" : BoundingType.UP_TO_SURFACE, "endBoundEntityFace" : qUnion([Q1]), "depth" : 25 * mm});
        }
        {
            var Q0;
            Q0=makeQuery(id+"F1.opExtrude","SWEPT_FACE",FACE,{"disambiguationData":[OSD([sQuery(id+"F0.wireOp",EDGE,"E7.rect.bottom")])]});
            cPlane(context, id + "F39", {"entities" : qUnion([Q0]), "cplaneType" : CPlaneType.OFFSET, "offset" : 1.8 * mm, "oppositeDirection" : true, "width" : 150 * mm, "height" : 150 * mm});
        }
        {
            var Q0;
            Q0=qCreatedBy(id+"F39.planeOp",FACE);
            var sketch = newSketch(context, id + "F40", { "sketchPlane" : qUnion([Q0])});
            skLineSegment(sketch, "E880.top", {"start": v(-5.27, 0) * mm, "end": v(12.86, 0) * mm});
            skLineSegment(sketch, "E881.right", {"start": v(12.86, 5.48) * mm, "end": v(12.86, 0) * mm});
            skLineSegment(sketch, "E882.bottom", {"start": v(12.86, 0) * mm, "end": v(-5.27, 0) * mm});
            skLineSegment(sketch, "E882.top", {"start": v(12.86, 5.48) * mm, "end": v(-5.27, 5.48) * mm});
            skLineSegment(sketch, "E882.left", {"start": v(12.86, 0) * mm, "end": v(12.86, 5.48) * mm});
            skPoint(sketch, "E883.orphan", {"position": v(14.06, 0) * mm});
            skLineSegment(sketch, "E884", {"start": v(-5.27, 5.48) * mm, "end": v(-8, 5.48) * mm});
            skLineSegment(sketch, "E885", {"start": v(-8, 5.48) * mm, "end": v(-8, 0) * mm});
            skLineSegment(sketch, "E886", {"start": v(-8, 0) * mm, "end": v(-5.27, 0) * mm});
            skSolve(sketch);
        }
        {
            var Q0;
            Q0=qSketchRegion(id+"F40",true);
            extrude(context, id + "F41", {"entities" : qUnion([Q0]), "operationType" : NewBodyOperationType.REMOVE, "depth" : 1.2 * mm});
        }
        {
            var Q0;
            Q0=qCreatedBy(makeId("Top.planeOp"),FACE);
            var sketch = newSketch(context, id + "F42", { "sketchPlane" : qUnion([Q0])});
            skLineSegment(sketch, "E887.bottom", {"start": v(-10.2, -20.34) * mm, "end": v(-23.5, -20.34) * mm});
            skLineSegment(sketch, "E887.top", {"start": v(-9.76, -20.7) * mm, "end": v(-23.91, -20.7) * mm});
            skLineSegment(sketch, "E887.left", {"start": v(-9.76, -20.34) * mm, "end": v(-9.76, -20.7) * mm});
            skLineSegment(sketch, "E888", {"start": v(-9.76, -19.58) * mm, "end": v(-9.76, 2.28) * mm});
            skLineSegment(sketch, "E889.bottom", {"start": v(-10.2, 2.28) * mm, "end": v(-23.5, 2.28) * mm});
            skLineSegment(sketch, "E889.top", {"start": v(-9.76, 2.58) * mm, "end": v(-23.91, 2.58) * mm});
            skLineSegment(sketch, "E889.left", {"start": v(-9.76, 2.28) * mm, "end": v(-9.76, 2.58) * mm});
            skLineSegment(sketch, "E889.right", {"start": v(-23.91, 2.28) * mm, "end": v(-23.91, 2.58) * mm});
            skLineSegment(sketch, "E890.bottom", {"start": v(-10.2, -10.06) * mm, "end": v(-23.5, -10.06) * mm});
            skLineSegment(sketch, "E890.top", {"start": v(-10.2, -9.35) * mm, "end": v(-23.5, -9.35) * mm});
            skLineSegment(sketch, "E890.left", {"start": v(-9.76, -10.06) * mm, "end": v(-9.76, -9.35) * mm});
            skLineSegment(sketch, "E890.right", {"start": v(-25.9, -10.06) * mm, "end": v(-25.9, -9.35) * mm});
            skLineSegment(sketch, "E891", {"start": v(-10.2, -19.58) * mm, "end": v(-10.2, -10.06) * mm});
            skLineSegment(sketch, "E892.bottom", {"start": v(-23.91, 2.58) * mm, "end": v(-23.5, 2.58) * mm});
            skLineSegment(sketch, "E892.top", {"start": v(-23.91, -20.7) * mm, "end": v(-23.5, -20.7) * mm});
            skLineSegment(sketch, "E892.left", {"start": v(-23.91, 2.58) * mm, "end": v(-23.91, 2.28) * mm});
            skLineSegment(sketch, "E892.right", {"start": v(-23.5, 1.67) * mm, "end": v(-23.5, -9.35) * mm});
            skLineSegment(sketch, "E893.trimOffspring", {"start": v(-10.2, -9.35) * mm, "end": v(-10.2, 2.28) * mm});
            skLineSegment(sketch, "E894.trimOffspring", {"start": v(-23.91, -10.06) * mm, "end": v(-25.9, -10.06) * mm});
            skLineSegment(sketch, "E895.trimOffspring", {"start": v(-23.91, -10.06) * mm, "end": v(-23.91, -20.7) * mm});
            skLineSegment(sketch, "E896.trimOffspring", {"start": v(-23.5, -10.06) * mm, "end": v(-23.5, -20.34) * mm});
            skLineSegment(sketch, "E897.trimOffspring", {"start": v(-23.91, -9.35) * mm, "end": v(-25.9, -9.35) * mm});
            skLineSegment(sketch, "E898", {"start": v(-10.2, -19.58) * mm, "end": v(-9.76, -19.58) * mm});
            skLineSegment(sketch, "E899", {"start": v(-10.2, -20.34) * mm, "end": v(-9.76, -20.34) * mm});
            skLineSegment(sketch, "E900", {"start": v(-23.5, 2.28) * mm, "end": v(-23.91, 2.28) * mm});
            skLineSegment(sketch, "E901", {"start": v(-23.5, 1.67) * mm, "end": v(-23.91, 1.67) * mm});
            skLineSegment(sketch, "E902.trimOffspring", {"start": v(-23.91, 1.67) * mm, "end": v(-23.91, -9.35) * mm});
            skSolve(sketch);
        }
        {
            var Q0;
            Q0=qSketchRegion(id+"F42",true);
            var Q1;
            {var subQ0=sQuery(id+"F28.wireOp",EDGE,"E861");var subQ1=sQuery(id+"F28.wireOp",EDGE,"E860");var subQ2=sQuery(id+"F28.wireOp",EDGE,"E859");var subQ3=sQuery(id+"F28.wireOp",EDGE,"E858");var subQ4=sQuery(id+"F28.wireOp",EDGE,"E857");var subQ5=sQuery(id+"F28.wireOp",EDGE,"E856");var subQ6=sQuery(id+"F28.wireOp",EDGE,"E855");var subQ7=sQuery(id+"F28.wireOp",EDGE,"E854");var subQ8=sQuery(id+"F28.wireOp",EDGE,"E853");var subQ9=sQuery(id+"F28.wireOp",EDGE,"E852");var subQ10=sQuery(id+"F28.wireOp",EDGE,"E851");var subQ11=sQuery(id+"F28.wireOp",EDGE,"E850");var subQ12=sQuery(id+"F28.wireOp",EDGE,"E849");var subQ13=sQuery(id+"F28.wireOp",EDGE,"E848");var subQ14=sQuery(id+"F28.wireOp",EDGE,"E847");var subQ15=sQuery(id+"F28.wireOp",EDGE,"E846");var subQ16=sQuery(id+"F28.wireOp",EDGE,"E845");var subQ17=sQuery(id+"F28.wireOp",EDGE,"E844");var subQ18=sQuery(id+"F28.wireOp",EDGE,"E843");var subQ19=sQuery(id+"F28.wireOp",EDGE,"E842");var subQ20=sQuery(id+"F28.wireOp",EDGE,"E841");var subQ21=sQuery(id+"F28.wireOp",EDGE,"E840");var subQ22=sQuery(id+"F28.wireOp",EDGE,"E839");var subQ23=sQuery(id+"F28.wireOp",EDGE,"E838");var subQ24=sQuery(id+"F28.wireOp",EDGE,"E837");var subQ25=sQuery(id+"F28.wireOp",EDGE,"E836");var subQ26=sQuery(id+"F28.wireOp",EDGE,"E835");var subQ27=sQuery(id+"F28.wireOp",EDGE,"E834");var subQ28=sQuery(id+"F28.wireOp",EDGE,"E833");var subQ29=sQuery(id+"F28.wireOp",EDGE,"E832");var subQ30=sQuery(id+"F28.wireOp",EDGE,"E831");var subQ31=sQuery(id+"F28.wireOp",EDGE,"E830");var subQ32=sQuery(id+"F28.wireOp",EDGE,"E829");var subQ33=sQuery(id+"F28.wireOp",EDGE,"E828");var subQ34=sQuery(id+"F28.wireOp",EDGE,"E827");var subQ35=sQuery(id+"F28.wireOp",EDGE,"E826");var subQ36=sQuery(id+"F28.wireOp",EDGE,"E825");var subQ37=sQuery(id+"F28.wireOp",EDGE,"E824");var subQ38=sQuery(id+"F28.wireOp",EDGE,"E823");var subQ39=sQuery(id+"F28.wireOp",EDGE,"E822");var subQ40=sQuery(id+"F28.wireOp",EDGE,"E821");var subQ41=sQuery(id+"F28.wireOp",EDGE,"E820");var subQ42=sQuery(id+"F28.wireOp",EDGE,"E819");var subQ43=sQuery(id+"F28.wireOp",EDGE,"E818");var subQ44=sQuery(id+"F28.wireOp",EDGE,"E817");var subQ45=sQuery(id+"F28.wireOp",EDGE,"E816");var subQ46=sQuery(id+"F28.wireOp",EDGE,"E815");var subQ47=sQuery(id+"F28.wireOp",EDGE,"E814");var subQ48=sQuery(id+"F28.wireOp",EDGE,"E813");var subQ49=sQuery(id+"F28.wireOp",EDGE,"E812");var subQ50=sQuery(id+"F28.wireOp",EDGE,"E811");var subQ51=sQuery(id+"F28.wireOp",EDGE,"E810");var subQ52=sQuery(id+"F28.wireOp",EDGE,"E809");var subQ53=sQuery(id+"F28.wireOp",EDGE,"E808");var subQ54=sQuery(id+"F28.wireOp",EDGE,"E807");var subQ55=sQuery(id+"F28.wireOp",EDGE,"E806");var subQ56=sQuery(id+"F28.wireOp",EDGE,"E805");var subQ57=sQuery(id+"F28.wireOp",EDGE,"E804");var subQ58=sQuery(id+"F28.wireOp",EDGE,"E803");var subQ59=sQuery(id+"F28.wireOp",EDGE,"E802");var subQ60=sQuery(id+"F28.wireOp",EDGE,"E801");var subQ61=sQuery(id+"F28.wireOp",EDGE,"E800");var subQ62=sQuery(id+"F28.wireOp",EDGE,"E799");var subQ63=sQuery(id+"F28.wireOp",EDGE,"E798");var subQ64=sQuery(id+"F28.wireOp",EDGE,"E797");var subQ65=sQuery(id+"F28.wireOp",EDGE,"E796");var subQ66=sQuery(id+"F28.wireOp",EDGE,"E795");var subQ67=sQuery(id+"F28.wireOp",EDGE,"E794");var subQ68=sQuery(id+"F28.wireOp",EDGE,"E793");var subQ69=sQuery(id+"F28.wireOp",EDGE,"E792");var subQ70=sQuery(id+"F28.wireOp",EDGE,"E791");var subQ71=sQuery(id+"F28.wireOp",EDGE,"E790");var subQ72=sQuery(id+"F28.wireOp",EDGE,"E789");var subQ73=sQuery(id+"F28.wireOp",EDGE,"E788");var subQ74=sQuery(id+"F28.wireOp",EDGE,"E787");var subQ75=sQuery(id+"F28.wireOp",EDGE,"E786");var subQ76=sQuery(id+"F28.wireOp",EDGE,"E785");var subQ77=sQuery(id+"F28.wireOp",EDGE,"E784");var subQ78=sQuery(id+"F28.wireOp",EDGE,"E783");var subQ79=sQuery(id+"F28.wireOp",EDGE,"E782");var subQ80=sQuery(id+"F28.wireOp",EDGE,"E781");var subQ81=sQuery(id+"F28.wireOp",EDGE,"E780");var subQ82=sQuery(id+"F28.wireOp",EDGE,"E779");var subQ83=sQuery(id+"F28.wireOp",EDGE,"E778");var subQ84=sQuery(id+"F28.wireOp",EDGE,"E777");var subQ85=sQuery(id+"F28.wireOp",EDGE,"E776");var subQ86=sQuery(id+"F28.wireOp",EDGE,"E775");var subQ87=sQuery(id+"F28.wireOp",EDGE,"E774");var subQ88=sQuery(id+"F28.wireOp",EDGE,"E773");var subQ89=sQuery(id+"F28.wireOp",EDGE,"E772");var subQ90=sQuery(id+"F28.wireOp",EDGE,"E771");var subQ91=sQuery(id+"F28.wireOp",EDGE,"E770");var subQ92=sQuery(id+"F28.wireOp",EDGE,"E769");var subQ93=sQuery(id+"F28.wireOp",EDGE,"E768");var subQ94=sQuery(id+"F28.wireOp",EDGE,"E767");var subQ95=sQuery(id+"F28.wireOp",EDGE,"E766");var subQ96=sQuery(id+"F28.wireOp",EDGE,"E765");var subQ97=sQuery(id+"F28.wireOp",EDGE,"E764");var subQ98=sQuery(id+"F28.wireOp",EDGE,"E763");var subQ99=sQuery(id+"F28.wireOp",EDGE,"E762");var subQ100=sQuery(id+"F28.wireOp",EDGE,"E761");var subQ101=sQuery(id+"F28.wireOp",EDGE,"E760");var subQ102=sQuery(id+"F28.wireOp",EDGE,"E759");var subQ103=sQuery(id+"F28.wireOp",EDGE,"E758");var subQ104=sQuery(id+"F28.wireOp",EDGE,"E757");var subQ105=sQuery(id+"F28.wireOp",EDGE,"E756");var subQ106=sQuery(id+"F28.wireOp",EDGE,"E755");var subQ107=sQuery(id+"F28.wireOp",EDGE,"E754");var subQ108=sQuery(id+"F28.wireOp",EDGE,"E753");var subQ109=sQuery(id+"F28.wireOp",EDGE,"E752");var subQ110=sQuery(id+"F28.wireOp",EDGE,"E751");var subQ111=sQuery(id+"F28.wireOp",EDGE,"E750");var subQ112=sQuery(id+"F28.wireOp",EDGE,"E749");var subQ113=sQuery(id+"F28.wireOp",EDGE,"E748");var subQ114=sQuery(id+"F28.wireOp",EDGE,"E747");var subQ115=sQuery(id+"F28.wireOp",EDGE,"E746");var subQ116=sQuery(id+"F28.wireOp",EDGE,"E745");var subQ117=sQuery(id+"F28.wireOp",EDGE,"E744");var subQ118=sQuery(id+"F28.wireOp",EDGE,"E743");var subQ119=sQuery(id+"F28.wireOp",EDGE,"E742");var subQ120=sQuery(id+"F28.wireOp",EDGE,"E741");var subQ121=sQuery(id+"F28.wireOp",EDGE,"E740");var subQ122=sQuery(id+"F28.wireOp",EDGE,"E739");var subQ123=sQuery(id+"F28.wireOp",EDGE,"E738");var subQ124=sQuery(id+"F28.wireOp",EDGE,"E737");var subQ125=sQuery(id+"F28.wireOp",EDGE,"E736");var subQ126=sQuery(id+"F28.wireOp",EDGE,"E735");var subQ127=sQuery(id+"F28.wireOp",EDGE,"E734");var subQ128=sQuery(id+"F28.wireOp",EDGE,"E733");var subQ129=sQuery(id+"F28.wireOp",EDGE,"E732");var subQ130=sQuery(id+"F28.wireOp",EDGE,"E731");var subQ131=sQuery(id+"F28.wireOp",EDGE,"E730");var subQ132=sQuery(id+"F28.wireOp",EDGE,"E729");var subQ133=sQuery(id+"F28.wireOp",EDGE,"E728");var subQ134=sQuery(id+"F28.wireOp",EDGE,"E727");var subQ135=sQuery(id+"F28.wireOp",EDGE,"E726");var subQ136=sQuery(id+"F28.wireOp",EDGE,"E725");var subQ137=sQuery(id+"F28.wireOp",EDGE,"E724");var subQ138=sQuery(id+"F28.wireOp",EDGE,"E723");var subQ139=sQuery(id+"F28.wireOp",EDGE,"E722");var subQ140=sQuery(id+"F28.wireOp",EDGE,"E721");var subQ141=sQuery(id+"F28.wireOp",EDGE,"E720");var subQ142=sQuery(id+"F28.wireOp",EDGE,"E719");var subQ143=sQuery(id+"F28.wireOp",EDGE,"E718");var subQ144=sQuery(id+"F28.wireOp",EDGE,"E717");var subQ145=sQuery(id+"F28.wireOp",EDGE,"E716");var subQ146=sQuery(id+"F28.wireOp",EDGE,"E715");var subQ147=sQuery(id+"F28.wireOp",EDGE,"E714");var subQ148=sQuery(id+"F28.wireOp",EDGE,"E713");var subQ149=sQuery(id+"F28.wireOp",EDGE,"E712");var subQ150=sQuery(id+"F28.wireOp",EDGE,"E711");var subQ151=sQuery(id+"F28.wireOp",EDGE,"E710");var subQ152=sQuery(id+"F28.wireOp",EDGE,"E709");var subQ153=sQuery(id+"F28.wireOp",EDGE,"E708");var subQ154=sQuery(id+"F28.wireOp",EDGE,"E707");var subQ155=sQuery(id+"F28.wireOp",EDGE,"E706");var subQ156=sQuery(id+"F28.wireOp",EDGE,"E705");var subQ157=sQuery(id+"F28.wireOp",EDGE,"E704");var subQ158=sQuery(id+"F28.wireOp",EDGE,"E703");var subQ159=sQuery(id+"F28.wireOp",EDGE,"E702");var subQ160=sQuery(id+"F28.wireOp",EDGE,"E701");var subQ161=sQuery(id+"F28.wireOp",EDGE,"E700");var subQ162=sQuery(id+"F28.wireOp",EDGE,"E699");var subQ163=sQuery(id+"F28.wireOp",EDGE,"E698");var subQ164=sQuery(id+"F28.wireOp",EDGE,"E697");var subQ165=sQuery(id+"F28.wireOp",EDGE,"E696");var subQ166=sQuery(id+"F28.wireOp",EDGE,"E695");var subQ167=sQuery(id+"F28.wireOp",EDGE,"E694");var subQ168=sQuery(id+"F28.wireOp",EDGE,"E693");var subQ169=sQuery(id+"F28.wireOp",EDGE,"E692");var subQ170=sQuery(id+"F28.wireOp",EDGE,"E691");var subQ171=sQuery(id+"F28.wireOp",EDGE,"E690");var subQ172=sQuery(id+"F28.wireOp",EDGE,"E689");var subQ173=sQuery(id+"F28.wireOp",EDGE,"E688");var subQ174=sQuery(id+"F28.wireOp",EDGE,"E687");var subQ175=sQuery(id+"F28.wireOp",EDGE,"E686");var subQ176=sQuery(id+"F28.wireOp",EDGE,"E685");var subQ177=sQuery(id+"F28.wireOp",EDGE,"E684");var subQ178=sQuery(id+"F28.wireOp",EDGE,"E683");var subQ179=sQuery(id+"F28.wireOp",EDGE,"E682");var subQ180=sQuery(id+"F28.wireOp",EDGE,"E681");var subQ181=sQuery(id+"F28.wireOp",EDGE,"E680");var subQ182=sQuery(id+"F28.wireOp",EDGE,"E679");var subQ183=sQuery(id+"F28.wireOp",EDGE,"E678");var subQ184=sQuery(id+"F28.wireOp",EDGE,"E677");var subQ185=sQuery(id+"F28.wireOp",EDGE,"E676");var subQ186=sQuery(id+"F28.wireOp",EDGE,"E675");var subQ187=sQuery(id+"F28.wireOp",EDGE,"E674");var subQ188=sQuery(id+"F28.wireOp",EDGE,"E673");var subQ189=sQuery(id+"F28.wireOp",EDGE,"E672");var subQ190=sQuery(id+"F28.wireOp",EDGE,"E671");var subQ191=sQuery(id+"F28.wireOp",EDGE,"E670");var subQ192=sQuery(id+"F28.wireOp",EDGE,"E669");var subQ193=sQuery(id+"F28.wireOp",EDGE,"E668");var subQ194=sQuery(id+"F28.wireOp",EDGE,"E667");var subQ195=sQuery(id+"F28.wireOp",EDGE,"E870");var subQ196=sQuery(id+"F28.wireOp",EDGE,"E869");var subQ197=sQuery(id+"F28.wireOp",EDGE,"E868");var subQ198=sQuery(id+"F28.wireOp",EDGE,"E866");var subQ199=sQuery(id+"F28.wireOp",EDGE,"E865");var subQ200=sQuery(id+"F28.wireOp",EDGE,"E862");var subQ201=sQuery(id+"F28.wireOp",EDGE,"E337");var subQ202=sQuery(id+"F28.wireOp",EDGE,"E336");var subQ203=sQuery(id+"F28.wireOp",EDGE,"E335");var subQ204=sQuery(id+"F28.wireOp",EDGE,"E333");var subQ205=sQuery(id+"F28.wireOp",EDGE,"E332");var subQ206=sQuery(id+"F28.wireOp",EDGE,"E331");var subQ207=sQuery(id+"F28.wireOp",EDGE,"E330");var subQ208=sQuery(id+"F28.wireOp",EDGE,"E329");var subQ209=sQuery(id+"F28.wireOp",EDGE,"E328");var subQ210=sQuery(id+"F28.wireOp",EDGE,"E327");var subQ211=sQuery(id+"F28.wireOp",EDGE,"E326");var subQ212=sQuery(id+"F28.wireOp",EDGE,"E325");var subQ213=sQuery(id+"F28.wireOp",EDGE,"E324");var subQ214=sQuery(id+"F28.wireOp",EDGE,"E323");var subQ215=sQuery(id+"F28.wireOp",EDGE,"E322");var subQ216=sQuery(id+"F28.wireOp",EDGE,"E321");var subQ217=sQuery(id+"F28.wireOp",EDGE,"E320");var subQ218=sQuery(id+"F28.wireOp",EDGE,"E319");var subQ219=sQuery(id+"F28.wireOp",EDGE,"E318");var subQ220=sQuery(id+"F28.wireOp",EDGE,"E317");var subQ221=sQuery(id+"F28.wireOp",EDGE,"E316");var subQ222=sQuery(id+"F28.wireOp",EDGE,"E315");var subQ223=sQuery(id+"F28.wireOp",EDGE,"E314");var subQ224=sQuery(id+"F28.wireOp",EDGE,"E313");var subQ225=sQuery(id+"F28.wireOp",EDGE,"E312");var subQ226=sQuery(id+"F28.wireOp",EDGE,"E311");var subQ227=sQuery(id+"F28.wireOp",EDGE,"E310");var subQ228=sQuery(id+"F28.wireOp",EDGE,"E309");var subQ229=sQuery(id+"F28.wireOp",EDGE,"E308");var subQ230=sQuery(id+"F28.wireOp",EDGE,"E307");var subQ231=sQuery(id+"F28.wireOp",EDGE,"E306");var subQ232=sQuery(id+"F28.wireOp",EDGE,"E305");var subQ233=sQuery(id+"F28.wireOp",EDGE,"E304");var subQ234=sQuery(id+"F28.wireOp",EDGE,"E303");var subQ235=sQuery(id+"F28.wireOp",EDGE,"E302");var subQ236=sQuery(id+"F28.wireOp",EDGE,"E301");var subQ237=sQuery(id+"F28.wireOp",EDGE,"E300");var subQ238=sQuery(id+"F28.wireOp",EDGE,"E299");var subQ239=sQuery(id+"F28.wireOp",EDGE,"E298");var subQ240=sQuery(id+"F28.wireOp",EDGE,"E297");var subQ241=sQuery(id+"F28.wireOp",EDGE,"E296");var subQ242=sQuery(id+"F28.wireOp",EDGE,"E295");var subQ243=sQuery(id+"F28.wireOp",EDGE,"E294");var subQ244=sQuery(id+"F28.wireOp",EDGE,"E293");var subQ245=sQuery(id+"F28.wireOp",EDGE,"E292");var subQ246=sQuery(id+"F28.wireOp",EDGE,"E291");var subQ247=sQuery(id+"F28.wireOp",EDGE,"E290");var subQ248=sQuery(id+"F28.wireOp",EDGE,"E289");var subQ249=sQuery(id+"F28.wireOp",EDGE,"E288");var subQ250=sQuery(id+"F28.wireOp",EDGE,"E287");var subQ251=sQuery(id+"F28.wireOp",EDGE,"E286");var subQ252=sQuery(id+"F28.wireOp",EDGE,"E285");var subQ253=sQuery(id+"F28.wireOp",EDGE,"E284");var subQ254=sQuery(id+"F28.wireOp",EDGE,"E283");var subQ255=sQuery(id+"F28.wireOp",EDGE,"E282");var subQ256=sQuery(id+"F28.wireOp",EDGE,"E281");var subQ257=sQuery(id+"F28.wireOp",EDGE,"E280");var subQ258=sQuery(id+"F28.wireOp",EDGE,"E279");var subQ259=sQuery(id+"F28.wireOp",EDGE,"E278");var subQ260=sQuery(id+"F28.wireOp",EDGE,"E277");var subQ261=sQuery(id+"F28.wireOp",EDGE,"E276");var subQ262=sQuery(id+"F28.wireOp",EDGE,"E275");var subQ263=sQuery(id+"F28.wireOp",EDGE,"E274");var subQ264=sQuery(id+"F28.wireOp",EDGE,"E273");var subQ265=sQuery(id+"F28.wireOp",EDGE,"E272");var subQ266=sQuery(id+"F28.wireOp",EDGE,"E271");var subQ267=sQuery(id+"F28.wireOp",EDGE,"E270");var subQ268=sQuery(id+"F28.wireOp",EDGE,"E269");var subQ269=sQuery(id+"F28.wireOp",EDGE,"E268");var subQ270=sQuery(id+"F28.wireOp",EDGE,"E267");var subQ271=sQuery(id+"F28.wireOp",EDGE,"E266");var subQ272=sQuery(id+"F28.wireOp",EDGE,"E265");var subQ273=sQuery(id+"F28.wireOp",EDGE,"E264");var subQ274=sQuery(id+"F28.wireOp",EDGE,"E263");var subQ275=sQuery(id+"F28.wireOp",EDGE,"E262");var subQ276=sQuery(id+"F28.wireOp",EDGE,"E261");var subQ277=sQuery(id+"F28.wireOp",EDGE,"E260");var subQ278=sQuery(id+"F28.wireOp",EDGE,"E259");var subQ279=sQuery(id+"F28.wireOp",EDGE,"E258");var subQ280=sQuery(id+"F28.wireOp",EDGE,"E257");var subQ281=sQuery(id+"F28.wireOp",EDGE,"E256");var subQ282=sQuery(id+"F28.wireOp",EDGE,"E255");var subQ283=sQuery(id+"F28.wireOp",EDGE,"E254");var subQ284=sQuery(id+"F28.wireOp",EDGE,"E253");var subQ285=sQuery(id+"F28.wireOp",EDGE,"E194");var subQ286=sQuery(id+"F28.wireOp",EDGE,"E193");var subQ287=sQuery(id+"F28.wireOp",EDGE,"E192");var subQ288=sQuery(id+"F28.wireOp",EDGE,"E191");var subQ289=sQuery(id+"F28.wireOp",EDGE,"E190");var subQ290=sQuery(id+"F28.wireOp",EDGE,"E189");var subQ291=sQuery(id+"F28.wireOp",EDGE,"E188");var subQ292=sQuery(id+"F28.wireOp",EDGE,"E187");var subQ293=sQuery(id+"F28.wireOp",EDGE,"E186");var subQ294=sQuery(id+"F28.wireOp",EDGE,"E185");var subQ295=sQuery(id+"F28.wireOp",EDGE,"E184");var subQ296=sQuery(id+"F28.wireOp",EDGE,"E183");var subQ297=sQuery(id+"F28.wireOp",EDGE,"E182");var subQ298=sQuery(id+"F28.wireOp",EDGE,"E135");var subQ299=sQuery(id+"F0.wireOp",EDGE,"E7.rect.bottom");var subQ302=sQuery(id+"F0.wireOp",EDGE,"E7.rect.right");var subQ303=sQuery(id+"F0.wireOp",EDGE,"E7.rect.left");var subQ304=sQuery(id+"F0.wireOp",EDGE,"E7.rect.top");var subQ305=sQuery(id+"F0.wireOp",EDGE,"E5.MirrorC");var subQ306=sQuery(id+"F0.wireOp",EDGE,"E3");var subQ307=sQuery(id+"F0.wireOp",EDGE,"E2");var subQ308=sQuery(id+"F0.wireOp",EDGE,"E1");var subQ309=makeQuery(id+"F1.opExtrude","CAP_FACE",FACE,{"disambiguationData":[OSD([subQ308,subQ307,subQ306,subQ305,subQ299,subQ304,subQ303,subQ302])],"isStart":false});var subQ312=makeQuery(id+"F6.opShell","OFFSET_FACE",FACE,{"disambiguationData":[OSD([subQ308,subQ307,subQ306,subQ305,subQ299,subQ304,subQ303,subQ302]),TDD([subQ309])]});Q1=makeQuery(id+"FJWMqh2IEPeAUYh_1.boolean.opBoolean","MERGE",FACE,{"derivedFrom":[makeQuery(id+"F29.boolean.opBoolean","SPLIT",FACE,{"disambiguationData":[TD([makeQuery(id+"F29.opExtrude","SWEPT_FACE",FACE,{"disambiguationData":[OSD([subQ298])]})])],"derivedFrom":subQ312}),makeQuery(id+"F29.boolean.opBoolean","SPLIT",FACE,{"disambiguationData":[TD([makeQuery(id+"F29.opExtrude","SWEPT_FACE",FACE,{"disambiguationData":[OSD([subQ262])]})])],"derivedFrom":subQ312}),makeQuery(id+"F29.boolean.opBoolean","SPLIT",FACE,{"disambiguationData":[TD([makeQuery(id+"F29.opExtrude","SWEPT_FACE",FACE,{"disambiguationData":[OSD([subQ297])]})])],"derivedFrom":subQ312}),makeQuery(id+"FJWMqh2IEPeAUYh_1.opExtrude","CAP_FACE",FACE,{"disambiguationData":[OSD([subQ298,sQuery(id+"F28.wireOp",EDGE,"E136"),sQuery(id+"F28.wireOp",EDGE,"E137"),sQuery(id+"F28.wireOp",EDGE,"E138"),sQuery(id+"F28.wireOp",EDGE,"E139"),sQuery(id+"F28.wireOp",EDGE,"E140"),sQuery(id+"F28.wireOp",EDGE,"E141"),sQuery(id+"F28.wireOp",EDGE,"E142"),sQuery(id+"F28.wireOp",EDGE,"E143"),sQuery(id+"F28.wireOp",EDGE,"E144"),sQuery(id+"F28.wireOp",EDGE,"E145"),sQuery(id+"F28.wireOp",EDGE,"E146"),sQuery(id+"F28.wireOp",EDGE,"E147"),sQuery(id+"F28.wireOp",EDGE,"E148"),sQuery(id+"F28.wireOp",EDGE,"E149"),sQuery(id+"F28.wireOp",EDGE,"E150"),sQuery(id+"F28.wireOp",EDGE,"E151"),sQuery(id+"F28.wireOp",EDGE,"E152"),sQuery(id+"F28.wireOp",EDGE,"E153"),sQuery(id+"F28.wireOp",EDGE,"E154"),sQuery(id+"F28.wireOp",EDGE,"E155"),sQuery(id+"F28.wireOp",EDGE,"E156"),sQuery(id+"F28.wireOp",EDGE,"E157"),sQuery(id+"F28.wireOp",EDGE,"E158"),sQuery(id+"F28.wireOp",EDGE,"E159"),sQuery(id+"F28.wireOp",EDGE,"E160"),sQuery(id+"F28.wireOp",EDGE,"E161"),sQuery(id+"F28.wireOp",EDGE,"E162"),sQuery(id+"F28.wireOp",EDGE,"E163"),sQuery(id+"F28.wireOp",EDGE,"E164"),sQuery(id+"F28.wireOp",EDGE,"E165"),sQuery(id+"F28.wireOp",EDGE,"E166"),sQuery(id+"F28.wireOp",EDGE,"E167"),sQuery(id+"F28.wireOp",EDGE,"E168"),sQuery(id+"F28.wireOp",EDGE,"E169"),sQuery(id+"F28.wireOp",EDGE,"E170"),sQuery(id+"F28.wireOp",EDGE,"E171"),sQuery(id+"F28.wireOp",EDGE,"E172"),sQuery(id+"F28.wireOp",EDGE,"E173"),sQuery(id+"F28.wireOp",EDGE,"E174"),sQuery(id+"F28.wireOp",EDGE,"E175"),sQuery(id+"F28.wireOp",EDGE,"E176"),sQuery(id+"F28.wireOp",EDGE,"E177"),sQuery(id+"F28.wireOp",EDGE,"E178"),sQuery(id+"F28.wireOp",EDGE,"E179"),sQuery(id+"F28.wireOp",EDGE,"E180"),sQuery(id+"F28.wireOp",EDGE,"E181"),subQ297,subQ296,subQ295,subQ294,subQ293,subQ292,subQ291,subQ290,subQ289,subQ288,subQ287,subQ286,subQ285,sQuery(id+"F28.wireOp",EDGE,"E195"),sQuery(id+"F28.wireOp",EDGE,"E196"),sQuery(id+"F28.wireOp",EDGE,"E197"),sQuery(id+"F28.wireOp",EDGE,"E198"),sQuery(id+"F28.wireOp",EDGE,"E199"),sQuery(id+"F28.wireOp",EDGE,"E200"),sQuery(id+"F28.wireOp",EDGE,"E201"),sQuery(id+"F28.wireOp",EDGE,"E202"),sQuery(id+"F28.wireOp",EDGE,"E203"),sQuery(id+"F28.wireOp",EDGE,"E204"),sQuery(id+"F28.wireOp",EDGE,"E205"),sQuery(id+"F28.wireOp",EDGE,"E206"),sQuery(id+"F28.wireOp",EDGE,"E207"),sQuery(id+"F28.wireOp",EDGE,"E208"),sQuery(id+"F28.wireOp",EDGE,"E209"),sQuery(id+"F28.wireOp",EDGE,"E210"),sQuery(id+"F28.wireOp",EDGE,"E211"),sQuery(id+"F28.wireOp",EDGE,"E212"),sQuery(id+"F28.wireOp",EDGE,"E213"),sQuery(id+"F28.wireOp",EDGE,"E214"),sQuery(id+"F28.wireOp",EDGE,"E215"),sQuery(id+"F28.wireOp",EDGE,"E216"),sQuery(id+"F28.wireOp",EDGE,"E217"),sQuery(id+"F28.wireOp",EDGE,"E218"),sQuery(id+"F28.wireOp",EDGE,"E219"),sQuery(id+"F28.wireOp",EDGE,"E220"),sQuery(id+"F28.wireOp",EDGE,"E221"),sQuery(id+"F28.wireOp",EDGE,"E222"),sQuery(id+"F28.wireOp",EDGE,"E223"),sQuery(id+"F28.wireOp",EDGE,"E224"),sQuery(id+"F28.wireOp",EDGE,"E225"),sQuery(id+"F28.wireOp",EDGE,"E226"),sQuery(id+"F28.wireOp",EDGE,"E227"),sQuery(id+"F28.wireOp",EDGE,"E228"),sQuery(id+"F28.wireOp",EDGE,"E229"),sQuery(id+"F28.wireOp",EDGE,"E230"),sQuery(id+"F28.wireOp",EDGE,"E231"),sQuery(id+"F28.wireOp",EDGE,"E232"),sQuery(id+"F28.wireOp",EDGE,"E233"),sQuery(id+"F28.wireOp",EDGE,"E234"),sQuery(id+"F28.wireOp",EDGE,"E235"),sQuery(id+"F28.wireOp",EDGE,"E236"),sQuery(id+"F28.wireOp",EDGE,"E237"),sQuery(id+"F28.wireOp",EDGE,"E238"),sQuery(id+"F28.wireOp",EDGE,"E239"),sQuery(id+"F28.wireOp",EDGE,"E240"),sQuery(id+"F28.wireOp",EDGE,"E241"),sQuery(id+"F28.wireOp",EDGE,"E242"),sQuery(id+"F28.wireOp",EDGE,"E243"),sQuery(id+"F28.wireOp",EDGE,"E244"),sQuery(id+"F28.wireOp",EDGE,"E245"),sQuery(id+"F28.wireOp",EDGE,"E246"),sQuery(id+"F28.wireOp",EDGE,"E247"),sQuery(id+"F28.wireOp",EDGE,"E248"),sQuery(id+"F28.wireOp",EDGE,"E249"),sQuery(id+"F28.wireOp",EDGE,"E250"),sQuery(id+"F28.wireOp",EDGE,"E251"),sQuery(id+"F28.wireOp",EDGE,"E252"),subQ284,subQ283,subQ282,subQ281,subQ280,subQ279,subQ278,subQ277,subQ276,subQ275,subQ274,subQ273,subQ272,subQ271,subQ270,subQ269,subQ268,subQ267,subQ266,subQ265,subQ264,subQ263,subQ262,subQ261,subQ260,subQ259,subQ258,subQ257,subQ256,subQ255,subQ254,subQ253,subQ252,subQ251,subQ250,subQ249,subQ248,subQ247,subQ246,subQ245,subQ244,subQ243,subQ242,subQ241,subQ240,subQ239,subQ238,subQ237,subQ236,subQ235,subQ234,subQ233,subQ232,subQ231,subQ230,subQ229,subQ228,subQ227,subQ226,subQ225,subQ224,subQ223,subQ222,subQ221,subQ220,subQ219,subQ218,subQ217,subQ216,subQ215,subQ214,subQ213,subQ212,subQ211,subQ210,subQ209,subQ208,subQ207,subQ206,subQ205,subQ204,sQuery(id+"F28.wireOp",EDGE,"E334"),subQ203,subQ202,subQ201,subQ200,sQuery(id+"F28.wireOp",EDGE,"E863"),sQuery(id+"F28.wireOp",EDGE,"E864"),subQ199,subQ198,sQuery(id+"F28.wireOp",EDGE,"E867"),subQ197,subQ196,subQ195])],"isStart":false}),makeQuery(id+"FJWMqh2IEPeAUYh_1.opExtrude","CAP_FACE",FACE,{"disambiguationData":[OSD([subQ194,subQ193,subQ192,subQ191,subQ190,subQ189,subQ188,subQ187,subQ186,subQ185,subQ184,subQ183,subQ182,subQ181,subQ180,subQ179,subQ178,subQ177,subQ176,subQ175,subQ174,subQ173,subQ172,subQ171,subQ170,subQ169,subQ168,subQ167,subQ166,subQ165,subQ164,subQ163,subQ162,subQ161,subQ160,subQ159,subQ158,subQ157,subQ156,subQ155,subQ154,subQ153,subQ152,subQ151,subQ150,subQ149])],"isStart":false}),makeQuery(id+"FJWMqh2IEPeAUYh_1.opExtrude","CAP_FACE",FACE,{"disambiguationData":[OSD([subQ148,subQ147,subQ146,subQ145,subQ144,subQ143,subQ142,subQ141,subQ140,subQ139,subQ138,subQ137,subQ136,subQ135,subQ134,subQ133,subQ132,subQ131,subQ130,subQ129,subQ128,subQ127,subQ126,subQ125,subQ124,subQ123,subQ122,subQ121,subQ120,subQ119,subQ118,subQ117,subQ116,subQ115,subQ114,subQ113,subQ112,subQ111,subQ110,subQ109,subQ108,subQ107,subQ106,subQ105,subQ104,subQ103,subQ102,subQ101,subQ100])],"isStart":false}),makeQuery(id+"FJWMqh2IEPeAUYh_1.opExtrude","CAP_FACE",FACE,{"disambiguationData":[OSD([subQ99,subQ98,subQ97,subQ96,subQ95,subQ94,subQ93,subQ92,subQ91,subQ90,subQ89,subQ88,subQ87,subQ86,subQ85,subQ84,subQ83,subQ82,subQ81,subQ80,subQ79,subQ78,subQ77,subQ76,subQ75,subQ74,subQ73,subQ72,subQ71,subQ70,subQ69,subQ68,subQ67,subQ66,subQ65,subQ64,subQ63,subQ62,subQ61,subQ60,subQ59,subQ58,subQ57,subQ56,subQ55,subQ54,subQ53,subQ52,subQ51,subQ50,subQ49,subQ48,subQ47,subQ46,subQ45,subQ44])],"isStart":false}),makeQuery(id+"FJWMqh2IEPeAUYh_1.opExtrude","CAP_FACE",FACE,{"disambiguationData":[OSD([subQ43,subQ42,subQ41,subQ40,subQ39,subQ38,subQ37,subQ36,subQ35,subQ34,subQ33,subQ32,subQ31,subQ30,subQ29,subQ28,subQ27,subQ26,subQ25,subQ24,subQ23,subQ22,subQ21,subQ20,subQ19,subQ18,subQ17,subQ16,subQ15,subQ14,subQ13,subQ12,subQ11,subQ10,subQ9,subQ8,subQ7,subQ6,subQ5,subQ4,subQ3,subQ2,subQ1,subQ0])],"isStart":false})]});}
            extrude(context, id + "F43", {"entities" : qUnion([Q0]), "operationType" : NewBodyOperationType.ADD, "endBound" : BoundingType.UP_TO_SURFACE, "endBoundEntityFace" : qUnion([Q1]), "depth" : 25 * mm});
        }
        {
            var Q0;
            {var subQ0=sQuery(id+"F0.wireOp",EDGE,"E7.rect.right");var subQ2=sQuery(id+"F0.wireOp",EDGE,"E7.rect.bottom");var subQ3=makeQuery(id+"F1.opExtrude","SWEPT_FACE",FACE,{"disambiguationData":[OSD([subQ2])]});var subQ8=sQuery(id+"F0.wireOp",EDGE,"E7.rect.left");var subQ17=sQuery(id+"F0.wireOp",EDGE,"E7.rect.top");var subQ19=sQuery(id+"F0.wireOp",EDGE,"E5.MirrorC");var subQ20=sQuery(id+"F0.wireOp",EDGE,"E3");var subQ21=sQuery(id+"F0.wireOp",EDGE,"E2");var subQ22=sQuery(id+"F0.wireOp",EDGE,"E1");var subQ23=makeQuery(id+"F1.opExtrude","CAP_FACE",FACE,{"disambiguationData":[OSD([subQ22,subQ21,subQ20,subQ19,subQ2,subQ17,subQ8,subQ0])],"isStart":true});Q0=makeQuery(id+"F26.boolean.opBoolean","MERGE",FACE,{"derivedFrom":[makeQuery(id+"F6.opShell","OFFSET_FACE",FACE,{"disambiguationData":[OSD([subQ22,subQ21,subQ20,subQ19,subQ2,subQ17,subQ8,subQ0]),TDD([subQ23]),OD(2.0)]}),makeQuery(id+"F14.boolean.opBoolean","SPLIT",FACE,{"disambiguationData":[TD([makeQuery(id+"F1.opExtrude","SWEPT_FACE",FACE,{"disambiguationData":[OSD([subQ22])]})])],"derivedFrom":makeQuery(id+"F6.opShell","OFFSET_FACE",FACE,{"disambiguationData":[OSD([subQ22,subQ21,subQ20,subQ19,subQ2,subQ17,subQ8,subQ0]),TDD([subQ23]),OD(0.0)]})}),makeQuery(id+"F14.boolean.opBoolean","SPLIT",FACE,{"disambiguationData":[TD([subQ3])],"derivedFrom":makeQuery(id+"F10.boolean.opBoolean","SPLIT",FACE,{"disambiguationData":[TD([subQ3])],"derivedFrom":makeQuery(id+"F6.opShell","OFFSET_FACE",FACE,{"disambiguationData":[OSD([subQ22,subQ21,subQ20,subQ19,subQ2,subQ17,subQ8,subQ0]),TDD([subQ23]),OD(3.0)]})})}),makeQuery(id+"F26.opExtrude","CAP_FACE",FACE,{"disambiguationData":[OSD([sQuery(id+"F25.wireOp",EDGE,"E114.top"),sQuery(id+"F25.wireOp",EDGE,"E114.left"),sQuery(id+"F25.wireOp",EDGE,"E114.right"),sQuery(id+"F25.wireOp",EDGE,"E115.bottom"),sQuery(id+"F25.wireOp",EDGE,"E115.top"),sQuery(id+"F25.wireOp",EDGE,"E115.right"),sQuery(id+"F25.wireOp",EDGE,"E114.bottom"),sQuery(id+"F25.wireOp",EDGE,"E119.top"),sQuery(id+"F25.wireOp",EDGE,"E119.left"),sQuery(id+"F25.wireOp",EDGE,"E119.right")])],"isStart":true}),makeQuery(id+"F26.opExtrude","CAP_FACE",FACE,{"disambiguationData":[OSD([sQuery(id+"F25.wireOp",EDGE,"E117.bottom"),sQuery(id+"F25.wireOp",EDGE,"E117.top"),sQuery(id+"F25.wireOp",EDGE,"E117.left"),sQuery(id+"F25.wireOp",EDGE,"E117.right"),sQuery(id+"F25.wireOp",EDGE,"E118.bottom"),sQuery(id+"F25.wireOp",EDGE,"E118.top"),sQuery(id+"F25.wireOp",EDGE,"E118.right")])],"isStart":true})]});}
            cPlane(context, id + "F44", {"entities" : qUnion([Q0]), "cplaneType" : CPlaneType.OFFSET, "offset" : 0.6 * mm, "oppositeDirection" : true, "width" : 150 * mm, "height" : 150 * mm});
        }
        {
            var Q0;
            Q0=qCreatedBy(id+"F44.planeOp",FACE);
            var sketch = newSketch(context, id + "F45", { "sketchPlane" : qUnion([Q0])});
            skLineSegment(sketch, "E903.bottom", {"start": v(-24.07, 22.32) * mm, "end": v(-9.14, 22.32) * mm});
            skLineSegment(sketch, "E903.top", {"start": v(-24.07, -4.65) * mm, "end": v(-9.14, -4.65) * mm});
            skLineSegment(sketch, "E903.left", {"start": v(-24.07, 22.32) * mm, "end": v(-24.07, -4.65) * mm});
            skLineSegment(sketch, "E903.right", {"start": v(-9.14, 22.32) * mm, "end": v(-9.14, -4.65) * mm});
            skSolve(sketch);
        }
        {
            var Q0;
            Q0=qSketchRegion(id+"F45",true);
            extrude(context, id + "F46", {"entities" : qUnion([Q0]), "depth" : 0.6 * mm});
        }
        {
            var Q0;
            Q0=qCreatedBy(makeId("Top.planeOp"),FACE);
            var sketch = newSketch(context, id + "F47", { "sketchPlane" : qUnion([Q0])});
            skLineSegment(sketch, "E904.bottom", {"start": v(-32.16, -19.74) * mm, "end": v(-31.86, -19.74) * mm});
            skLineSegment(sketch, "E904.top", {"start": v(-32.16, -29.43) * mm, "end": v(-31.86, -29.43) * mm});
            skLineSegment(sketch, "E904.left", {"start": v(-32.16, -19.74) * mm, "end": v(-32.16, -29.43) * mm});
            skLineSegment(sketch, "E904.right", {"start": v(-31.86, -19.74) * mm, "end": v(-31.86, -29.43) * mm});
            skLineSegment(sketch, "E905.bottom", {"start": v(-34.1, 3.13) * mm, "end": v(-31.72, 3.13) * mm});
            skLineSegment(sketch, "E905.top", {"start": v(-34.1, 0.35) * mm, "end": v(-31.72, 0.35) * mm});
            skLineSegment(sketch, "E905.left", {"start": v(-34.1, 3.13) * mm, "end": v(-34.1, 0.35) * mm});
            skLineSegment(sketch, "E905.right", {"start": v(-31.72, 3.13) * mm, "end": v(-31.72, 0.35) * mm});
            skLineSegment(sketch, "E906.bottom", {"start": v(-34.13, -7.9) * mm, "end": v(-31.72, -7.9) * mm});
            skLineSegment(sketch, "E906.top", {"start": v(-34.13, -10.8) * mm, "end": v(-31.72, -10.8) * mm});
            skLineSegment(sketch, "E906.left", {"start": v(-34.13, -7.9) * mm, "end": v(-34.13, -10.8) * mm});
            skLineSegment(sketch, "E906.right", {"start": v(-31.72, -7.9) * mm, "end": v(-31.72, -10.8) * mm});
            skLineSegment(sketch, "E907", {"start": v(-33.4, -10.8) * mm, "end": v(-33.4, -7.9) * mm});
            skLineSegment(sketch, "E908", {"start": v(-33.2, 3.13) * mm, "end": v(-33.2, 0.35) * mm});
            skLineSegment(sketch, "E909.trimOffspring", {"start": v(-33.4, 0.35) * mm, "end": v(-33.4, 3.13) * mm});
            skLineSegment(sketch, "E910.trimOffspring", {"start": v(-33.2, -7.9) * mm, "end": v(-33.2, -10.8) * mm});
            skSolve(sketch);
        }
        {
            var Q0;
            {var subQ0=sQuery(id+"F47.wireOp",EDGE,"E905.left");Q0=makeQuery(id+"F47.imprint","IMPRINT",FACE,{"disambiguationData":[TD([[makeQuery(id+"F47.imprint","IMPRINT",EDGE,{"derivedFrom":subQ0}),1.0]])]});}
            var Q1;
            {var subQ0=sQuery(id+"F47.wireOp",EDGE,"E905.right");Q1=makeQuery(id+"F47.imprint","IMPRINT",FACE,{"disambiguationData":[TD([[makeQuery(id+"F47.imprint","IMPRINT",EDGE,{"derivedFrom":subQ0}),-1.0]])]});}
            var Q2;
            {var subQ0=sQuery(id+"F47.wireOp",EDGE,"E906.left");Q2=makeQuery(id+"F47.imprint","IMPRINT",FACE,{"disambiguationData":[TD([[makeQuery(id+"F47.imprint","IMPRINT",EDGE,{"derivedFrom":subQ0}),1.0]])]});}
            var Q3;
            {var subQ0=sQuery(id+"F47.wireOp",EDGE,"E906.right");Q3=makeQuery(id+"F47.imprint","IMPRINT",FACE,{"disambiguationData":[TD([[makeQuery(id+"F47.imprint","IMPRINT",EDGE,{"derivedFrom":subQ0}),-1.0]])]});}
            var Q4;
            {var subQ0=sQuery(id+"F12.wireOp",EDGE,"E33.top");Q4=makeQuery(id+"F14.boolean.opBoolean","MERGE",FACE,{"derivedFrom":[makeQuery(id+"F13.boolean.opBoolean","COPY",FACE,{"derivedFrom":makeQuery(id+"F13.opExtrude","SWEPT_FACE",FACE,{"disambiguationData":[OSD([subQ0,sQuery(id+"F12.wireOp",EDGE,"E44.trimOffspring"),sQuery(id+"F12.wireOp",EDGE,"E52")])]})}),makeQuery(id+"F14.opExtrude","SWEPT_FACE",FACE,{"disambiguationData":[OSD([subQ0])]})]});}
            extrude(context, id + "F48", {"entities" : qUnion([Q0, Q1, Q2, Q3]), "operationType" : NewBodyOperationType.REMOVE, "endBoundEntityFace" : qUnion([Q4]), "depth" : 6.35 * mm});
        }
        {
            var Q0;
            Q0=makeQuery(id+"F47.imprint","IMPRINT",FACE,{"disambiguationData":[TD([[makeQuery(id+"F47.imprint","IMPRINT",EDGE,{"derivedFrom":sQuery(id+"F47.wireOp",EDGE,"E904.bottom")}),-1.0]])]});
            var Q1;
            Q1=makeQuery(id+"F16.boolean.opBoolean","MERGE",FACE,{"derivedFrom":[makeQuery(id+"F14.boolean.opBoolean","COPY",FACE,{"derivedFrom":makeQuery(id+"F14.opExtrude","SWEPT_FACE",FACE,{"disambiguationData":[OSD([sQuery(id+"F12.wireOp",EDGE,"E39"),sQuery(id+"F12.wireOp",EDGE,"E56")])]})}),makeQuery(id+"F16.opExtrude","CAP_FACE",FACE,{"disambiguationData":[OSD([sQuery(id+"F15.wireOp",EDGE,"E62.bottom"),sQuery(id+"F15.wireOp",EDGE,"E62.left"),sQuery(id+"F15.wireOp",EDGE,"E62.right"),sQuery(id+"F15.wireOp",EDGE,"E64")])],"isStart":false})]});
            extrude(context, id + "F49", {"entities" : qUnion([Q0]), "operationType" : NewBodyOperationType.ADD, "endBound" : BoundingType.UP_TO_SURFACE, "endBoundEntityFace" : qUnion([Q1]), "depth" : 25 * mm});
        }
        {
            var Q0;
            Q0=makeQuery(id+"F35.boolean.opBoolean","MERGE",FACE,{"derivedFrom":[makeQuery(id+"F3.boolean.opBoolean","COPY",FACE,{"derivedFrom":makeQuery(id+"F3.opExtrude","SWEPT_FACE",FACE,{"disambiguationData":[OSD([sQuery(id+"F2.wireOp",EDGE,"E14")])]})}),makeQuery(id+"F35.opExtrude","CAP_FACE",FACE,{"disambiguationData":[OSD([sQuery(id+"F34.wireOp",EDGE,"E876")])],"isStart":false}),makeQuery(id+"F35.opExtrude","CAP_FACE",FACE,{"disambiguationData":[OSD([sQuery(id+"F34.wireOp",EDGE,"E877")])],"isStart":false})]});
            var sketch = newSketch(context, id + "F50", { "sketchPlane" : qUnion([Q0])});
            skText(sketch, "E911", { "text": "12v", "fontName": "OpenSans-Bold.ttf"});
            skText(sketch, "E912", { "text": "L3 L2 L1", "fontName": "OpenSans-Bold.ttf"});
            const initialGuessF50  = {"E911": [0.01715, 0.00103, 1, 0, 0.00547], "E912": [-0.01124, -0.00554, 1, 0, 0.00554]};
            skSetInitialGuess(sketch, initialGuessF50);
            skSolve(sketch);
        }
        {
            var Q0;
            Q0=qSketchRegion(id+"F50",true);
            extrude(context, id + "F51", {"entities" : qUnion([Q0]), "operationType" : NewBodyOperationType.REMOVE, "oppositeDirection" : true, "depth" : 0.9 * mm});
        }
        {
            var Q0;
            {var subQ1=sQuery(id+"F0.wireOp",EDGE,"E7.rect.top");var subQ2=sQuery(id+"F0.wireOp",EDGE,"E7.rect.right");var subQ9=makeQuery(id+"F1.opExtrude","SWEPT_FACE",FACE,{"disambiguationData":[OSD([subQ1])]});Q0=makeQuery(id+"F19.boolean.opBoolean","SPLIT",FACE,{"disambiguationData":[TD([makeQuery(id+"F1.opExtrude","SWEPT_FACE",FACE,{"disambiguationData":[OSD([subQ2])]})])],"derivedFrom":subQ9});}
            var sketch = newSketch(context, id + "F52", { "sketchPlane" : qUnion([Q0])});
            skText(sketch, "E913", { "text": "S2", "fontName": "OpenSans-Bold.ttf"});
            skText(sketch, "E914", { "text": "S3", "fontName": "OpenSans-Bold.ttf"});
            skText(sketch, "E915", { "text": "S1", "fontName": "OpenSans-Bold.ttf"});
            const initialGuessF52  = {"E913": [0.00543, 0.00629, 1, 0, 0.005], "E914": [-0.0147, 0.00046, 1, 0, 0.005], "E915": [0.02787, 0.00057, 1, 0, 0.005]};
            skSetInitialGuess(sketch, initialGuessF52);
            skSolve(sketch);
        }
        {
            var Q0;
            Q0=qSketchRegion(id+"F52",true);
            extrude(context, id + "F53", {"entities" : qUnion([Q0]), "operationType" : NewBodyOperationType.REMOVE, "depth" : 1 * mm, "hasSecondDirection" : true, "secondDirectionOppositeDirection" : true, "secondDirectionDepth" : 1 * mm});
        }
        {
            var Q0;
            {var subQ0=sQuery(id+"F2.wireOp",EDGE,"E22");var subQ1=sQuery(id+"F2.wireOp",EDGE,"E20");Q0=makeQuery(id+"F38.boolean.opBoolean","MERGE",FACE,{"derivedFrom":[makeQuery(id+"F24.boolean.opBoolean","SPLIT",FACE,{"disambiguationData":[TD([makeQuery(id+"F1.opExtrude","SWEPT_FACE",FACE,{"disambiguationData":[OSD([sQuery(id+"F0.wireOp",EDGE,"E3")])]})])],"derivedFrom":makeQuery(id+"F3.boolean.opBoolean","COPY",FACE,{"derivedFrom":makeQuery(id+"F3.opExtrude","SWEPT_FACE",FACE,{"disambiguationData":[OSD([subQ1,subQ0])]})})}),makeQuery(id+"F38.opExtrude","CAP_FACE",FACE,{"disambiguationData":[OSD([sQuery(id+"F37.wireOp",EDGE,"E878")])],"isStart":false}),makeQuery(id+"F38.opExtrude","CAP_FACE",FACE,{"disambiguationData":[OSD([sQuery(id+"F37.wireOp",EDGE,"E879")])],"isStart":false})]});}
            var sketch = newSketch(context, id + "F54", { "sketchPlane" : qUnion([Q0])});
            skText(sketch, "E916", { "text": "S6", "fontName": "OpenSans-Bold.ttf"});
            const initialGuessF54  = {"E916": [0.00536, -0.02288, 1, 0, 0.005]};
            skSetInitialGuess(sketch, initialGuessF54);
            skSolve(sketch);
        }
        {
            var Q0;
            Q0=qSketchRegion(id+"F54",true);
            var Q1;
            Q1=makeQuery(id+"F4.opFillet","BLEND_FACE",FACE,{"disambiguationData":[OSD([sQuery(id+"F0.wireOp",EDGE,"E7.rect.left"),sQuery(id+"F2.wireOp",EDGE,"E20"),sQuery(id+"F2.wireOp",EDGE,"E22")])]});
            extrude(context, id + "F55", {"entities" : qUnion([Q0]), "operationType" : NewBodyOperationType.REMOVE, "oppositeDirection" : true, "depth" : 1 * mm});
        }
        {
            var Q0;
            {var subQ1=sQuery(id+"F0.wireOp",EDGE,"E7.rect.left");var subQ3=sQuery(id+"F0.wireOp",EDGE,"E7.rect.bottom");Q0=makeQuery(id+"F9.boolean.opBoolean","SPLIT",FACE,{"disambiguationData":[TD([makeQuery(id+"F1.opExtrude","SWEPT_FACE",FACE,{"disambiguationData":[OSD([subQ3])]})])],"derivedFrom":makeQuery(id+"F1.opExtrude","SWEPT_FACE",FACE,{"disambiguationData":[OSD([subQ1])]})});}
            var sketch = newSketch(context, id + "F56", { "sketchPlane" : qUnion([Q0])});
            skText(sketch, "E917", { "text": "S5", "fontName": "OpenSans-Bold.ttf"});
            skText(sketch, "E918", { "text": "S4", "fontName": "OpenSans-Bold.ttf"});
            const initialGuessF56  = {"E917": [-0.03102, 0.00035, 1, 0, 0.00488], "E918": [0.00797, 0.0003, 1, 0, 0.0048]};
            skSetInitialGuess(sketch, initialGuessF56);
            skSolve(sketch);
        }
        {
            var Q0;
            {var subQ0=sQuery(id+"F12.wireOp",EDGE,"E53");Q0=makeQuery(id+"F12.imprint","IMPRINT",FACE,{"disambiguationData":[TD([[makeQuery(id+"F12.imprint","IMPRINT",EDGE,{"derivedFrom":subQ0}),-1.0]])]});}
            extrude(context, id + "F57", {"entities" : qUnion([Q0]), "operationType" : NewBodyOperationType.REMOVE, "oppositeDirection" : true, "depth" : 8 * mm});
        }
        {
            var Q0;
            Q0=makeQuery(id+"F0.imprint","IMPRINT",FACE,{"disambiguationData":[TD([[makeQuery(id+"F0.imprint","IMPRINT",EDGE,{"derivedFrom":sQuery(id+"F0.wireOp",EDGE,"E1")}),-1.0]])]});
            var sketch = newSketch(context, id + "F58", { "sketchPlane" : qUnion([Q0])});
            skPoint(sketch, "E919.first.point", {"position": v(6.62, 7.4) * mm});
            skPoint(sketch, "E919.second.point", {"position": v(6.67, 13.38) * mm});
            skPoint(sketch, "E919.third.point", {"position": v(3.73, 10.32) * mm});
            skPoint(sketch, "E920.first.point", {"position": v(17.45, 10.32) * mm});
            skPoint(sketch, "E920.second.point", {"position": v(14.7, 13.34) * mm});
            skPoint(sketch, "E920.third.point", {"position": v(14.7, 7.45) * mm});
            skPoint(sketch, "E921.MirrorP", {"position": v(17.5, 10.32) * mm});
            skPoint(sketch, "E922.MirrorP", {"position": v(14.62, 7.4) * mm});
            skPoint(sketch, "E923.MirrorP", {"position": v(14.57, 13.38) * mm});
            skLineSegment(sketch, "E924", {"start": v(14.46, 6.75) * mm, "end": v(6.63, 6.75) * mm});
            skLineSegment(sketch, "E925", {"start": v(14.66, 13.88) * mm, "end": v(6.96, 13.88) * mm});
            skArc(sketch, "E926.trimOffspring", {"start": v(6.96, 13.88) * mm, "mid": v(3.17, 10.38) * mm, "end": v(6.84, 6.75) * mm});
            skArc(sketch, "E927.trimOffspring", {"start": v(14.27, 13.88) * mm, "mid": v(18.08, 10.42) * mm, "end": v(14.46, 6.75) * mm});
            skPoint(sketch, "E928.orphan", {"position": v(14.5, 10.4) * mm});
            skPoint(sketch, "E929.start.orphan", {"position": v(10.62, 10.36) * mm});
            skCircle(sketch, "E930", {"center": v(6.74, 10.32) * mm, "radius": 2.01 * mm});
            skCircle(sketch, "E931", {"center": v(14.51, 10.32) * mm, "radius": 2.16 * mm});
            skLineSegment(sketch, "E932.trimOffspring", {"start": v(6.52, 13.88) * mm, "end": v(6.5, 13.88) * mm});
            skSolve(sketch);
        }
        {
            var Q0;
            Q0=qSketchRegion(id+"F56",true);
            extrude(context, id + "F59", {"entities" : qUnion([Q0]), "operationType" : NewBodyOperationType.REMOVE, "oppositeDirection" : true, "depth" : 1 * mm});
        }
        {
            var Q0;
            Q0=qSketchRegion(id+"F58",true);
            extrude(context, id + "F60", {"entities" : qUnion([Q0]), "operationType" : NewBodyOperationType.REMOVE, "depth" : 8.2 * mm});
        }
    });
